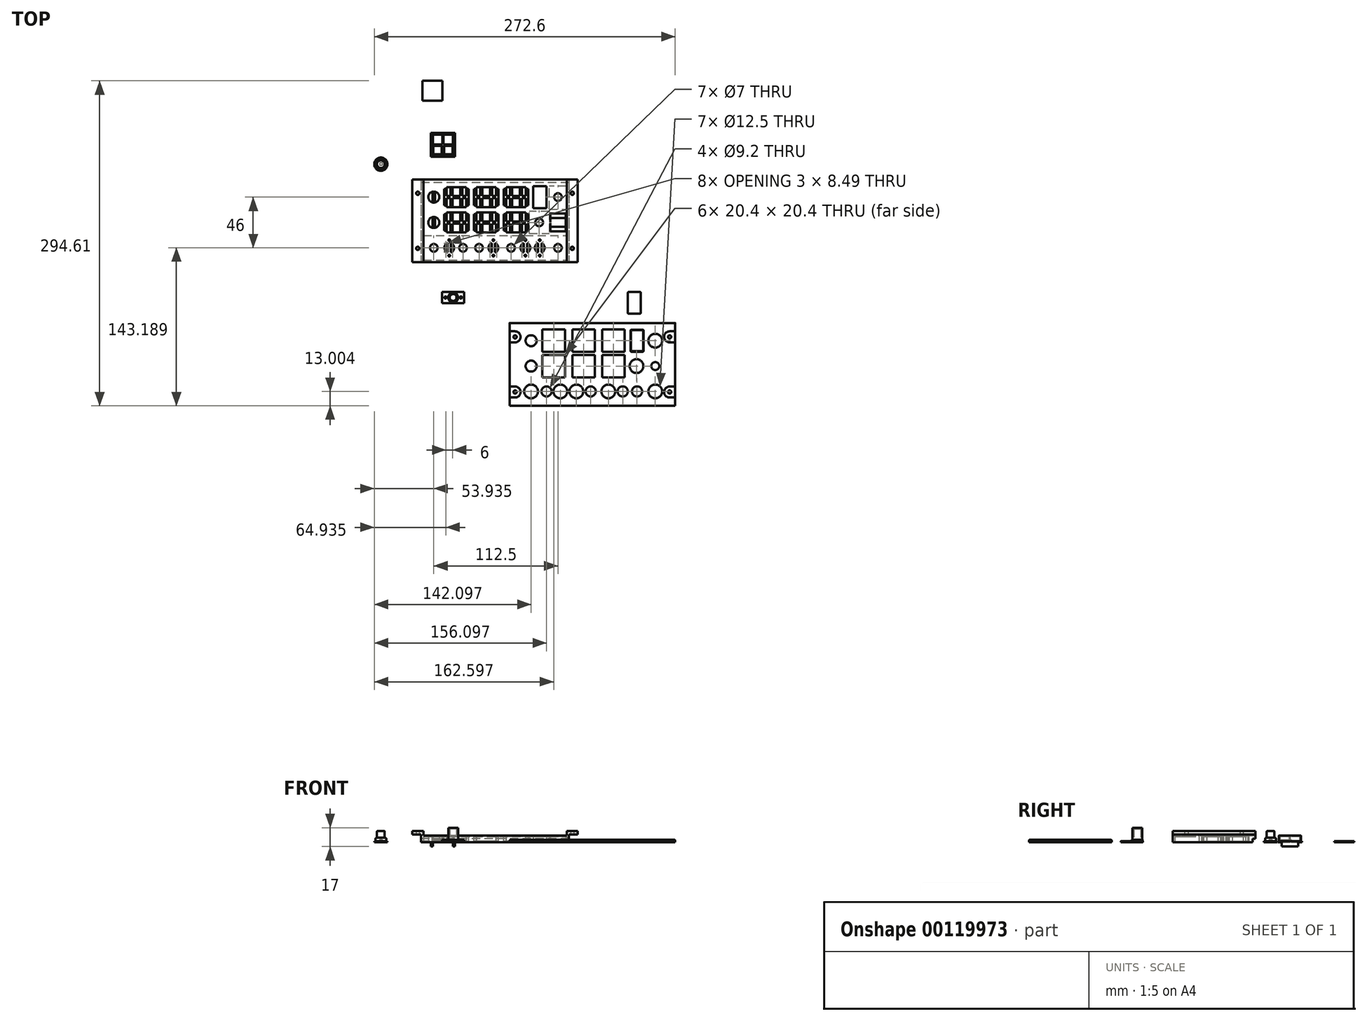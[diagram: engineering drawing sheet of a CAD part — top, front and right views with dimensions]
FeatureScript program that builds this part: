
annotation { "Feature Type Name" : "Feature", "Feature Type Description" : "" }
export const myFeature = defineFeature(function(context is Context, id is Id, definition is map)
    precondition{}
    {
        {
            var Q0;
            Q0=qCreatedBy(makeId("Top.planeOp"),FACE);
            var sketch = newSketch(context, id + "F0", { "sketchPlane" : qUnion([Q0])});
            skLineSegment(sketch, "E0.bottom", {"start": v(0.5, -57.04) * mm, "end": v(-149.5, -57.04) * mm});
            skLineSegment(sketch, "E0.top", {"start": v(0.5, 17.96) * mm, "end": v(-149.5, 17.96) * mm});
            skLineSegment(sketch, "E0.left", {"start": v(0.5, -57.04) * mm, "end": v(0.5, 17.96) * mm});
            skLineSegment(sketch, "E0.right", {"start": v(-149.5, -57.04) * mm, "end": v(-149.5, 17.96) * mm});
            skLineSegment(sketch, "E1.bottom", {"start": v(-99.5, -8.04) * mm, "end": v(-119.5, -8.04) * mm, "construction": true});
            skLineSegment(sketch, "E1.top", {"start": v(-99.5, 11.96) * mm, "end": v(-119.5, 11.96) * mm, "construction": true});
            skLineSegment(sketch, "E1.left", {"start": v(-99.5, -8.04) * mm, "end": v(-99.5, 11.96) * mm, "construction": true});
            skLineSegment(sketch, "E1.right", {"start": v(-119.5, -8.04) * mm, "end": v(-119.5, 11.96) * mm, "construction": true});
            skPoint(sketch, "E1.middle", {"position": v(-109.5, 1.96) * mm});
            skLineSegment(sketch, "E2.bottom", {"start": v(-99.5, -31.04) * mm, "end": v(-119.5, -31.04) * mm, "construction": true});
            skLineSegment(sketch, "E2.top", {"start": v(-99.5, -11.04) * mm, "end": v(-119.5, -11.04) * mm, "construction": true});
            skLineSegment(sketch, "E2.left", {"start": v(-99.5, -31.04) * mm, "end": v(-99.5, -11.04) * mm, "construction": true});
            skLineSegment(sketch, "E2.right", {"start": v(-119.5, -31.04) * mm, "end": v(-119.5, -11.04) * mm, "construction": true});
            skPoint(sketch, "E2.middle", {"position": v(-109.5, -21.04) * mm});
            skCircle(sketch, "E3", {"center": v(-103.5, -44.04) * mm, "radius": 3.5 * mm});
            skCircle(sketch, "E4", {"center": v(-89, -44.04) * mm, "radius": 3.5 * mm});
            skLineSegment(sketch, "E5.bottom", {"start": v(-149.5, 17.96) * mm, "end": v(-141.5, 17.96) * mm, "construction": true});
            skLineSegment(sketch, "E5.top", {"start": v(-149.5, -57.04) * mm, "end": v(-141.5, -57.04) * mm, "construction": true});
            skLineSegment(sketch, "E5.left", {"start": v(-149.5, 17.96) * mm, "end": v(-149.5, -57.04) * mm, "construction": true});
            skLineSegment(sketch, "E5.right", {"start": v(-141.5, 17.96) * mm, "end": v(-141.5, -57.04) * mm, "construction": true});
            skLineSegment(sketch, "E6.bottom", {"start": v(0.5, -57.04) * mm, "end": v(-7.5, -57.04) * mm, "construction": true});
            skLineSegment(sketch, "E6.top", {"start": v(0.5, 17.96) * mm, "end": v(-7.5, 17.96) * mm, "construction": true});
            skLineSegment(sketch, "E6.left", {"start": v(0.5, -57.04) * mm, "end": v(0.5, 17.96) * mm, "construction": true});
            skLineSegment(sketch, "E6.right", {"start": v(-7.5, -57.04) * mm, "end": v(-7.5, 17.96) * mm, "construction": true});
            skCircle(sketch, "E7", {"center": v(-116, -44.04) * mm, "radius": 4.5 * mm});
            skCircle(sketch, "E8", {"center": v(-76, -44.04) * mm, "radius": 4.5 * mm});
            skCircle(sketch, "E9", {"center": v(-60, -44.04) * mm, "radius": 3.5 * mm});
            skCircle(sketch, "E10", {"center": v(-47, -44.04) * mm, "radius": 4.5 * mm});
            skCircle(sketch, "E11", {"center": v(-34, -44.04) * mm, "radius": 4.5 * mm});
            skCircle(sketch, "E12", {"center": v(-17.5, -44.04) * mm, "radius": 3.5 * mm});
            skCircle(sketch, "E13", {"center": v(-34.5, -21.04) * mm, "radius": 3.5 * mm});
            skLineSegment(sketch, "E14.bottom", {"start": v(-28, -8.04) * mm, "end": v(-40, -8.04) * mm});
            skLineSegment(sketch, "E14.top", {"start": v(-28, 11.96) * mm, "end": v(-40, 11.96) * mm});
            skLineSegment(sketch, "E14.left", {"start": v(-28, -8.04) * mm, "end": v(-28, 11.96) * mm});
            skLineSegment(sketch, "E14.right", {"start": v(-40, -8.04) * mm, "end": v(-40, 11.96) * mm});
            skPoint(sketch, "E14.middle", {"position": v(-34, 1.96) * mm});
            skCircle(sketch, "E15", {"center": v(-17.5, 1.96) * mm, "radius": 3.5 * mm});
            skCircle(sketch, "E16", {"center": v(-17.5, -21.04) * mm, "radius": 5 * mm, "construction": true});
            skPoint(sketch, "E17.centerSnap0", {"position": v(-119.5, -21.04) * mm});
            skLineSegment(sketch, "E18.bottom", {"start": v(-100.5, -7.04) * mm, "end": v(-118.5, -7.04) * mm});
            skLineSegment(sketch, "E18.top", {"start": v(-100.5, 10.96) * mm, "end": v(-118.5, 10.96) * mm});
            skLineSegment(sketch, "E18.left", {"start": v(-100.5, -7.04) * mm, "end": v(-100.5, 10.96) * mm});
            skLineSegment(sketch, "E18.right", {"start": v(-118.5, -7.04) * mm, "end": v(-118.5, 10.96) * mm});
            skLineSegment(sketch, "E19.bottom", {"start": v(-100.5, -30.04) * mm, "end": v(-118.5, -30.04) * mm});
            skLineSegment(sketch, "E19.top", {"start": v(-100.5, -12.04) * mm, "end": v(-118.5, -12.04) * mm});
            skLineSegment(sketch, "E19.left", {"start": v(-100.5, -30.04) * mm, "end": v(-100.5, -12.04) * mm});
            skLineSegment(sketch, "E19.right", {"start": v(-118.5, -30.04) * mm, "end": v(-118.5, -12.04) * mm});
            skLineSegment(sketch, "E20.bottom", {"start": v(-100.5, 0.96) * mm, "end": v(-104, 0.96) * mm});
            skLineSegment(sketch, "E20.top", {"start": v(-100.5, 2.96) * mm, "end": v(-104, 2.96) * mm});
            skLineSegment(sketch, "E20.left", {"start": v(-100.5, 0.96) * mm, "end": v(-100.5, 2.96) * mm});
            skLineSegment(sketch, "E20.right", {"start": v(-118.5, 0.96) * mm, "end": v(-118.5, 2.96) * mm});
            skLineSegment(sketch, "E21.bottom", {"start": v(-113, -7.04) * mm, "end": v(-115, -7.04) * mm});
            skLineSegment(sketch, "E21.top", {"start": v(-113, 10.96) * mm, "end": v(-115, 10.96) * mm});
            skLineSegment(sketch, "E21.left", {"start": v(-113, -7.04) * mm, "end": v(-113, 0.96) * mm});
            skLineSegment(sketch, "E21.right", {"start": v(-115, -7.04) * mm, "end": v(-115, 0.96) * mm});
            skPoint(sketch, "E21.middle", {"position": v(-114, 1.96) * mm});
            skLineSegment(sketch, "E22.bottom", {"start": v(-104, -7.04) * mm, "end": v(-106, -7.04) * mm});
            skLineSegment(sketch, "E22.top", {"start": v(-104, 10.96) * mm, "end": v(-106, 10.96) * mm});
            skLineSegment(sketch, "E22.left", {"start": v(-104, -7.04) * mm, "end": v(-104, 0.96) * mm});
            skLineSegment(sketch, "E22.right", {"start": v(-106, -7.04) * mm, "end": v(-106, 0.96) * mm});
            skPoint(sketch, "E22.middle", {"position": v(-105, 1.96) * mm});
            skLineSegment(sketch, "E23.trimOffspring", {"start": v(-115, 2.96) * mm, "end": v(-115, 10.96) * mm});
            skLineSegment(sketch, "E24.trimOffspring", {"start": v(-115, 2.96) * mm, "end": v(-118.5, 2.96) * mm});
            skLineSegment(sketch, "E25.trimOffspring", {"start": v(-113, 2.96) * mm, "end": v(-113, 10.96) * mm});
            skLineSegment(sketch, "E26.trimOffspring", {"start": v(-115, 0.96) * mm, "end": v(-118.5, 0.96) * mm});
            skLineSegment(sketch, "E27.trimOffspring", {"start": v(-106, 2.96) * mm, "end": v(-106, 10.96) * mm});
            skLineSegment(sketch, "E28.trimOffspring", {"start": v(-106, 2.96) * mm, "end": v(-113, 2.96) * mm});
            skLineSegment(sketch, "E29.trimOffspring", {"start": v(-104, 2.96) * mm, "end": v(-104, 10.96) * mm});
            skLineSegment(sketch, "E30.trimOffspring", {"start": v(-106, 0.96) * mm, "end": v(-113, 0.96) * mm});
            skLineSegment(sketch, "E31.bottom", {"start": v(-100.5, -22.04) * mm, "end": v(-104, -22.04) * mm});
            skLineSegment(sketch, "E31.top", {"start": v(-100.5, -20.04) * mm, "end": v(-104, -20.04) * mm});
            skLineSegment(sketch, "E31.left", {"start": v(-100.5, -22.04) * mm, "end": v(-100.5, -20.04) * mm});
            skLineSegment(sketch, "E31.right", {"start": v(-118.5, -22.04) * mm, "end": v(-118.5, -20.04) * mm});
            skLineSegment(sketch, "E32.bottom", {"start": v(-113, -30.04) * mm, "end": v(-115, -30.04) * mm});
            skLineSegment(sketch, "E32.top", {"start": v(-113, -12.04) * mm, "end": v(-115, -12.04) * mm});
            skLineSegment(sketch, "E32.left", {"start": v(-113, -30.04) * mm, "end": v(-113, -22.04) * mm});
            skLineSegment(sketch, "E32.right", {"start": v(-115, -30.04) * mm, "end": v(-115, -22.04) * mm});
            skPoint(sketch, "E32.middle", {"position": v(-114, -21.04) * mm});
            skLineSegment(sketch, "E33.bottom", {"start": v(-104, -30.04) * mm, "end": v(-106, -30.04) * mm});
            skLineSegment(sketch, "E33.top", {"start": v(-104, -12.04) * mm, "end": v(-106, -12.04) * mm});
            skLineSegment(sketch, "E33.left", {"start": v(-104, -30.04) * mm, "end": v(-104, -22.04) * mm});
            skLineSegment(sketch, "E33.right", {"start": v(-106, -30.04) * mm, "end": v(-106, -22.04) * mm});
            skPoint(sketch, "E33.middle", {"position": v(-105, -21.04) * mm});
            skLineSegment(sketch, "E34.trimOffspring", {"start": v(-115, -20.04) * mm, "end": v(-115, -12.04) * mm});
            skLineSegment(sketch, "E35.trimOffspring", {"start": v(-115, -20.04) * mm, "end": v(-118.5, -20.04) * mm});
            skLineSegment(sketch, "E36.trimOffspring", {"start": v(-113, -20.04) * mm, "end": v(-113, -12.04) * mm});
            skLineSegment(sketch, "E37.trimOffspring", {"start": v(-115, -22.04) * mm, "end": v(-118.5, -22.04) * mm});
            skLineSegment(sketch, "E38.trimOffspring", {"start": v(-106, -20.04) * mm, "end": v(-106, -12.04) * mm});
            skLineSegment(sketch, "E39.trimOffspring", {"start": v(-106, -20.04) * mm, "end": v(-113, -20.04) * mm});
            skLineSegment(sketch, "E40.trimOffspring", {"start": v(-104, -20.04) * mm, "end": v(-104, -12.04) * mm});
            skLineSegment(sketch, "E41.trimOffspring", {"start": v(-106, -22.04) * mm, "end": v(-113, -22.04) * mm});
            skPoint(sketch, "E42.middle", {"position": v(-130, 1.96) * mm});
            skPoint(sketch, "E43.middle", {"position": v(-130, -21.04) * mm});
            skLineSegment(sketch, "E44.left", {"start": v(-129, -2.94) * mm, "end": v(-129, 6.86) * mm});
            skLineSegment(sketch, "E44.right", {"start": v(-131, -2.94) * mm, "end": v(-131, 6.86) * mm});
            skLineSegment(sketch, "E45.left", {"start": v(-129, -25.94) * mm, "end": v(-129, -16.14) * mm});
            skLineSegment(sketch, "E45.right", {"start": v(-131, -25.94) * mm, "end": v(-131, -16.14) * mm});
            skCircle(sketch, "E46", {"center": v(-144.5, 5.46) * mm, "radius": 1.5 * mm});
            skPoint(sketch, "E46.centerSnap0", {"position": v(-145.5, 17.96) * mm});
            skCircle(sketch, "E47", {"center": v(-144.5, -44.54) * mm, "radius": 1.5 * mm});
            skCircle(sketch, "E48", {"center": v(-4.5, 5.46) * mm, "radius": 1.5 * mm});
            skCircle(sketch, "E49", {"center": v(-4.5, -44.54) * mm, "radius": 1.5 * mm});
            skLineSegment(sketch, "E50.1.0.0", {"start": v(-73.5, 2.96) * mm, "end": v(-77, 2.96) * mm});
            skLineSegment(sketch, "E50.1.0.1", {"start": v(-79, -30.04) * mm, "end": v(-79, -22.04) * mm});
            skLineSegment(sketch, "E50.1.0.2", {"start": v(-79, -22.04) * mm, "end": v(-86, -22.04) * mm});
            skLineSegment(sketch, "E50.1.0.3", {"start": v(-88, -30.04) * mm, "end": v(-88, -22.04) * mm});
            skLineSegment(sketch, "E50.1.0.4", {"start": v(-72.5, -8.04) * mm, "end": v(-72.5, 11.96) * mm, "construction": true});
            skLineSegment(sketch, "E50.1.0.5", {"start": v(-72.5, -8.04) * mm, "end": v(-92.5, -8.04) * mm, "construction": true});
            skLineSegment(sketch, "E50.1.0.6", {"start": v(-72.5, -31.04) * mm, "end": v(-92.5, -31.04) * mm, "construction": true});
            skLineSegment(sketch, "E50.1.0.7", {"start": v(-73.5, -30.04) * mm, "end": v(-73.5, -12.04) * mm});
            skLineSegment(sketch, "E50.1.0.8", {"start": v(-73.5, -7.04) * mm, "end": v(-91.5, -7.04) * mm});
            skLineSegment(sketch, "E50.1.0.9", {"start": v(-79, 2.96) * mm, "end": v(-86, 2.96) * mm});
            skLineSegment(sketch, "E50.1.0.10", {"start": v(-79, -20.04) * mm, "end": v(-86, -20.04) * mm});
            skLineSegment(sketch, "E50.1.0.11", {"start": v(-88, 2.96) * mm, "end": v(-91.5, 2.96) * mm});
            skLineSegment(sketch, "E50.1.0.12", {"start": v(-77, -30.04) * mm, "end": v(-77, -22.04) * mm});
            skLineSegment(sketch, "E50.1.0.13", {"start": v(-86, 2.96) * mm, "end": v(-86, 10.96) * mm});
            skLineSegment(sketch, "E50.1.0.14", {"start": v(-77, -20.04) * mm, "end": v(-77, -12.04) * mm});
            skLineSegment(sketch, "E50.1.0.15", {"start": v(-88, -20.04) * mm, "end": v(-88, -12.04) * mm});
            skLineSegment(sketch, "E50.1.0.16", {"start": v(-79, 2.96) * mm, "end": v(-79, 10.96) * mm});
            skPoint(sketch, "E50.1.0.17", {"position": v(-82.5, -21.04) * mm});
            skLineSegment(sketch, "E50.1.0.18", {"start": v(-73.5, -22.04) * mm, "end": v(-77, -22.04) * mm});
            skLineSegment(sketch, "E50.1.0.19", {"start": v(-88, 0.96) * mm, "end": v(-91.5, 0.96) * mm});
            skLineSegment(sketch, "E50.1.0.20", {"start": v(-72.5, 11.96) * mm, "end": v(-92.5, 11.96) * mm, "construction": true});
            skLineSegment(sketch, "E50.1.0.21", {"start": v(-88, -22.04) * mm, "end": v(-91.5, -22.04) * mm});
            skLineSegment(sketch, "E50.1.0.22", {"start": v(-91.5, -7.04) * mm, "end": v(-91.5, 10.96) * mm});
            skLineSegment(sketch, "E50.1.0.23", {"start": v(-72.5, -11.04) * mm, "end": v(-92.5, -11.04) * mm, "construction": true});
            skLineSegment(sketch, "E50.1.0.24", {"start": v(-92.5, -31.04) * mm, "end": v(-92.5, -11.04) * mm, "construction": true});
            skLineSegment(sketch, "E50.1.0.25", {"start": v(-79, -20.04) * mm, "end": v(-79, -12.04) * mm});
            skLineSegment(sketch, "E50.1.0.26", {"start": v(-92.5, -8.04) * mm, "end": v(-92.5, 11.96) * mm, "construction": true});
            skLineSegment(sketch, "E50.1.0.27", {"start": v(-88, 2.96) * mm, "end": v(-88, 10.96) * mm});
            skLineSegment(sketch, "E50.1.0.28", {"start": v(-72.5, -31.04) * mm, "end": v(-72.5, -11.04) * mm, "construction": true});
            skLineSegment(sketch, "E50.1.0.29", {"start": v(-73.5, -7.04) * mm, "end": v(-73.5, 10.96) * mm});
            skLineSegment(sketch, "E50.1.0.30", {"start": v(-73.5, -30.04) * mm, "end": v(-91.5, -30.04) * mm});
            skLineSegment(sketch, "E50.1.0.31", {"start": v(-77, -7.04) * mm, "end": v(-77, 0.96) * mm});
            skLineSegment(sketch, "E50.1.0.32", {"start": v(-79, -7.04) * mm, "end": v(-79, 0.96) * mm});
            skLineSegment(sketch, "E50.1.0.33", {"start": v(-86, -20.04) * mm, "end": v(-86, -12.04) * mm});
            skLineSegment(sketch, "E50.1.0.34", {"start": v(-73.5, 0.96) * mm, "end": v(-77, 0.96) * mm});
            skLineSegment(sketch, "E50.1.0.35", {"start": v(-73.5, -12.04) * mm, "end": v(-91.5, -12.04) * mm});
            skLineSegment(sketch, "E50.1.0.36", {"start": v(-86, -30.04) * mm, "end": v(-86, -22.04) * mm});
            skLineSegment(sketch, "E50.1.0.37", {"start": v(-77, 2.96) * mm, "end": v(-77, 10.96) * mm});
            skLineSegment(sketch, "E50.1.0.38", {"start": v(-88, -7.04) * mm, "end": v(-88, 0.96) * mm});
            skLineSegment(sketch, "E50.1.0.39", {"start": v(-91.5, -30.04) * mm, "end": v(-91.5, -12.04) * mm});
            skLineSegment(sketch, "E50.1.0.40", {"start": v(-73.5, 10.96) * mm, "end": v(-91.5, 10.96) * mm});
            skLineSegment(sketch, "E50.1.0.41", {"start": v(-73.5, -20.04) * mm, "end": v(-77, -20.04) * mm});
            skPoint(sketch, "E50.1.0.42", {"position": v(-82.5, 1.96) * mm});
            skPoint(sketch, "E50.1.0.43", {"position": v(-92.5, -21.04) * mm});
            skLineSegment(sketch, "E50.1.0.44", {"start": v(-79, 0.96) * mm, "end": v(-86, 0.96) * mm});
            skLineSegment(sketch, "E50.1.0.45", {"start": v(-86, -7.04) * mm, "end": v(-86, 0.96) * mm});
            skLineSegment(sketch, "E50.1.0.46", {"start": v(-73.5, -12.04) * mm, "end": v(-91.5, -12.04) * mm});
            skLineSegment(sketch, "E50.1.0.47", {"start": v(-73.5, -30.04) * mm, "end": v(-73.5, -12.04) * mm});
            skLineSegment(sketch, "E50.1.0.48", {"start": v(-73.5, -30.04) * mm, "end": v(-91.5, -30.04) * mm});
            skPoint(sketch, "E50.1.0.49", {"position": v(-82.5, -21.04) * mm});
            skPoint(sketch, "E50.1.0.50", {"position": v(-82.5, 1.96) * mm});
            skLineSegment(sketch, "E50.1.0.51", {"start": v(-88, -20.04) * mm, "end": v(-91.5, -20.04) * mm});
            skLineSegment(sketch, "E50.1.0.52", {"start": v(-91.5, -30.04) * mm, "end": v(-91.5, -12.04) * mm});
            skPoint(sketch, "E50.1.0.53", {"position": v(-87, 1.96) * mm});
            skLineSegment(sketch, "E50.1.0.54", {"start": v(-91.5, -22.04) * mm, "end": v(-91.5, -20.04) * mm});
            skLineSegment(sketch, "E50.1.0.55", {"start": v(-86, -12.04) * mm, "end": v(-88, -12.04) * mm});
            skLineSegment(sketch, "E50.1.0.56", {"start": v(-91.5, 0.96) * mm, "end": v(-91.5, 2.96) * mm});
            skLineSegment(sketch, "E50.1.0.57", {"start": v(-86, 10.96) * mm, "end": v(-88, 10.96) * mm});
            skLineSegment(sketch, "E50.1.0.58", {"start": v(-86, -30.04) * mm, "end": v(-88, -30.04) * mm});
            skLineSegment(sketch, "E50.1.0.59", {"start": v(-73.5, -22.04) * mm, "end": v(-73.5, -20.04) * mm});
            skPoint(sketch, "E50.1.0.60", {"position": v(-78, -21.04) * mm});
            skLineSegment(sketch, "E50.1.0.61", {"start": v(-77, -7.04) * mm, "end": v(-79, -7.04) * mm});
            skPoint(sketch, "E50.1.0.62", {"position": v(-87, -21.04) * mm});
            skPoint(sketch, "E50.1.0.63", {"position": v(-82.5, -21.04) * mm});
            skLineSegment(sketch, "E50.1.0.64", {"start": v(-77, -30.04) * mm, "end": v(-79, -30.04) * mm});
            skLineSegment(sketch, "E50.1.0.65", {"start": v(-73.5, 0.96) * mm, "end": v(-73.5, 2.96) * mm});
            skPoint(sketch, "E50.1.0.66", {"position": v(-82.5, 1.96) * mm});
            skLineSegment(sketch, "E50.1.0.67", {"start": v(-86, -7.04) * mm, "end": v(-88, -7.04) * mm});
            skLineSegment(sketch, "E50.1.0.68", {"start": v(-77, 10.96) * mm, "end": v(-79, 10.96) * mm});
            skPoint(sketch, "E50.1.0.69", {"position": v(-78, 1.96) * mm});
            skLineSegment(sketch, "E50.1.0.70", {"start": v(-77, -12.04) * mm, "end": v(-79, -12.04) * mm});
            skPoint(sketch, "E50.1.0.71", {"position": v(-82.5, -21.04) * mm});
            skPoint(sketch, "E50.1.0.72", {"position": v(-82.5, -21.04) * mm});
            skLineSegment(sketch, "E50.2.0.0", {"start": v(-46.5, 2.96) * mm, "end": v(-50, 2.96) * mm});
            skLineSegment(sketch, "E50.2.0.1", {"start": v(-52, -30.04) * mm, "end": v(-52, -22.04) * mm});
            skLineSegment(sketch, "E50.2.0.2", {"start": v(-52, -22.04) * mm, "end": v(-59, -22.04) * mm});
            skLineSegment(sketch, "E50.2.0.3", {"start": v(-61, -30.04) * mm, "end": v(-61, -22.04) * mm});
            skLineSegment(sketch, "E50.2.0.4", {"start": v(-45.5, -8.04) * mm, "end": v(-45.5, 11.96) * mm, "construction": true});
            skLineSegment(sketch, "E50.2.0.5", {"start": v(-45.5, -8.04) * mm, "end": v(-65.5, -8.04) * mm, "construction": true});
            skLineSegment(sketch, "E50.2.0.6", {"start": v(-45.5, -31.04) * mm, "end": v(-65.5, -31.04) * mm, "construction": true});
            skLineSegment(sketch, "E50.2.0.7", {"start": v(-46.5, -30.04) * mm, "end": v(-46.5, -12.04) * mm});
            skLineSegment(sketch, "E50.2.0.8", {"start": v(-46.5, -7.04) * mm, "end": v(-64.5, -7.04) * mm});
            skLineSegment(sketch, "E50.2.0.9", {"start": v(-52, 2.96) * mm, "end": v(-59, 2.96) * mm});
            skLineSegment(sketch, "E50.2.0.10", {"start": v(-52, -20.04) * mm, "end": v(-59, -20.04) * mm});
            skLineSegment(sketch, "E50.2.0.11", {"start": v(-61, 2.96) * mm, "end": v(-64.5, 2.96) * mm});
            skLineSegment(sketch, "E50.2.0.12", {"start": v(-50, -30.04) * mm, "end": v(-50, -22.04) * mm});
            skLineSegment(sketch, "E50.2.0.13", {"start": v(-59, 2.96) * mm, "end": v(-59, 10.96) * mm});
            skLineSegment(sketch, "E50.2.0.14", {"start": v(-50, -20.04) * mm, "end": v(-50, -12.04) * mm});
            skLineSegment(sketch, "E50.2.0.15", {"start": v(-61, -20.04) * mm, "end": v(-61, -12.04) * mm});
            skLineSegment(sketch, "E50.2.0.16", {"start": v(-52, 2.96) * mm, "end": v(-52, 10.96) * mm});
            skPoint(sketch, "E50.2.0.17", {"position": v(-55.5, -21.04) * mm});
            skLineSegment(sketch, "E50.2.0.18", {"start": v(-46.5, -22.04) * mm, "end": v(-50, -22.04) * mm});
            skLineSegment(sketch, "E50.2.0.19", {"start": v(-61, 0.96) * mm, "end": v(-64.5, 0.96) * mm});
            skLineSegment(sketch, "E50.2.0.20", {"start": v(-45.5, 11.96) * mm, "end": v(-65.5, 11.96) * mm, "construction": true});
            skLineSegment(sketch, "E50.2.0.21", {"start": v(-61, -22.04) * mm, "end": v(-64.5, -22.04) * mm});
            skLineSegment(sketch, "E50.2.0.22", {"start": v(-64.5, -7.04) * mm, "end": v(-64.5, 10.96) * mm});
            skLineSegment(sketch, "E50.2.0.23", {"start": v(-45.5, -11.04) * mm, "end": v(-65.5, -11.04) * mm, "construction": true});
            skLineSegment(sketch, "E50.2.0.24", {"start": v(-65.5, -31.04) * mm, "end": v(-65.5, -11.04) * mm, "construction": true});
            skLineSegment(sketch, "E50.2.0.25", {"start": v(-52, -20.04) * mm, "end": v(-52, -12.04) * mm});
            skLineSegment(sketch, "E50.2.0.26", {"start": v(-65.5, -8.04) * mm, "end": v(-65.5, 11.96) * mm, "construction": true});
            skLineSegment(sketch, "E50.2.0.27", {"start": v(-61, 2.96) * mm, "end": v(-61, 10.96) * mm});
            skLineSegment(sketch, "E50.2.0.28", {"start": v(-45.5, -31.04) * mm, "end": v(-45.5, -11.04) * mm, "construction": true});
            skLineSegment(sketch, "E50.2.0.29", {"start": v(-46.5, -7.04) * mm, "end": v(-46.5, 10.96) * mm});
            skLineSegment(sketch, "E50.2.0.30", {"start": v(-46.5, -30.04) * mm, "end": v(-64.5, -30.04) * mm});
            skLineSegment(sketch, "E50.2.0.31", {"start": v(-50, -7.04) * mm, "end": v(-50, 0.96) * mm});
            skLineSegment(sketch, "E50.2.0.32", {"start": v(-52, -7.04) * mm, "end": v(-52, 0.96) * mm});
            skLineSegment(sketch, "E50.2.0.33", {"start": v(-59, -20.04) * mm, "end": v(-59, -12.04) * mm});
            skLineSegment(sketch, "E50.2.0.34", {"start": v(-46.5, 0.96) * mm, "end": v(-50, 0.96) * mm});
            skLineSegment(sketch, "E50.2.0.35", {"start": v(-46.5, -12.04) * mm, "end": v(-64.5, -12.04) * mm});
            skLineSegment(sketch, "E50.2.0.36", {"start": v(-59, -30.04) * mm, "end": v(-59, -22.04) * mm});
            skLineSegment(sketch, "E50.2.0.37", {"start": v(-50, 2.96) * mm, "end": v(-50, 10.96) * mm});
            skLineSegment(sketch, "E50.2.0.38", {"start": v(-61, -7.04) * mm, "end": v(-61, 0.96) * mm});
            skLineSegment(sketch, "E50.2.0.39", {"start": v(-64.5, -30.04) * mm, "end": v(-64.5, -12.04) * mm});
            skLineSegment(sketch, "E50.2.0.40", {"start": v(-46.5, 10.96) * mm, "end": v(-64.5, 10.96) * mm});
            skLineSegment(sketch, "E50.2.0.41", {"start": v(-46.5, -20.04) * mm, "end": v(-50, -20.04) * mm});
            skPoint(sketch, "E50.2.0.42", {"position": v(-55.5, 1.96) * mm});
            skPoint(sketch, "E50.2.0.43", {"position": v(-65.5, -21.04) * mm});
            skLineSegment(sketch, "E50.2.0.44", {"start": v(-52, 0.96) * mm, "end": v(-59, 0.96) * mm});
            skLineSegment(sketch, "E50.2.0.45", {"start": v(-59, -7.04) * mm, "end": v(-59, 0.96) * mm});
            skLineSegment(sketch, "E50.2.0.46", {"start": v(-46.5, -12.04) * mm, "end": v(-64.5, -12.04) * mm});
            skLineSegment(sketch, "E50.2.0.47", {"start": v(-46.5, -30.04) * mm, "end": v(-46.5, -12.04) * mm});
            skLineSegment(sketch, "E50.2.0.48", {"start": v(-46.5, -30.04) * mm, "end": v(-64.5, -30.04) * mm});
            skPoint(sketch, "E50.2.0.49", {"position": v(-55.5, -21.04) * mm});
            skPoint(sketch, "E50.2.0.50", {"position": v(-55.5, 1.96) * mm});
            skLineSegment(sketch, "E50.2.0.51", {"start": v(-61, -20.04) * mm, "end": v(-64.5, -20.04) * mm});
            skLineSegment(sketch, "E50.2.0.52", {"start": v(-64.5, -30.04) * mm, "end": v(-64.5, -12.04) * mm});
            skPoint(sketch, "E50.2.0.53", {"position": v(-60, 1.96) * mm});
            skLineSegment(sketch, "E50.2.0.54", {"start": v(-64.5, -22.04) * mm, "end": v(-64.5, -20.04) * mm});
            skLineSegment(sketch, "E50.2.0.55", {"start": v(-59, -12.04) * mm, "end": v(-61, -12.04) * mm});
            skLineSegment(sketch, "E50.2.0.56", {"start": v(-64.5, 0.96) * mm, "end": v(-64.5, 2.96) * mm});
            skLineSegment(sketch, "E50.2.0.57", {"start": v(-59, 10.96) * mm, "end": v(-61, 10.96) * mm});
            skLineSegment(sketch, "E50.2.0.58", {"start": v(-59, -30.04) * mm, "end": v(-61, -30.04) * mm});
            skLineSegment(sketch, "E50.2.0.59", {"start": v(-46.5, -22.04) * mm, "end": v(-46.5, -20.04) * mm});
            skPoint(sketch, "E50.2.0.60", {"position": v(-51, -21.04) * mm});
            skLineSegment(sketch, "E50.2.0.61", {"start": v(-50, -7.04) * mm, "end": v(-52, -7.04) * mm});
            skPoint(sketch, "E50.2.0.62", {"position": v(-60, -21.04) * mm});
            skPoint(sketch, "E50.2.0.63", {"position": v(-55.5, -21.04) * mm});
            skLineSegment(sketch, "E50.2.0.64", {"start": v(-50, -30.04) * mm, "end": v(-52, -30.04) * mm});
            skLineSegment(sketch, "E50.2.0.65", {"start": v(-46.5, 0.96) * mm, "end": v(-46.5, 2.96) * mm});
            skPoint(sketch, "E50.2.0.66", {"position": v(-55.5, 1.96) * mm});
            skLineSegment(sketch, "E50.2.0.67", {"start": v(-59, -7.04) * mm, "end": v(-61, -7.04) * mm});
            skLineSegment(sketch, "E50.2.0.68", {"start": v(-50, 10.96) * mm, "end": v(-52, 10.96) * mm});
            skPoint(sketch, "E50.2.0.69", {"position": v(-51, 1.96) * mm});
            skLineSegment(sketch, "E50.2.0.70", {"start": v(-50, -12.04) * mm, "end": v(-52, -12.04) * mm});
            skPoint(sketch, "E50.2.0.71", {"position": v(-55.5, -21.04) * mm});
            skPoint(sketch, "E50.2.0.72", {"position": v(-55.5, -21.04) * mm});
            skLineSegment(sketch, "E50.direction1", {"start": v(-119.5, -31.04) * mm, "end": v(-92.5, -31.04) * mm, "construction": true});
            skCircle(sketch, "E51", {"center": v(-130, 1.96) * mm, "radius": 5 * mm});
            skCircle(sketch, "E52", {"center": v(-130, -21.04) * mm, "radius": 5 * mm});
            skLineSegment(sketch, "E53.bottom", {"start": v(-32.5, -8.04) * mm, "end": v(-35.5, -8.04) * mm});
            skLineSegment(sketch, "E53.top", {"start": v(-32.5, 11.96) * mm, "end": v(-35.5, 11.96) * mm});
            skLineSegment(sketch, "E53.left", {"start": v(-32.5, -8.04) * mm, "end": v(-32.5, 11.96) * mm});
            skLineSegment(sketch, "E53.right", {"start": v(-35.5, -8.04) * mm, "end": v(-35.5, 11.96) * mm});
            skLineSegment(sketch, "E54.bottom", {"start": v(-10.5, -29.04) * mm, "end": v(-24.5, -29.04) * mm});
            skLineSegment(sketch, "E54.top", {"start": v(-10.5, -13.04) * mm, "end": v(-24.5, -13.04) * mm});
            skLineSegment(sketch, "E54.left", {"start": v(-10.5, -29.04) * mm, "end": v(-10.5, -13.04) * mm});
            skLineSegment(sketch, "E54.right", {"start": v(-24.5, -29.04) * mm, "end": v(-24.5, -13.04) * mm});
            skLineSegment(sketch, "E55.bottom", {"start": v(-10.5, -25.04) * mm, "end": v(-24.5, -25.04) * mm});
            skLineSegment(sketch, "E55.top", {"start": v(-10.5, -17.04) * mm, "end": v(-24.5, -17.04) * mm});
            skLineSegment(sketch, "E55.left", {"start": v(-10.5, -25.04) * mm, "end": v(-10.5, -17.04) * mm});
            skLineSegment(sketch, "E55.right", {"start": v(-24.5, -25.04) * mm, "end": v(-24.5, -17.04) * mm});
            skLineSegment(sketch, "E56.bottom", {"start": v(-27.5, -28.04) * mm, "end": v(-41.5, -28.04) * mm, "construction": true});
            skLineSegment(sketch, "E56.top", {"start": v(-27.5, -14.04) * mm, "end": v(-41.5, -14.04) * mm, "construction": true});
            skLineSegment(sketch, "E56.left", {"start": v(-27.5, -28.04) * mm, "end": v(-27.5, -14.04) * mm, "construction": true});
            skLineSegment(sketch, "E56.right", {"start": v(-41.5, -28.04) * mm, "end": v(-41.5, -14.04) * mm, "construction": true});
            skCircle(sketch, "E57", {"center": v(-34.5, -21.04) * mm, "radius": 6.25 * mm, "construction": true});
            skLineSegment(sketch, "E58.bottom", {"start": v(-10.5, 8.96) * mm, "end": v(-24.5, 8.96) * mm, "construction": true});
            skLineSegment(sketch, "E58.top", {"start": v(-10.5, -5.04) * mm, "end": v(-24.5, -5.04) * mm, "construction": true});
            skLineSegment(sketch, "E58.left", {"start": v(-10.5, 8.96) * mm, "end": v(-10.5, -5.04) * mm, "construction": true});
            skLineSegment(sketch, "E58.right", {"start": v(-24.5, 8.96) * mm, "end": v(-24.5, -5.04) * mm, "construction": true});
            skLineSegment(sketch, "E59.bottom", {"start": v(-111, -54.04) * mm, "end": v(-121, -54.04) * mm, "construction": true});
            skLineSegment(sketch, "E59.top", {"start": v(-111, -34.04) * mm, "end": v(-121, -34.04) * mm, "construction": true});
            skLineSegment(sketch, "E59.left", {"start": v(-111, -54.04) * mm, "end": v(-111, -34.04) * mm, "construction": true});
            skLineSegment(sketch, "E59.right", {"start": v(-121, -54.04) * mm, "end": v(-121, -34.04) * mm, "construction": true});
            skCircle(sketch, "E60", {"center": v(-116, -37.04) * mm, "radius": 0.8 * mm});
            skCircle(sketch, "E61", {"center": v(-116, -51.04) * mm, "radius": 0.8 * mm});
            skLineSegment(sketch, "E62.bottom", {"start": v(-71, -54.04) * mm, "end": v(-81, -54.04) * mm, "construction": true});
            skLineSegment(sketch, "E62.top", {"start": v(-71, -34.04) * mm, "end": v(-81, -34.04) * mm, "construction": true});
            skLineSegment(sketch, "E62.left", {"start": v(-71, -54.04) * mm, "end": v(-71, -34.04) * mm, "construction": true});
            skLineSegment(sketch, "E62.right", {"start": v(-81, -54.04) * mm, "end": v(-81, -34.04) * mm, "construction": true});
            skCircle(sketch, "E63", {"center": v(-76, -37.04) * mm, "radius": 0.8 * mm});
            skCircle(sketch, "E64", {"center": v(-76, -51.04) * mm, "radius": 0.8 * mm});
            skLineSegment(sketch, "E65.bottom", {"start": v(-42, -54.04) * mm, "end": v(-52, -54.04) * mm, "construction": true});
            skLineSegment(sketch, "E65.top", {"start": v(-42, -34.04) * mm, "end": v(-52, -34.04) * mm, "construction": true});
            skLineSegment(sketch, "E65.left", {"start": v(-42, -54.04) * mm, "end": v(-42, -34.04) * mm, "construction": true});
            skLineSegment(sketch, "E65.right", {"start": v(-52, -54.04) * mm, "end": v(-52, -34.04) * mm, "construction": true});
            skCircle(sketch, "E66", {"center": v(-47, -37.04) * mm, "radius": 0.8 * mm});
            skCircle(sketch, "E67", {"center": v(-47, -51.04) * mm, "radius": 0.8 * mm});
            skLineSegment(sketch, "E68.bottom", {"start": v(-29, -54.04) * mm, "end": v(-39, -54.04) * mm, "construction": true});
            skLineSegment(sketch, "E68.top", {"start": v(-29, -34.04) * mm, "end": v(-39, -34.04) * mm, "construction": true});
            skLineSegment(sketch, "E68.left", {"start": v(-29, -54.04) * mm, "end": v(-29, -34.04) * mm, "construction": true});
            skLineSegment(sketch, "E68.right", {"start": v(-39, -54.04) * mm, "end": v(-39, -34.04) * mm, "construction": true});
            skCircle(sketch, "E69", {"center": v(-34, -37.04) * mm, "radius": 0.8 * mm});
            skCircle(sketch, "E70", {"center": v(-34, -51.04) * mm, "radius": 0.8 * mm});
            skCircle(sketch, "E71", {"center": v(-130, -44.04) * mm, "radius": 3.5 * mm});
            skLineSegment(sketch, "E72.bottom", {"start": v(-126.5, -50.54) * mm, "end": v(-133.5, -50.54) * mm, "construction": true});
            skLineSegment(sketch, "E72.top", {"start": v(-126.5, -37.54) * mm, "end": v(-133.5, -37.54) * mm, "construction": true});
            skLineSegment(sketch, "E72.left", {"start": v(-126.5, -50.54) * mm, "end": v(-126.5, -37.54) * mm, "construction": true});
            skLineSegment(sketch, "E72.right", {"start": v(-133.5, -50.54) * mm, "end": v(-133.5, -37.54) * mm, "construction": true});
            skSolve(sketch);
        }
        {
            var Q0;
            Q0=qCreatedBy(makeId("Top.planeOp"),FACE);
            var sketch = newSketch(context, id + "F1", { "sketchPlane" : qUnion([Q0])});
            skLineSegment(sketch, "E73.bottom", {"start": v(88.66, -187.23) * mm, "end": v(-61.34, -187.23) * mm});
            skLineSegment(sketch, "E73.top", {"start": v(88.66, -112.23) * mm, "end": v(-61.34, -112.23) * mm});
            skLineSegment(sketch, "E73.left", {"start": v(88.66, -187.23) * mm, "end": v(88.66, -112.23) * mm});
            skLineSegment(sketch, "E73.right", {"start": v(-61.34, -187.23) * mm, "end": v(-61.34, -112.23) * mm});
            skLineSegment(sketch, "E74.bottom", {"start": v(-11.14, -138.43) * mm, "end": v(-31.54, -138.43) * mm});
            skLineSegment(sketch, "E74.top", {"start": v(-11.14, -118.03) * mm, "end": v(-31.54, -118.03) * mm});
            skLineSegment(sketch, "E74.left", {"start": v(-11.14, -138.43) * mm, "end": v(-11.14, -118.03) * mm});
            skLineSegment(sketch, "E74.right", {"start": v(-31.54, -138.43) * mm, "end": v(-31.54, -118.03) * mm});
            skLineSegment(sketch, "E75.bottom", {"start": v(-11.14, -161.43) * mm, "end": v(-31.54, -161.43) * mm});
            skLineSegment(sketch, "E75.top", {"start": v(-11.14, -141.03) * mm, "end": v(-31.54, -141.03) * mm});
            skLineSegment(sketch, "E75.left", {"start": v(-11.14, -161.43) * mm, "end": v(-11.14, -141.03) * mm});
            skLineSegment(sketch, "E75.right", {"start": v(-31.54, -161.43) * mm, "end": v(-31.54, -141.03) * mm});
            skCircle(sketch, "E76", {"center": v(-15.34, -174.23) * mm, "radius": 3.5 * mm, "construction": true});
            skCircle(sketch, "E77", {"center": v(-0.84, -174.23) * mm, "radius": 3.5 * mm, "construction": true});
            skLineSegment(sketch, "E78.bottom", {"start": v(-61.34, -112.23) * mm, "end": v(-53.34, -112.23) * mm, "construction": true});
            skLineSegment(sketch, "E78.top", {"start": v(-61.34, -187.23) * mm, "end": v(-53.34, -187.23) * mm, "construction": true});
            skLineSegment(sketch, "E78.left", {"start": v(-61.34, -112.23) * mm, "end": v(-61.34, -187.23) * mm, "construction": true});
            skLineSegment(sketch, "E78.right", {"start": v(-53.34, -112.23) * mm, "end": v(-53.34, -187.23) * mm, "construction": true});
            skLineSegment(sketch, "E79.bottom", {"start": v(88.66, -187.23) * mm, "end": v(80.66, -187.23) * mm, "construction": true});
            skLineSegment(sketch, "E79.top", {"start": v(88.66, -112.23) * mm, "end": v(80.66, -112.23) * mm, "construction": true});
            skLineSegment(sketch, "E79.left", {"start": v(88.66, -187.23) * mm, "end": v(88.66, -112.23) * mm, "construction": true});
            skLineSegment(sketch, "E79.right", {"start": v(80.66, -187.23) * mm, "end": v(80.66, -112.23) * mm, "construction": true});
            skCircle(sketch, "E80", {"center": v(-27.84, -174.23) * mm, "radius": 4.6 * mm});
            skCircle(sketch, "E81", {"center": v(12.16, -174.23) * mm, "radius": 4.6 * mm});
            skCircle(sketch, "E82", {"center": v(28.16, -174.23) * mm, "radius": 3.5 * mm, "construction": true});
            skCircle(sketch, "E83", {"center": v(41.16, -174.23) * mm, "radius": 4.6 * mm});
            skCircle(sketch, "E84", {"center": v(54.16, -174.23) * mm, "radius": 4.6 * mm});
            skCircle(sketch, "E85", {"center": v(70.66, -174.23) * mm, "radius": 3.5 * mm, "construction": true});
            skCircle(sketch, "E86", {"center": v(53.66, -151.23) * mm, "radius": 3.5 * mm, "construction": true});
            skLineSegment(sketch, "E87.bottom", {"start": v(60.16, -138.23) * mm, "end": v(48.16, -138.23) * mm});
            skLineSegment(sketch, "E87.top", {"start": v(60.16, -118.23) * mm, "end": v(48.16, -118.23) * mm});
            skLineSegment(sketch, "E87.left", {"start": v(60.16, -138.23) * mm, "end": v(60.16, -118.23) * mm});
            skLineSegment(sketch, "E87.right", {"start": v(48.16, -138.23) * mm, "end": v(48.16, -118.23) * mm});
            skPoint(sketch, "E87.middle", {"position": v(54.16, -128.23) * mm});
            skCircle(sketch, "E88", {"center": v(70.66, -128.23) * mm, "radius": 3.5 * mm, "construction": true});
            skCircle(sketch, "E89", {"center": v(70.66, -151.23) * mm, "radius": 3.6 * mm});
            skLineSegment(sketch, "E90.bottom", {"start": v(-36.84, -133.23) * mm, "end": v(-46.84, -133.23) * mm, "construction": true});
            skLineSegment(sketch, "E90.top", {"start": v(-36.84, -123.23) * mm, "end": v(-46.84, -123.23) * mm, "construction": true});
            skLineSegment(sketch, "E90.left", {"start": v(-36.84, -133.23) * mm, "end": v(-36.84, -123.23) * mm, "construction": true});
            skLineSegment(sketch, "E90.right", {"start": v(-46.84, -133.23) * mm, "end": v(-46.84, -123.23) * mm, "construction": true});
            skPoint(sketch, "E90.middle", {"position": v(-41.84, -128.23) * mm});
            skLineSegment(sketch, "E91.bottom", {"start": v(-40.84, -133.23) * mm, "end": v(-42.84, -133.23) * mm});
            skLineSegment(sketch, "E91.top", {"start": v(-40.84, -123.23) * mm, "end": v(-42.84, -123.23) * mm});
            skLineSegment(sketch, "E91.left", {"start": v(-40.84, -133.23) * mm, "end": v(-40.84, -123.23) * mm});
            skLineSegment(sketch, "E91.right", {"start": v(-42.84, -133.23) * mm, "end": v(-42.84, -123.23) * mm});
            skCircle(sketch, "E92", {"center": v(-56.34, -124.73) * mm, "radius": 1.5 * mm});
            skPoint(sketch, "E92.centerSnap0", {"position": v(-57.34, -112.23) * mm});
            skCircle(sketch, "E93", {"center": v(-41.84, -128.23) * mm, "radius": 5 * mm});
            skCircle(sketch, "E94", {"center": v(-15.34, -174.23) * mm, "radius": 6.25 * mm});
            skCircle(sketch, "E95", {"center": v(-0.84, -174.23) * mm, "radius": 6.25 * mm});
            skCircle(sketch, "E96", {"center": v(28.16, -174.23) * mm, "radius": 6.25 * mm});
            skCircle(sketch, "E97", {"center": v(70.66, -174.23) * mm, "radius": 6.25 * mm});
            skCircle(sketch, "E98", {"center": v(53.66, -151.23) * mm, "radius": 6.25 * mm});
            skCircle(sketch, "E99", {"center": v(70.66, -128.23) * mm, "radius": 6.25 * mm});
            skCircle(sketch, "E100", {"center": v(-56.34, -174.73) * mm, "radius": 1.5 * mm});
            skCircle(sketch, "E101", {"center": v(83.66, -124.73) * mm, "radius": 1.5 * mm});
            skCircle(sketch, "E102", {"center": v(83.66, -174.73) * mm, "radius": 1.5 * mm});
            skLineSegment(sketch, "E103.bottom", {"start": v(-53.34, -112.23) * mm, "end": v(-51.34, -112.23) * mm, "construction": true});
            skLineSegment(sketch, "E103.top", {"start": v(-53.34, -187.23) * mm, "end": v(-51.34, -187.23) * mm, "construction": true});
            skLineSegment(sketch, "E103.right", {"start": v(-51.34, -112.23) * mm, "end": v(-51.34, -187.23) * mm, "construction": true});
            skLineSegment(sketch, "E104.bottom", {"start": v(80.66, -112.23) * mm, "end": v(78.66, -112.23) * mm, "construction": true});
            skLineSegment(sketch, "E104.top", {"start": v(80.66, -187.23) * mm, "end": v(78.66, -187.23) * mm, "construction": true});
            skLineSegment(sketch, "E104.left", {"start": v(80.66, -112.23) * mm, "end": v(80.66, -187.23) * mm, "construction": true});
            skLineSegment(sketch, "E104.right", {"start": v(78.66, -112.23) * mm, "end": v(78.66, -187.23) * mm, "construction": true});
            skLineSegment(sketch, "E105.1.0.0", {"start": v(15.86, -138.43) * mm, "end": v(-4.54, -138.43) * mm});
            skLineSegment(sketch, "E105.1.0.1", {"start": v(15.86, -118.03) * mm, "end": v(-4.54, -118.03) * mm});
            skLineSegment(sketch, "E105.1.0.2", {"start": v(15.86, -138.43) * mm, "end": v(15.86, -118.03) * mm});
            skLineSegment(sketch, "E105.1.0.3", {"start": v(-4.54, -138.43) * mm, "end": v(-4.54, -118.03) * mm});
            skLineSegment(sketch, "E105.2.0.0", {"start": v(42.86, -138.43) * mm, "end": v(22.46, -138.43) * mm});
            skLineSegment(sketch, "E105.2.0.1", {"start": v(42.86, -118.03) * mm, "end": v(22.46, -118.03) * mm});
            skLineSegment(sketch, "E105.2.0.2", {"start": v(42.86, -138.43) * mm, "end": v(42.86, -118.03) * mm});
            skLineSegment(sketch, "E105.2.0.3", {"start": v(22.46, -138.43) * mm, "end": v(22.46, -118.03) * mm});
            skLineSegment(sketch, "E105.direction1", {"start": v(-31.54, -138.43) * mm, "end": v(-4.54, -138.43) * mm, "construction": true});
            skLineSegment(sketch, "E106.1.0.0", {"start": v(-4.54, -161.43) * mm, "end": v(-4.54, -141.03) * mm});
            skLineSegment(sketch, "E106.1.0.1", {"start": v(15.86, -161.43) * mm, "end": v(15.86, -141.03) * mm});
            skLineSegment(sketch, "E106.1.0.2", {"start": v(15.86, -141.03) * mm, "end": v(-4.54, -141.03) * mm});
            skLineSegment(sketch, "E106.1.0.3", {"start": v(15.86, -161.43) * mm, "end": v(-4.54, -161.43) * mm});
            skLineSegment(sketch, "E106.2.0.0", {"start": v(22.46, -161.43) * mm, "end": v(22.46, -141.03) * mm});
            skLineSegment(sketch, "E106.2.0.1", {"start": v(42.86, -161.43) * mm, "end": v(42.86, -141.03) * mm});
            skLineSegment(sketch, "E106.2.0.2", {"start": v(42.86, -141.03) * mm, "end": v(22.46, -141.03) * mm});
            skLineSegment(sketch, "E106.2.0.3", {"start": v(42.86, -161.43) * mm, "end": v(22.46, -161.43) * mm});
            skLineSegment(sketch, "E106.direction1", {"start": v(-31.54, -161.43) * mm, "end": v(-4.54, -161.43) * mm, "construction": true});
            skPoint(sketch, "E107", {"position": v(32.66, -151.23) * mm});
            skPoint(sketch, "E107.positionSnap0", {"position": v(32.66, -141.03) * mm});
            skPoint(sketch, "E107.positionSnap1", {"position": v(22.46, -151.23) * mm});
            skPoint(sketch, "E108", {"position": v(32.66, -128.23) * mm});
            skPoint(sketch, "E108.positionSnap0", {"position": v(32.66, -118.03) * mm});
            skPoint(sketch, "E108.positionSnap1", {"position": v(42.86, -128.23) * mm});
            skCircle(sketch, "E109", {"center": v(-41.84, -174.23) * mm, "radius": 6.25 * mm});
            skCircle(sketch, "E110", {"center": v(-41.84, -151.23) * mm, "radius": 5 * mm});
            skLineSegment(sketch, "E111.bottom", {"start": v(-40.84, -156.13) * mm, "end": v(-42.84, -156.13) * mm});
            skLineSegment(sketch, "E111.top", {"start": v(-40.84, -146.33) * mm, "end": v(-42.84, -146.33) * mm});
            skLineSegment(sketch, "E111.left", {"start": v(-40.84, -156.13) * mm, "end": v(-40.84, -146.33) * mm});
            skLineSegment(sketch, "E111.right", {"start": v(-42.84, -156.13) * mm, "end": v(-42.84, -146.33) * mm});
            skLineSegment(sketch, "E112", {"start": v(-61.34, -98.05) * mm, "end": v(-61.34, -82.14) * mm, "construction": true});
            skSolve(sketch);
        }
        {
            var Q0;
            Q0=makeQuery(id+"F0.imprint","IMPRINT",FACE,{"disambiguationData":[TD([[makeQuery(id+"F0.imprint","IMPRINT",EDGE,{"derivedFrom":sQuery(id+"F0.wireOp",EDGE,"E0.bottom")}),-1.0]])]});
            var Q1;
            Q1=makeQuery(id+"F0.imprint","IMPRINT",FACE,{"disambiguationData":[TD([[makeQuery(id+"F0.imprint","IMPRINT",EDGE,{"derivedFrom":sQuery(id+"F0.wireOp",EDGE,"E20.bottom")}),-1.0]])]});
            var Q2;
            Q2=makeQuery(id+"F0.imprint","IMPRINT",FACE,{"disambiguationData":[TD([[makeQuery(id+"F0.imprint","IMPRINT",EDGE,{"derivedFrom":sQuery(id+"F0.wireOp",EDGE,"E31.bottom")}),-1.0]])]});
            var Q3;
            Q3=makeQuery(id+"F0.imprint","IMPRINT",FACE,{"disambiguationData":[TD([[makeQuery(id+"F0.imprint","IMPRINT",EDGE,{"derivedFrom":sQuery(id+"F0.wireOp",EDGE,"7093700b-8509-4908-bad7-ce82e1b1d340.1.0.0")}),-1.0]])]});
            var Q4;
            Q4=makeQuery(id+"F0.imprint","IMPRINT",FACE,{"disambiguationData":[TD([[makeQuery(id+"F0.imprint","IMPRINT",EDGE,{"derivedFrom":sQuery(id+"F0.wireOp",EDGE,"7093700b-8509-4908-bad7-ce82e1b1d340.2.0.0")}),-1.0]])]});
            var Q5;
            {var subQ3=sQuery(id+"F0.wireOp",EDGE,"c973f7c2-3bf7-4545-afce-7af64f458de9.2.0.0");Q5=makeQuery(id+"F0.imprint","IMPRINT",FACE,{"disambiguationData":[TD([[makeQuery(id+"F0.imprint","IMPRINT",EDGE,{"derivedFrom":subQ3}),1.0]])]});}
            var Q6;
            {var subQ3=sQuery(id+"F0.wireOp",EDGE,"c973f7c2-3bf7-4545-afce-7af64f458de9.1.0.0");Q6=makeQuery(id+"F0.imprint","IMPRINT",FACE,{"disambiguationData":[TD([[makeQuery(id+"F0.imprint","IMPRINT",EDGE,{"derivedFrom":subQ3}),1.0]])]});}
            var Q7;
            Q7=makeQuery(id+"F0.imprint","IMPRINT",FACE,{"disambiguationData":[TD([[makeQuery(id+"F0.imprint","IMPRINT",EDGE,{"derivedFrom":sQuery(id+"F0.wireOp",EDGE,"E44.bottom")}),-1.0]])]});
            var Q8;
            Q8=makeQuery(id+"F0.imprint","IMPRINT",FACE,{"disambiguationData":[TD([[makeQuery(id+"F0.imprint","IMPRINT",EDGE,{"derivedFrom":sQuery(id+"F0.wireOp",EDGE,"E45.bottom")}),-1.0]])]});
            var Q9;
            {var subQ0=sQuery(id+"F0.wireOp",EDGE,"E44.left");Q9=makeQuery(id+"F0.imprint","IMPRINT",FACE,{"disambiguationData":[TD([[makeQuery(id+"F0.imprint","IMPRINT",EDGE,{"derivedFrom":subQ0}),1.0]])]});}
            var Q10;
            {var subQ0=sQuery(id+"F0.wireOp",EDGE,"E45.left");Q10=makeQuery(id+"F0.imprint","IMPRINT",FACE,{"disambiguationData":[TD([[makeQuery(id+"F0.imprint","IMPRINT",EDGE,{"derivedFrom":subQ0}),1.0]])]});}
            var Q11;
            Q11=makeQuery(id+"F0.imprint","IMPRINT",FACE,{"disambiguationData":[TD([[makeQuery(id+"F0.imprint","IMPRINT",EDGE,{"derivedFrom":sQuery(id+"F0.wireOp",EDGE,"E50.1.0.0")}),1.0]])]});
            var Q12;
            Q12=makeQuery(id+"F0.imprint","IMPRINT",FACE,{"disambiguationData":[TD([[makeQuery(id+"F0.imprint","IMPRINT",EDGE,{"derivedFrom":sQuery(id+"F0.wireOp",EDGE,"E50.1.0.1")}),-1.0]])]});
            var Q13;
            Q13=makeQuery(id+"F0.imprint","IMPRINT",FACE,{"disambiguationData":[TD([[makeQuery(id+"F0.imprint","IMPRINT",EDGE,{"derivedFrom":sQuery(id+"F0.wireOp",EDGE,"E50.2.0.0")}),1.0]])]});
            var Q14;
            Q14=makeQuery(id+"F0.imprint","IMPRINT",FACE,{"disambiguationData":[TD([[makeQuery(id+"F0.imprint","IMPRINT",EDGE,{"derivedFrom":sQuery(id+"F0.wireOp",EDGE,"E50.2.0.1")}),-1.0]])]});
            var Q15;
            Q15=makeQuery(id+"F0.imprint","IMPRINT",FACE,{"disambiguationData":[TD([[makeQuery(id+"F0.imprint","IMPRINT",EDGE,{"derivedFrom":sQuery(id+"F0.wireOp",EDGE,"E53.bottom")}),-1.0]])]});
            var Q16;
            Q16=makeQuery(id+"F0.imprint","IMPRINT",FACE,{"disambiguationData":[TD([[makeQuery(id+"F0.imprint","IMPRINT",EDGE,{"derivedFrom":sQuery(id+"F0.wireOp",EDGE,"E55.bottom")}),-1.0]])]});
            extrude(context, id + "F2", {"entities" : qUnion([Q0, Q1, Q2, Q3, Q4, Q5, Q6, Q7, Q8, Q9, Q10, Q11, Q12, Q13, Q14, Q15, Q16]), "depth" : 1 * mm});
        }
        {
            var Q0;
            Q0=makeQuery(id+"F2.opExtrude","CAP_FACE",FACE,{"disambiguationData":[OSD([sQuery(id+"F0.wireOp",EDGE,"E0.bottom"),sQuery(id+"F0.wireOp",EDGE,"E0.top"),sQuery(id+"F0.wireOp",EDGE,"E0.left"),sQuery(id+"F0.wireOp",EDGE,"E0.right"),sQuery(id+"F0.wireOp",EDGE,"6XQCNLW2-68Wz-nC9p-wT4x-b90YEvEmSNLj"),sQuery(id+"F0.wireOp",EDGE,"E3"),sQuery(id+"F0.wireOp",EDGE,"E4"),sQuery(id+"F0.wireOp",EDGE,"E7"),sQuery(id+"F0.wireOp",EDGE,"E8"),sQuery(id+"F0.wireOp",EDGE,"E9"),sQuery(id+"F0.wireOp",EDGE,"E10"),sQuery(id+"F0.wireOp",EDGE,"E11"),sQuery(id+"F0.wireOp",EDGE,"E12"),sQuery(id+"F0.wireOp",EDGE,"E13"),sQuery(id+"F0.wireOp",EDGE,"E14.bottom"),sQuery(id+"F0.wireOp",EDGE,"E14.top"),sQuery(id+"F0.wireOp",EDGE,"E14.left"),sQuery(id+"F0.wireOp",EDGE,"E14.right"),sQuery(id+"F0.wireOp",EDGE,"E15"),sQuery(id+"F0.wireOp",EDGE,"E16"),sQuery(id+"F0.wireOp",EDGE,"E18.bottom"),sQuery(id+"F0.wireOp",EDGE,"E18.top"),sQuery(id+"F0.wireOp",EDGE,"E18.left"),sQuery(id+"F0.wireOp",EDGE,"E18.right"),sQuery(id+"F0.wireOp",EDGE,"E20.bottom"),sQuery(id+"F0.wireOp",EDGE,"E20.top"),sQuery(id+"F0.wireOp",EDGE,"E21.left"),sQuery(id+"F0.wireOp",EDGE,"E21.right"),sQuery(id+"F0.wireOp",EDGE,"E22.left"),sQuery(id+"F0.wireOp",EDGE,"E22.right"),sQuery(id+"F0.wireOp",EDGE,"E23.trimOffspring"),sQuery(id+"F0.wireOp",EDGE,"E24.trimOffspring"),sQuery(id+"F0.wireOp",EDGE,"E25.trimOffspring"),sQuery(id+"F0.wireOp",EDGE,"E26.trimOffspring"),sQuery(id+"F0.wireOp",EDGE,"E27.trimOffspring"),sQuery(id+"F0.wireOp",EDGE,"E28.trimOffspring"),sQuery(id+"F0.wireOp",EDGE,"E29.trimOffspring"),sQuery(id+"F0.wireOp",EDGE,"E30.trimOffspring"),sQuery(id+"F0.wireOp",EDGE,"E19.bottom"),sQuery(id+"F0.wireOp",EDGE,"E19.top"),sQuery(id+"F0.wireOp",EDGE,"E19.left"),sQuery(id+"F0.wireOp",EDGE,"E19.right"),sQuery(id+"F0.wireOp",EDGE,"E31.bottom"),sQuery(id+"F0.wireOp",EDGE,"E31.top"),sQuery(id+"F0.wireOp",EDGE,"E32.left"),sQuery(id+"F0.wireOp",EDGE,"E32.right"),sQuery(id+"F0.wireOp",EDGE,"E33.left"),sQuery(id+"F0.wireOp",EDGE,"E33.right"),sQuery(id+"F0.wireOp",EDGE,"E34.trimOffspring"),sQuery(id+"F0.wireOp",EDGE,"E35.trimOffspring"),sQuery(id+"F0.wireOp",EDGE,"E36.trimOffspring"),sQuery(id+"F0.wireOp",EDGE,"E37.trimOffspring"),sQuery(id+"F0.wireOp",EDGE,"E38.trimOffspring"),sQuery(id+"F0.wireOp",EDGE,"E39.trimOffspring"),sQuery(id+"F0.wireOp",EDGE,"E40.trimOffspring"),sQuery(id+"F0.wireOp",EDGE,"E41.trimOffspring"),sQuery(id+"F0.wireOp",EDGE,"E42.bottom"),sQuery(id+"F0.wireOp",EDGE,"E42.top"),sQuery(id+"F0.wireOp",EDGE,"E42.left"),sQuery(id+"F0.wireOp",EDGE,"E42.right"),sQuery(id+"F0.wireOp",EDGE,"E43.bottom"),sQuery(id+"F0.wireOp",EDGE,"E43.top"),sQuery(id+"F0.wireOp",EDGE,"E43.left"),sQuery(id+"F0.wireOp",EDGE,"E43.right"),sQuery(id+"F0.wireOp",EDGE,"7093700b-8509-4908-bad7-ce82e1b1d340.1.0.0"),sQuery(id+"F0.wireOp",EDGE,"7093700b-8509-4908-bad7-ce82e1b1d340.1.0.2"),sQuery(id+"F0.wireOp",EDGE,"7093700b-8509-4908-bad7-ce82e1b1d340.1.0.3"),sQuery(id+"F0.wireOp",EDGE,"7093700b-8509-4908-bad7-ce82e1b1d340.1.0.5"),sQuery(id+"F0.wireOp",EDGE,"7093700b-8509-4908-bad7-ce82e1b1d340.1.0.6"),sQuery(id+"F0.wireOp",EDGE,"7093700b-8509-4908-bad7-ce82e1b1d340.1.0.7"),sQuery(id+"F0.wireOp",EDGE,"7093700b-8509-4908-bad7-ce82e1b1d340.1.0.8"),sQuery(id+"F0.wireOp",EDGE,"7093700b-8509-4908-bad7-ce82e1b1d340.1.0.9"),sQuery(id+"F0.wireOp",EDGE,"7093700b-8509-4908-bad7-ce82e1b1d340.1.0.12"),sQuery(id+"F0.wireOp",EDGE,"7093700b-8509-4908-bad7-ce82e1b1d340.1.0.13"),sQuery(id+"F0.wireOp",EDGE,"7093700b-8509-4908-bad7-ce82e1b1d340.1.0.14"),sQuery(id+"F0.wireOp",EDGE,"7093700b-8509-4908-bad7-ce82e1b1d340.1.0.15"),sQuery(id+"F0.wireOp",EDGE,"7093700b-8509-4908-bad7-ce82e1b1d340.1.0.16"),sQuery(id+"F0.wireOp",EDGE,"7093700b-8509-4908-bad7-ce82e1b1d340.1.0.17"),sQuery(id+"F0.wireOp",EDGE,"7093700b-8509-4908-bad7-ce82e1b1d340.1.0.18"),sQuery(id+"F0.wireOp",EDGE,"7093700b-8509-4908-bad7-ce82e1b1d340.1.0.19"),sQuery(id+"F0.wireOp",EDGE,"7093700b-8509-4908-bad7-ce82e1b1d340.1.0.20"),sQuery(id+"F0.wireOp",EDGE,"7093700b-8509-4908-bad7-ce82e1b1d340.1.0.21"),sQuery(id+"F0.wireOp",EDGE,"7093700b-8509-4908-bad7-ce82e1b1d340.2.0.0"),sQuery(id+"F0.wireOp",EDGE,"7093700b-8509-4908-bad7-ce82e1b1d340.2.0.2"),sQuery(id+"F0.wireOp",EDGE,"7093700b-8509-4908-bad7-ce82e1b1d340.2.0.3"),sQuery(id+"F0.wireOp",EDGE,"7093700b-8509-4908-bad7-ce82e1b1d340.2.0.5"),sQuery(id+"F0.wireOp",EDGE,"7093700b-8509-4908-bad7-ce82e1b1d340.2.0.6"),sQuery(id+"F0.wireOp",EDGE,"7093700b-8509-4908-bad7-ce82e1b1d340.2.0.7"),sQuery(id+"F0.wireOp",EDGE,"7093700b-8509-4908-bad7-ce82e1b1d340.2.0.8"),sQuery(id+"F0.wireOp",EDGE,"7093700b-8509-4908-bad7-ce82e1b1d340.2.0.9"),sQuery(id+"F0.wireOp",EDGE,"7093700b-8509-4908-bad7-ce82e1b1d340.2.0.12"),sQuery(id+"F0.wireOp",EDGE,"7093700b-8509-4908-bad7-ce82e1b1d340.2.0.13"),sQuery(id+"F0.wireOp",EDGE,"7093700b-8509-4908-bad7-ce82e1b1d340.2.0.14"),sQuery(id+"F0.wireOp",EDGE,"7093700b-8509-4908-bad7-ce82e1b1d340.2.0.15"),sQuery(id+"F0.wireOp",EDGE,"7093700b-8509-4908-bad7-ce82e1b1d340.2.0.16"),sQuery(id+"F0.wireOp",EDGE,"7093700b-8509-4908-bad7-ce82e1b1d340.2.0.17"),sQuery(id+"F0.wireOp",EDGE,"7093700b-8509-4908-bad7-ce82e1b1d340.2.0.18"),sQuery(id+"F0.wireOp",EDGE,"7093700b-8509-4908-bad7-ce82e1b1d340.2.0.19"),sQuery(id+"F0.wireOp",EDGE,"7093700b-8509-4908-bad7-ce82e1b1d340.2.0.20"),sQuery(id+"F0.wireOp",EDGE,"7093700b-8509-4908-bad7-ce82e1b1d340.2.0.21"),sQuery(id+"F0.wireOp",EDGE,"c973f7c2-3bf7-4545-afce-7af64f458de9.1.0.0"),sQuery(id+"F0.wireOp",EDGE,"c973f7c2-3bf7-4545-afce-7af64f458de9.1.0.1"),sQuery(id+"F0.wireOp",EDGE,"c973f7c2-3bf7-4545-afce-7af64f458de9.1.0.2"),sQuery(id+"F0.wireOp",EDGE,"c973f7c2-3bf7-4545-afce-7af64f458de9.1.0.4"),sQuery(id+"F0.wireOp",EDGE,"c973f7c2-3bf7-4545-afce-7af64f458de9.1.0.6"),sQuery(id+"F0.wireOp",EDGE,"c973f7c2-3bf7-4545-afce-7af64f458de9.1.0.7"),sQuery(id+"F0.wireOp",EDGE,"c973f7c2-3bf7-4545-afce-7af64f458de9.1.0.9"),sQuery(id+"F0.wireOp",EDGE,"c973f7c2-3bf7-4545-afce-7af64f458de9.1.0.10"),sQuery(id+"F0.wireOp",EDGE,"c973f7c2-3bf7-4545-afce-7af64f458de9.1.0.12"),sQuery(id+"F0.wireOp",EDGE,"c973f7c2-3bf7-4545-afce-7af64f458de9.1.0.14"),sQuery(id+"F0.wireOp",EDGE,"c973f7c2-3bf7-4545-afce-7af64f458de9.1.0.16"),sQuery(id+"F0.wireOp",EDGE,"c973f7c2-3bf7-4545-afce-7af64f458de9.1.0.18"),sQuery(id+"F0.wireOp",EDGE,"c973f7c2-3bf7-4545-afce-7af64f458de9.1.0.19"),sQuery(id+"F0.wireOp",EDGE,"c973f7c2-3bf7-4545-afce-7af64f458de9.1.0.20"),sQuery(id+"F0.wireOp",EDGE,"c973f7c2-3bf7-4545-afce-7af64f458de9.1.0.26"),sQuery(id+"F0.wireOp",EDGE,"c973f7c2-3bf7-4545-afce-7af64f458de9.1.0.28"),sQuery(id+"F0.wireOp",EDGE,"c973f7c2-3bf7-4545-afce-7af64f458de9.1.0.29"),sQuery(id+"F0.wireOp",EDGE,"c973f7c2-3bf7-4545-afce-7af64f458de9.1.0.30"),sQuery(id+"F0.wireOp",EDGE,"c973f7c2-3bf7-4545-afce-7af64f458de9.2.0.0"),sQuery(id+"F0.wireOp",EDGE,"c973f7c2-3bf7-4545-afce-7af64f458de9.2.0.1"),sQuery(id+"F0.wireOp",EDGE,"c973f7c2-3bf7-4545-afce-7af64f458de9.2.0.2"),sQuery(id+"F0.wireOp",EDGE,"c973f7c2-3bf7-4545-afce-7af64f458de9.2.0.4"),sQuery(id+"F0.wireOp",EDGE,"c973f7c2-3bf7-4545-afce-7af64f458de9.2.0.6"),sQuery(id+"F0.wireOp",EDGE,"c973f7c2-3bf7-4545-afce-7af64f458de9.2.0.7"),sQuery(id+"F0.wireOp",EDGE,"c973f7c2-3bf7-4545-afce-7af64f458de9.2.0.9"),sQuery(id+"F0.wireOp",EDGE,"c973f7c2-3bf7-4545-afce-7af64f458de9.2.0.10"),sQuery(id+"F0.wireOp",EDGE,"c973f7c2-3bf7-4545-afce-7af64f458de9.2.0.12"),sQuery(id+"F0.wireOp",EDGE,"c973f7c2-3bf7-4545-afce-7af64f458de9.2.0.14"),sQuery(id+"F0.wireOp",EDGE,"c973f7c2-3bf7-4545-afce-7af64f458de9.2.0.16"),sQuery(id+"F0.wireOp",EDGE,"c973f7c2-3bf7-4545-afce-7af64f458de9.2.0.18"),sQuery(id+"F0.wireOp",EDGE,"c973f7c2-3bf7-4545-afce-7af64f458de9.2.0.19"),sQuery(id+"F0.wireOp",EDGE,"c973f7c2-3bf7-4545-afce-7af64f458de9.2.0.20"),sQuery(id+"F0.wireOp",EDGE,"c973f7c2-3bf7-4545-afce-7af64f458de9.2.0.26"),sQuery(id+"F0.wireOp",EDGE,"c973f7c2-3bf7-4545-afce-7af64f458de9.2.0.28"),sQuery(id+"F0.wireOp",EDGE,"c973f7c2-3bf7-4545-afce-7af64f458de9.2.0.29"),sQuery(id+"F0.wireOp",EDGE,"c973f7c2-3bf7-4545-afce-7af64f458de9.2.0.30")])],"isStart":false});
            var Q1;
            {var subQ0=sQuery(id+"F0.wireOp",EDGE,"rYwyOBXD-m5LK-rnKL-k3sO-ogXxKnliiuRN.left");Q1=makeQuery(id+"F0.imprint","IMPRINT",FACE,{"disambiguationData":[TD([[makeQuery(id+"F0.imprint","IMPRINT",EDGE,{"derivedFrom":subQ0}),1.0]])]});}
            var Q2;
            {var subQ0=sQuery(id+"F0.wireOp",EDGE,"PkneSYUR-leV3-Pqg6-8MYA-ygIsKwYRT98A.left");Q2=makeQuery(id+"F0.imprint","IMPRINT",FACE,{"disambiguationData":[TD([[makeQuery(id+"F0.imprint","IMPRINT",EDGE,{"derivedFrom":subQ0}),1.0]])]});}
            var Q3;
            {var subQ0=sQuery(id+"F0.wireOp",EDGE,"vsiTGSYA-5vz3-LSdH-l7PB-eDLQVEbj46oE.left");Q3=makeQuery(id+"F0.imprint","IMPRINT",FACE,{"disambiguationData":[TD([[makeQuery(id+"F0.imprint","IMPRINT",EDGE,{"derivedFrom":subQ0}),1.0]])]});}
            var Q4;
            {var subQ0=sQuery(id+"F0.wireOp",EDGE,"qxe8J46x-YBAU-1gLG-RRm6-GLdHy8YKuxwO.left");Q4=makeQuery(id+"F0.imprint","IMPRINT",FACE,{"disambiguationData":[TD([[makeQuery(id+"F0.imprint","IMPRINT",EDGE,{"derivedFrom":subQ0}),1.0]])]});}
            var Q5;
            Q5=makeQuery(id+"F0.imprint","IMPRINT",FACE,{"disambiguationData":[TD([[makeQuery(id+"F0.imprint","IMPRINT",EDGE,{"derivedFrom":sQuery(id+"F0.wireOp",EDGE,"E53.bottom")}),-1.0]])]});
            var Q6;
            Q6=makeQuery(id+"F0.imprint","IMPRINT",FACE,{"disambiguationData":[TD([[makeQuery(id+"F0.imprint","IMPRINT",EDGE,{"derivedFrom":sQuery(id+"F0.wireOp",EDGE,"E50.1.0.0")}),1.0]])]});
            var Q7;
            Q7=makeQuery(id+"F0.imprint","IMPRINT",FACE,{"disambiguationData":[TD([[makeQuery(id+"F0.imprint","IMPRINT",EDGE,{"derivedFrom":sQuery(id+"F0.wireOp",EDGE,"E50.1.0.1")}),-1.0]])]});
            var Q8;
            Q8=makeQuery(id+"F0.imprint","IMPRINT",FACE,{"disambiguationData":[TD([[makeQuery(id+"F0.imprint","IMPRINT",EDGE,{"derivedFrom":sQuery(id+"F0.wireOp",EDGE,"E50.2.0.1")}),-1.0]])]});
            var Q9;
            Q9=makeQuery(id+"F0.imprint","IMPRINT",FACE,{"disambiguationData":[TD([[makeQuery(id+"F0.imprint","IMPRINT",EDGE,{"derivedFrom":sQuery(id+"F0.wireOp",EDGE,"E50.2.0.0")}),1.0]])]});
            extrude(context, id + "F3", {"entities" : qUnion([Q0, Q1, Q2, Q3, Q4, Q5, Q6, Q7, Q8, Q9]), "operationType" : NewBodyOperationType.ADD, "depth" : 5 * mm});
        }
        {
            var Q0;
            Q0=makeQuery(id+"F3.opExtrude","CAP_FACE",FACE,{"disambiguationData":[OSD([sQuery(id+"F0.wireOp",EDGE,"E0.bottom"),sQuery(id+"F0.wireOp",EDGE,"E0.top"),sQuery(id+"F0.wireOp",EDGE,"E0.left"),sQuery(id+"F0.wireOp",EDGE,"E0.right"),sQuery(id+"F0.wireOp",EDGE,"6XQCNLW2-68Wz-nC9p-wT4x-b90YEvEmSNLj"),sQuery(id+"F0.wireOp",EDGE,"E3"),sQuery(id+"F0.wireOp",EDGE,"E4"),sQuery(id+"F0.wireOp",EDGE,"E7"),sQuery(id+"F0.wireOp",EDGE,"E8"),sQuery(id+"F0.wireOp",EDGE,"E9"),sQuery(id+"F0.wireOp",EDGE,"E10"),sQuery(id+"F0.wireOp",EDGE,"E11"),sQuery(id+"F0.wireOp",EDGE,"E12"),sQuery(id+"F0.wireOp",EDGE,"E13"),sQuery(id+"F0.wireOp",EDGE,"E14.bottom"),sQuery(id+"F0.wireOp",EDGE,"E14.top"),sQuery(id+"F0.wireOp",EDGE,"E14.left"),sQuery(id+"F0.wireOp",EDGE,"E14.right"),sQuery(id+"F0.wireOp",EDGE,"E15"),sQuery(id+"F0.wireOp",EDGE,"E16"),sQuery(id+"F0.wireOp",EDGE,"E18.bottom"),sQuery(id+"F0.wireOp",EDGE,"E18.top"),sQuery(id+"F0.wireOp",EDGE,"E18.left"),sQuery(id+"F0.wireOp",EDGE,"E18.right"),sQuery(id+"F0.wireOp",EDGE,"E20.bottom"),sQuery(id+"F0.wireOp",EDGE,"E20.top"),sQuery(id+"F0.wireOp",EDGE,"E21.left"),sQuery(id+"F0.wireOp",EDGE,"E21.right"),sQuery(id+"F0.wireOp",EDGE,"E22.left"),sQuery(id+"F0.wireOp",EDGE,"E22.right"),sQuery(id+"F0.wireOp",EDGE,"E23.trimOffspring"),sQuery(id+"F0.wireOp",EDGE,"E24.trimOffspring"),sQuery(id+"F0.wireOp",EDGE,"E25.trimOffspring"),sQuery(id+"F0.wireOp",EDGE,"E26.trimOffspring"),sQuery(id+"F0.wireOp",EDGE,"E27.trimOffspring"),sQuery(id+"F0.wireOp",EDGE,"E28.trimOffspring"),sQuery(id+"F0.wireOp",EDGE,"E29.trimOffspring"),sQuery(id+"F0.wireOp",EDGE,"E30.trimOffspring"),sQuery(id+"F0.wireOp",EDGE,"E19.bottom"),sQuery(id+"F0.wireOp",EDGE,"E19.top"),sQuery(id+"F0.wireOp",EDGE,"E19.left"),sQuery(id+"F0.wireOp",EDGE,"E19.right"),sQuery(id+"F0.wireOp",EDGE,"E31.bottom"),sQuery(id+"F0.wireOp",EDGE,"E31.top"),sQuery(id+"F0.wireOp",EDGE,"E32.left"),sQuery(id+"F0.wireOp",EDGE,"E32.right"),sQuery(id+"F0.wireOp",EDGE,"E33.left"),sQuery(id+"F0.wireOp",EDGE,"E33.right"),sQuery(id+"F0.wireOp",EDGE,"E34.trimOffspring"),sQuery(id+"F0.wireOp",EDGE,"E35.trimOffspring"),sQuery(id+"F0.wireOp",EDGE,"E36.trimOffspring"),sQuery(id+"F0.wireOp",EDGE,"E37.trimOffspring"),sQuery(id+"F0.wireOp",EDGE,"E38.trimOffspring"),sQuery(id+"F0.wireOp",EDGE,"E39.trimOffspring"),sQuery(id+"F0.wireOp",EDGE,"E40.trimOffspring"),sQuery(id+"F0.wireOp",EDGE,"E41.trimOffspring"),sQuery(id+"F0.wireOp",EDGE,"E42.bottom"),sQuery(id+"F0.wireOp",EDGE,"E42.top"),sQuery(id+"F0.wireOp",EDGE,"E42.left"),sQuery(id+"F0.wireOp",EDGE,"E42.right"),sQuery(id+"F0.wireOp",EDGE,"E43.bottom"),sQuery(id+"F0.wireOp",EDGE,"E43.top"),sQuery(id+"F0.wireOp",EDGE,"E43.left"),sQuery(id+"F0.wireOp",EDGE,"E43.right"),sQuery(id+"F0.wireOp",EDGE,"7093700b-8509-4908-bad7-ce82e1b1d340.1.0.0"),sQuery(id+"F0.wireOp",EDGE,"7093700b-8509-4908-bad7-ce82e1b1d340.1.0.2"),sQuery(id+"F0.wireOp",EDGE,"7093700b-8509-4908-bad7-ce82e1b1d340.1.0.3"),sQuery(id+"F0.wireOp",EDGE,"7093700b-8509-4908-bad7-ce82e1b1d340.1.0.5"),sQuery(id+"F0.wireOp",EDGE,"7093700b-8509-4908-bad7-ce82e1b1d340.1.0.6"),sQuery(id+"F0.wireOp",EDGE,"7093700b-8509-4908-bad7-ce82e1b1d340.1.0.7"),sQuery(id+"F0.wireOp",EDGE,"7093700b-8509-4908-bad7-ce82e1b1d340.1.0.8"),sQuery(id+"F0.wireOp",EDGE,"7093700b-8509-4908-bad7-ce82e1b1d340.1.0.9"),sQuery(id+"F0.wireOp",EDGE,"7093700b-8509-4908-bad7-ce82e1b1d340.1.0.12"),sQuery(id+"F0.wireOp",EDGE,"7093700b-8509-4908-bad7-ce82e1b1d340.1.0.13"),sQuery(id+"F0.wireOp",EDGE,"7093700b-8509-4908-bad7-ce82e1b1d340.1.0.14"),sQuery(id+"F0.wireOp",EDGE,"7093700b-8509-4908-bad7-ce82e1b1d340.1.0.15"),sQuery(id+"F0.wireOp",EDGE,"7093700b-8509-4908-bad7-ce82e1b1d340.1.0.16"),sQuery(id+"F0.wireOp",EDGE,"7093700b-8509-4908-bad7-ce82e1b1d340.1.0.17"),sQuery(id+"F0.wireOp",EDGE,"7093700b-8509-4908-bad7-ce82e1b1d340.1.0.18"),sQuery(id+"F0.wireOp",EDGE,"7093700b-8509-4908-bad7-ce82e1b1d340.1.0.19"),sQuery(id+"F0.wireOp",EDGE,"7093700b-8509-4908-bad7-ce82e1b1d340.1.0.20"),sQuery(id+"F0.wireOp",EDGE,"7093700b-8509-4908-bad7-ce82e1b1d340.1.0.21"),sQuery(id+"F0.wireOp",EDGE,"7093700b-8509-4908-bad7-ce82e1b1d340.2.0.0"),sQuery(id+"F0.wireOp",EDGE,"7093700b-8509-4908-bad7-ce82e1b1d340.2.0.2"),sQuery(id+"F0.wireOp",EDGE,"7093700b-8509-4908-bad7-ce82e1b1d340.2.0.3"),sQuery(id+"F0.wireOp",EDGE,"7093700b-8509-4908-bad7-ce82e1b1d340.2.0.5"),sQuery(id+"F0.wireOp",EDGE,"7093700b-8509-4908-bad7-ce82e1b1d340.2.0.6"),sQuery(id+"F0.wireOp",EDGE,"7093700b-8509-4908-bad7-ce82e1b1d340.2.0.7"),sQuery(id+"F0.wireOp",EDGE,"7093700b-8509-4908-bad7-ce82e1b1d340.2.0.8"),sQuery(id+"F0.wireOp",EDGE,"7093700b-8509-4908-bad7-ce82e1b1d340.2.0.9"),sQuery(id+"F0.wireOp",EDGE,"7093700b-8509-4908-bad7-ce82e1b1d340.2.0.12"),sQuery(id+"F0.wireOp",EDGE,"7093700b-8509-4908-bad7-ce82e1b1d340.2.0.13"),sQuery(id+"F0.wireOp",EDGE,"7093700b-8509-4908-bad7-ce82e1b1d340.2.0.14"),sQuery(id+"F0.wireOp",EDGE,"7093700b-8509-4908-bad7-ce82e1b1d340.2.0.15"),sQuery(id+"F0.wireOp",EDGE,"7093700b-8509-4908-bad7-ce82e1b1d340.2.0.16"),sQuery(id+"F0.wireOp",EDGE,"7093700b-8509-4908-bad7-ce82e1b1d340.2.0.17"),sQuery(id+"F0.wireOp",EDGE,"7093700b-8509-4908-bad7-ce82e1b1d340.2.0.18"),sQuery(id+"F0.wireOp",EDGE,"7093700b-8509-4908-bad7-ce82e1b1d340.2.0.19"),sQuery(id+"F0.wireOp",EDGE,"7093700b-8509-4908-bad7-ce82e1b1d340.2.0.20"),sQuery(id+"F0.wireOp",EDGE,"7093700b-8509-4908-bad7-ce82e1b1d340.2.0.21"),sQuery(id+"F0.wireOp",EDGE,"c973f7c2-3bf7-4545-afce-7af64f458de9.1.0.0"),sQuery(id+"F0.wireOp",EDGE,"c973f7c2-3bf7-4545-afce-7af64f458de9.1.0.1"),sQuery(id+"F0.wireOp",EDGE,"c973f7c2-3bf7-4545-afce-7af64f458de9.1.0.2"),sQuery(id+"F0.wireOp",EDGE,"c973f7c2-3bf7-4545-afce-7af64f458de9.1.0.4"),sQuery(id+"F0.wireOp",EDGE,"c973f7c2-3bf7-4545-afce-7af64f458de9.1.0.6"),sQuery(id+"F0.wireOp",EDGE,"c973f7c2-3bf7-4545-afce-7af64f458de9.1.0.7"),sQuery(id+"F0.wireOp",EDGE,"c973f7c2-3bf7-4545-afce-7af64f458de9.1.0.9"),sQuery(id+"F0.wireOp",EDGE,"c973f7c2-3bf7-4545-afce-7af64f458de9.1.0.10"),sQuery(id+"F0.wireOp",EDGE,"c973f7c2-3bf7-4545-afce-7af64f458de9.1.0.12"),sQuery(id+"F0.wireOp",EDGE,"c973f7c2-3bf7-4545-afce-7af64f458de9.1.0.14"),sQuery(id+"F0.wireOp",EDGE,"c973f7c2-3bf7-4545-afce-7af64f458de9.1.0.16"),sQuery(id+"F0.wireOp",EDGE,"c973f7c2-3bf7-4545-afce-7af64f458de9.1.0.18"),sQuery(id+"F0.wireOp",EDGE,"c973f7c2-3bf7-4545-afce-7af64f458de9.1.0.19"),sQuery(id+"F0.wireOp",EDGE,"c973f7c2-3bf7-4545-afce-7af64f458de9.1.0.20"),sQuery(id+"F0.wireOp",EDGE,"c973f7c2-3bf7-4545-afce-7af64f458de9.1.0.26"),sQuery(id+"F0.wireOp",EDGE,"c973f7c2-3bf7-4545-afce-7af64f458de9.1.0.28"),sQuery(id+"F0.wireOp",EDGE,"c973f7c2-3bf7-4545-afce-7af64f458de9.1.0.29"),sQuery(id+"F0.wireOp",EDGE,"c973f7c2-3bf7-4545-afce-7af64f458de9.1.0.30"),sQuery(id+"F0.wireOp",EDGE,"c973f7c2-3bf7-4545-afce-7af64f458de9.2.0.0"),sQuery(id+"F0.wireOp",EDGE,"c973f7c2-3bf7-4545-afce-7af64f458de9.2.0.1"),sQuery(id+"F0.wireOp",EDGE,"c973f7c2-3bf7-4545-afce-7af64f458de9.2.0.2"),sQuery(id+"F0.wireOp",EDGE,"c973f7c2-3bf7-4545-afce-7af64f458de9.2.0.4"),sQuery(id+"F0.wireOp",EDGE,"c973f7c2-3bf7-4545-afce-7af64f458de9.2.0.6"),sQuery(id+"F0.wireOp",EDGE,"c973f7c2-3bf7-4545-afce-7af64f458de9.2.0.7"),sQuery(id+"F0.wireOp",EDGE,"c973f7c2-3bf7-4545-afce-7af64f458de9.2.0.9"),sQuery(id+"F0.wireOp",EDGE,"c973f7c2-3bf7-4545-afce-7af64f458de9.2.0.10"),sQuery(id+"F0.wireOp",EDGE,"c973f7c2-3bf7-4545-afce-7af64f458de9.2.0.12"),sQuery(id+"F0.wireOp",EDGE,"c973f7c2-3bf7-4545-afce-7af64f458de9.2.0.14"),sQuery(id+"F0.wireOp",EDGE,"c973f7c2-3bf7-4545-afce-7af64f458de9.2.0.16"),sQuery(id+"F0.wireOp",EDGE,"c973f7c2-3bf7-4545-afce-7af64f458de9.2.0.18"),sQuery(id+"F0.wireOp",EDGE,"c973f7c2-3bf7-4545-afce-7af64f458de9.2.0.19"),sQuery(id+"F0.wireOp",EDGE,"c973f7c2-3bf7-4545-afce-7af64f458de9.2.0.20"),sQuery(id+"F0.wireOp",EDGE,"c973f7c2-3bf7-4545-afce-7af64f458de9.2.0.26"),sQuery(id+"F0.wireOp",EDGE,"c973f7c2-3bf7-4545-afce-7af64f458de9.2.0.28"),sQuery(id+"F0.wireOp",EDGE,"c973f7c2-3bf7-4545-afce-7af64f458de9.2.0.29"),sQuery(id+"F0.wireOp",EDGE,"c973f7c2-3bf7-4545-afce-7af64f458de9.2.0.30")])],"isStart":false});
            var sketch = newSketch(context, id + "F4", { "sketchPlane" : qUnion([Q0])});
            skPoint(sketch, "E113.0", {"position": v(-109.5, 1.96) * mm});
            skLineSegment(sketch, "E114.bottom", {"start": v(-100.5, -7.04) * mm, "end": v(-118.5, -7.04) * mm});
            skLineSegment(sketch, "E114.top", {"start": v(-100.5, 10.96) * mm, "end": v(-118.5, 10.96) * mm});
            skLineSegment(sketch, "E114.left", {"start": v(-100.5, -7.04) * mm, "end": v(-100.5, 10.96) * mm});
            skLineSegment(sketch, "E114.right", {"start": v(-118.5, -7.04) * mm, "end": v(-118.5, 10.96) * mm});
            skPoint(sketch, "E115.0", {"position": v(-109.5, -21.04) * mm});
            skLineSegment(sketch, "E116.bottom", {"start": v(-100.5, -30.04) * mm, "end": v(-118.5, -30.04) * mm});
            skLineSegment(sketch, "E116.top", {"start": v(-100.5, -12.04) * mm, "end": v(-118.5, -12.04) * mm});
            skLineSegment(sketch, "E116.left", {"start": v(-100.5, -30.04) * mm, "end": v(-100.5, -12.04) * mm});
            skLineSegment(sketch, "E116.right", {"start": v(-118.5, -30.04) * mm, "end": v(-118.5, -12.04) * mm});
            skPoint(sketch, "E117.0", {"position": v(-119.5, -21.04) * mm});
            skPoint(sketch, "E117.1", {"position": v(-119.5, 1.96) * mm});
            skLineSegment(sketch, "E118.bottom", {"start": v(-118.5, -5.54) * mm, "end": v(-120.5, -5.54) * mm});
            skLineSegment(sketch, "E118.top", {"start": v(-118.5, 9.46) * mm, "end": v(-120.5, 9.46) * mm});
            skLineSegment(sketch, "E118.left", {"start": v(-118.5, -5.54) * mm, "end": v(-118.5, 9.46) * mm});
            skLineSegment(sketch, "E118.right", {"start": v(-120.5, -5.54) * mm, "end": v(-120.5, 9.46) * mm});
            skPoint(sketch, "E119.0", {"position": v(-99.5, 1.96) * mm});
            skLineSegment(sketch, "E120.bottom", {"start": v(-100.5, -5.54) * mm, "end": v(-98.5, -5.54) * mm});
            skLineSegment(sketch, "E120.top", {"start": v(-100.5, 9.46) * mm, "end": v(-98.5, 9.46) * mm});
            skLineSegment(sketch, "E120.left", {"start": v(-100.5, -5.54) * mm, "end": v(-100.5, 9.46) * mm});
            skLineSegment(sketch, "E120.right", {"start": v(-98.5, -5.54) * mm, "end": v(-98.5, 9.46) * mm});
            skPoint(sketch, "E121.0", {"position": v(-99.5, -21.04) * mm});
            skPoint(sketch, "E122.0", {"position": v(-130, 1.96) * mm});
            skPoint(sketch, "E122.1", {"position": v(-130, -21.04) * mm});
            skCircle(sketch, "E123", {"center": v(-130, 1.96) * mm, "radius": 5 * mm});
            skCircle(sketch, "E124", {"center": v(-130, -21.04) * mm, "radius": 5 * mm});
            skLineSegment(sketch, "E125.bottom", {"start": v(-118.5, -28.54) * mm, "end": v(-120.5, -28.54) * mm});
            skLineSegment(sketch, "E125.top", {"start": v(-118.5, -13.54) * mm, "end": v(-120.5, -13.54) * mm});
            skLineSegment(sketch, "E125.left", {"start": v(-118.5, -28.54) * mm, "end": v(-118.5, -13.54) * mm});
            skLineSegment(sketch, "E125.right", {"start": v(-120.5, -28.54) * mm, "end": v(-120.5, -13.54) * mm});
            skLineSegment(sketch, "E126.bottom", {"start": v(-98.5, -28.54) * mm, "end": v(-100.5, -28.54) * mm});
            skLineSegment(sketch, "E126.top", {"start": v(-98.5, -13.54) * mm, "end": v(-100.5, -13.54) * mm});
            skLineSegment(sketch, "E126.left", {"start": v(-98.5, -28.54) * mm, "end": v(-98.5, -13.54) * mm});
            skLineSegment(sketch, "E126.right", {"start": v(-100.5, -28.54) * mm, "end": v(-100.5, -13.54) * mm});
            skLineSegment(sketch, "E127.1.0.0", {"start": v(-91.5, -5.54) * mm, "end": v(-93.5, -5.54) * mm});
            skLineSegment(sketch, "E127.1.0.1", {"start": v(-91.5, 9.46) * mm, "end": v(-93.5, 9.46) * mm});
            skLineSegment(sketch, "E127.1.0.2", {"start": v(-73.5, 9.46) * mm, "end": v(-71.5, 9.46) * mm});
            skPoint(sketch, "E127.1.0.3", {"position": v(-82.5, 1.96) * mm});
            skLineSegment(sketch, "E127.1.0.4", {"start": v(-73.5, -5.54) * mm, "end": v(-71.5, -5.54) * mm});
            skPoint(sketch, "E127.1.0.5", {"position": v(-72.5, 1.96) * mm});
            skLineSegment(sketch, "E127.1.0.6", {"start": v(-71.5, -5.54) * mm, "end": v(-71.5, 9.46) * mm});
            skLineSegment(sketch, "E127.1.0.7", {"start": v(-91.5, -7.04) * mm, "end": v(-91.5, 10.96) * mm});
            skPoint(sketch, "E127.1.0.8", {"position": v(-92.5, 1.96) * mm});
            skLineSegment(sketch, "E127.1.0.9", {"start": v(-73.5, 10.96) * mm, "end": v(-91.5, 10.96) * mm});
            skLineSegment(sketch, "E127.1.0.10", {"start": v(-73.5, -7.04) * mm, "end": v(-91.5, -7.04) * mm});
            skLineSegment(sketch, "E127.1.0.11", {"start": v(-93.5, -5.54) * mm, "end": v(-93.5, 9.46) * mm});
            skLineSegment(sketch, "E127.1.0.12", {"start": v(-73.5, -7.04) * mm, "end": v(-73.5, 10.96) * mm});
            skPoint(sketch, "E127.1.0.13", {"position": v(-92.5, 1.96) * mm});
            skLineSegment(sketch, "E127.1.0.14", {"start": v(-73.5, -5.54) * mm, "end": v(-73.5, 9.46) * mm});
            skPoint(sketch, "E127.1.0.15", {"position": v(-82.5, 1.96) * mm});
            skLineSegment(sketch, "E127.1.0.16", {"start": v(-91.5, -5.54) * mm, "end": v(-91.5, 9.46) * mm});
            skPoint(sketch, "E127.1.0.17", {"position": v(-72.5, 1.96) * mm});
            skLineSegment(sketch, "E127.2.0.0", {"start": v(-64.5, -5.54) * mm, "end": v(-66.5, -5.54) * mm});
            skLineSegment(sketch, "E127.2.0.1", {"start": v(-64.5, 9.46) * mm, "end": v(-66.5, 9.46) * mm});
            skLineSegment(sketch, "E127.2.0.2", {"start": v(-46.5, 9.46) * mm, "end": v(-44.5, 9.46) * mm});
            skPoint(sketch, "E127.2.0.3", {"position": v(-55.5, 1.96) * mm});
            skLineSegment(sketch, "E127.2.0.4", {"start": v(-46.5, -5.54) * mm, "end": v(-44.5, -5.54) * mm});
            skPoint(sketch, "E127.2.0.5", {"position": v(-45.5, 1.96) * mm});
            skLineSegment(sketch, "E127.2.0.6", {"start": v(-44.5, -5.54) * mm, "end": v(-44.5, 9.46) * mm});
            skLineSegment(sketch, "E127.2.0.7", {"start": v(-64.5, -7.04) * mm, "end": v(-64.5, 10.96) * mm});
            skPoint(sketch, "E127.2.0.8", {"position": v(-65.5, 1.96) * mm});
            skLineSegment(sketch, "E127.2.0.9", {"start": v(-46.5, 10.96) * mm, "end": v(-64.5, 10.96) * mm});
            skLineSegment(sketch, "E127.2.0.10", {"start": v(-46.5, -7.04) * mm, "end": v(-64.5, -7.04) * mm});
            skLineSegment(sketch, "E127.2.0.11", {"start": v(-66.5, -5.54) * mm, "end": v(-66.5, 9.46) * mm});
            skLineSegment(sketch, "E127.2.0.12", {"start": v(-46.5, -7.04) * mm, "end": v(-46.5, 10.96) * mm});
            skPoint(sketch, "E127.2.0.13", {"position": v(-65.5, 1.96) * mm});
            skLineSegment(sketch, "E127.2.0.14", {"start": v(-46.5, -5.54) * mm, "end": v(-46.5, 9.46) * mm});
            skPoint(sketch, "E127.2.0.15", {"position": v(-55.5, 1.96) * mm});
            skLineSegment(sketch, "E127.2.0.16", {"start": v(-64.5, -5.54) * mm, "end": v(-64.5, 9.46) * mm});
            skPoint(sketch, "E127.2.0.17", {"position": v(-45.5, 1.96) * mm});
            skLineSegment(sketch, "E127.direction1", {"start": v(-120.5, -5.54) * mm, "end": v(-93.5, -5.54) * mm, "construction": true});
            skLineSegment(sketch, "E128.1.0.0", {"start": v(-71.5, -13.54) * mm, "end": v(-73.5, -13.54) * mm});
            skLineSegment(sketch, "E128.1.0.1", {"start": v(-71.5, -28.54) * mm, "end": v(-73.5, -28.54) * mm});
            skLineSegment(sketch, "E128.1.0.2", {"start": v(-91.5, -13.54) * mm, "end": v(-93.5, -13.54) * mm});
            skLineSegment(sketch, "E128.1.0.3", {"start": v(-73.5, -12.04) * mm, "end": v(-91.5, -12.04) * mm});
            skLineSegment(sketch, "E128.1.0.4", {"start": v(-71.5, -28.54) * mm, "end": v(-71.5, -13.54) * mm});
            skLineSegment(sketch, "E128.1.0.5", {"start": v(-73.5, -30.04) * mm, "end": v(-73.5, -12.04) * mm});
            skLineSegment(sketch, "E128.1.0.6", {"start": v(-93.5, -28.54) * mm, "end": v(-93.5, -13.54) * mm});
            skLineSegment(sketch, "E128.1.0.7", {"start": v(-91.5, -28.54) * mm, "end": v(-93.5, -28.54) * mm});
            skLineSegment(sketch, "E128.1.0.8", {"start": v(-73.5, -30.04) * mm, "end": v(-91.5, -30.04) * mm});
            skPoint(sketch, "E128.1.0.9", {"position": v(-92.5, -21.04) * mm});
            skPoint(sketch, "E128.1.0.10", {"position": v(-72.5, -21.04) * mm});
            skLineSegment(sketch, "E128.1.0.11", {"start": v(-91.5, -30.04) * mm, "end": v(-91.5, -12.04) * mm});
            skPoint(sketch, "E128.1.0.12", {"position": v(-82.5, -21.04) * mm});
            skPoint(sketch, "E128.1.0.13", {"position": v(-72.5, -21.04) * mm});
            skPoint(sketch, "E128.1.0.14", {"position": v(-92.5, -21.04) * mm});
            skPoint(sketch, "E128.1.0.15", {"position": v(-82.5, -21.04) * mm});
            skLineSegment(sketch, "E128.1.0.16", {"start": v(-91.5, -28.54) * mm, "end": v(-91.5, -13.54) * mm});
            skLineSegment(sketch, "E128.1.0.17", {"start": v(-73.5, -28.54) * mm, "end": v(-73.5, -13.54) * mm});
            skPoint(sketch, "E128.1.0.18", {"position": v(-72.5, -21.04) * mm});
            skPoint(sketch, "E128.1.0.19", {"position": v(-92.5, -21.04) * mm});
            skLineSegment(sketch, "E128.2.0.0", {"start": v(-44.5, -13.54) * mm, "end": v(-46.5, -13.54) * mm});
            skLineSegment(sketch, "E128.2.0.1", {"start": v(-44.5, -28.54) * mm, "end": v(-46.5, -28.54) * mm});
            skLineSegment(sketch, "E128.2.0.2", {"start": v(-64.5, -13.54) * mm, "end": v(-66.5, -13.54) * mm});
            skLineSegment(sketch, "E128.2.0.3", {"start": v(-46.5, -12.04) * mm, "end": v(-64.5, -12.04) * mm});
            skLineSegment(sketch, "E128.2.0.4", {"start": v(-44.5, -28.54) * mm, "end": v(-44.5, -13.54) * mm});
            skLineSegment(sketch, "E128.2.0.5", {"start": v(-46.5, -30.04) * mm, "end": v(-46.5, -12.04) * mm});
            skLineSegment(sketch, "E128.2.0.6", {"start": v(-66.5, -28.54) * mm, "end": v(-66.5, -13.54) * mm});
            skLineSegment(sketch, "E128.2.0.7", {"start": v(-64.5, -28.54) * mm, "end": v(-66.5, -28.54) * mm});
            skLineSegment(sketch, "E128.2.0.8", {"start": v(-46.5, -30.04) * mm, "end": v(-64.5, -30.04) * mm});
            skPoint(sketch, "E128.2.0.9", {"position": v(-65.5, -21.04) * mm});
            skPoint(sketch, "E128.2.0.10", {"position": v(-45.5, -21.04) * mm});
            skLineSegment(sketch, "E128.2.0.11", {"start": v(-64.5, -30.04) * mm, "end": v(-64.5, -12.04) * mm});
            skPoint(sketch, "E128.2.0.12", {"position": v(-55.5, -21.04) * mm});
            skPoint(sketch, "E128.2.0.13", {"position": v(-45.5, -21.04) * mm});
            skPoint(sketch, "E128.2.0.14", {"position": v(-65.5, -21.04) * mm});
            skPoint(sketch, "E128.2.0.15", {"position": v(-55.5, -21.04) * mm});
            skLineSegment(sketch, "E128.2.0.16", {"start": v(-64.5, -28.54) * mm, "end": v(-64.5, -13.54) * mm});
            skLineSegment(sketch, "E128.2.0.17", {"start": v(-46.5, -28.54) * mm, "end": v(-46.5, -13.54) * mm});
            skPoint(sketch, "E128.2.0.18", {"position": v(-45.5, -21.04) * mm});
            skPoint(sketch, "E128.2.0.19", {"position": v(-65.5, -21.04) * mm});
            skLineSegment(sketch, "E128.direction1", {"start": v(-120.5, -28.54) * mm, "end": v(-93.5, -28.54) * mm, "construction": true});
            skSolve(sketch);
        }
        {
            var Q0;
            Q0=qSketchRegion(id+"F4",true);
            extrude(context, id + "F5", {"entities" : qUnion([Q0]), "operationType" : NewBodyOperationType.REMOVE, "oppositeDirection" : true, "depth" : 5 * mm});
        }
        {
            var Q0;
            Q0=qCreatedBy(makeId("Top.planeOp"),FACE);
            var sketch = newSketch(context, id + "F6", { "sketchPlane" : qUnion([Q0])});
            skLineSegment(sketch, "E129.bottom", {"start": v(-106.79, 77.03) * mm, "end": v(-126.79, 77.03) * mm});
            skLineSegment(sketch, "E129.top", {"start": v(-106.79, 97.03) * mm, "end": v(-126.79, 97.03) * mm});
            skLineSegment(sketch, "E129.left", {"start": v(-106.79, 77.03) * mm, "end": v(-106.79, 97.03) * mm});
            skLineSegment(sketch, "E129.right", {"start": v(-126.79, 77.03) * mm, "end": v(-126.79, 97.03) * mm});
            skPoint(sketch, "E129.middle", {"position": v(-116.79, 87.03) * mm});
            skLineSegment(sketch, "E130.bottom", {"start": v(-105.79, 82.03) * mm, "end": v(-107.79, 82.03) * mm});
            skLineSegment(sketch, "E130.top", {"start": v(-105.79, 92.03) * mm, "end": v(-107.79, 92.03) * mm});
            skLineSegment(sketch, "E130.left", {"start": v(-105.79, 82.03) * mm, "end": v(-105.79, 92.03) * mm});
            skLineSegment(sketch, "E130.right", {"start": v(-107.79, 82.03) * mm, "end": v(-107.79, 92.03) * mm});
            skPoint(sketch, "E130.middle", {"position": v(-106.79, 87.03) * mm});
            skLineSegment(sketch, "E131.bottom", {"start": v(-125.79, 82.03) * mm, "end": v(-127.79, 82.03) * mm});
            skLineSegment(sketch, "E131.top", {"start": v(-125.79, 92.03) * mm, "end": v(-127.79, 92.03) * mm});
            skLineSegment(sketch, "E131.left", {"start": v(-125.79, 82.03) * mm, "end": v(-125.79, 92.03) * mm});
            skLineSegment(sketch, "E131.right", {"start": v(-127.79, 82.03) * mm, "end": v(-127.79, 92.03) * mm});
            skPoint(sketch, "E131.middle", {"position": v(-126.79, 87.03) * mm});
            skLineSegment(sketch, "E132.bottom", {"start": v(-107.79, 78.03) * mm, "end": v(-125.79, 78.03) * mm});
            skLineSegment(sketch, "E132.top", {"start": v(-107.79, 96.03) * mm, "end": v(-125.79, 96.03) * mm});
            skLineSegment(sketch, "E132.left", {"start": v(-107.79, 78.03) * mm, "end": v(-107.79, 96.03) * mm});
            skLineSegment(sketch, "E132.right", {"start": v(-125.79, 78.03) * mm, "end": v(-125.79, 96.03) * mm});
            skLineSegment(sketch, "E133.bottom", {"start": v(-107.79, 86.53) * mm, "end": v(-125.79, 86.53) * mm});
            skLineSegment(sketch, "E133.top", {"start": v(-107.79, 87.53) * mm, "end": v(-125.79, 87.53) * mm});
            skLineSegment(sketch, "E133.left", {"start": v(-107.79, 86.53) * mm, "end": v(-107.79, 87.53) * mm});
            skLineSegment(sketch, "E133.right", {"start": v(-125.79, 86.53) * mm, "end": v(-125.79, 87.53) * mm});
            skLineSegment(sketch, "E134.bottom", {"start": v(-115.79, 85.78) * mm, "end": v(-117.79, 85.78) * mm, "construction": true});
            skLineSegment(sketch, "E134.top", {"start": v(-115.79, 88.28) * mm, "end": v(-117.79, 88.28) * mm, "construction": true});
            skLineSegment(sketch, "E134.left", {"start": v(-115.79, 85.78) * mm, "end": v(-115.79, 88.28) * mm, "construction": true});
            skLineSegment(sketch, "E134.right", {"start": v(-117.79, 85.78) * mm, "end": v(-117.79, 88.28) * mm, "construction": true});
            skLineSegment(sketch, "E135.bottom", {"start": v(-110.82, 38.4) * mm, "end": v(-132.62, 38.4) * mm});
            skLineSegment(sketch, "E135.top", {"start": v(-110.82, 60.2) * mm, "end": v(-132.62, 60.2) * mm});
            skLineSegment(sketch, "E135.left", {"start": v(-110.82, 38.4) * mm, "end": v(-110.82, 60.2) * mm});
            skLineSegment(sketch, "E135.right", {"start": v(-132.62, 38.4) * mm, "end": v(-132.62, 60.2) * mm});
            skPoint(sketch, "E135.middle", {"position": v(-121.72, 49.3) * mm});
            skLineSegment(sketch, "E136.bottom", {"start": v(-110.82, 41.9) * mm, "end": v(-112.62, 41.9) * mm});
            skLineSegment(sketch, "E136.top", {"start": v(-110.82, 56.7) * mm, "end": v(-112.62, 56.7) * mm});
            skLineSegment(sketch, "E136.left", {"start": v(-110.82, 41.9) * mm, "end": v(-110.82, 56.7) * mm});
            skLineSegment(sketch, "E136.right", {"start": v(-112.62, 41.9) * mm, "end": v(-112.62, 56.7) * mm});
            skPoint(sketch, "E136.middle", {"position": v(-111.72, 49.3) * mm});
            skLineSegment(sketch, "E137.bottom", {"start": v(-130.82, 41.9) * mm, "end": v(-132.62, 41.9) * mm});
            skLineSegment(sketch, "E137.top", {"start": v(-130.82, 56.7) * mm, "end": v(-132.62, 56.7) * mm});
            skLineSegment(sketch, "E137.left", {"start": v(-130.82, 41.9) * mm, "end": v(-130.82, 56.7) * mm});
            skLineSegment(sketch, "E137.right", {"start": v(-132.62, 41.9) * mm, "end": v(-132.62, 56.7) * mm});
            skPoint(sketch, "E137.middle", {"position": v(-131.72, 49.3) * mm});
            skLineSegment(sketch, "E138.bottom", {"start": v(-112.62, 40.2) * mm, "end": v(-130.82, 40.2) * mm});
            skLineSegment(sketch, "E138.top", {"start": v(-112.62, 58.4) * mm, "end": v(-130.82, 58.4) * mm});
            skLineSegment(sketch, "E138.left", {"start": v(-112.62, 40.2) * mm, "end": v(-112.62, 58.4) * mm});
            skLineSegment(sketch, "E138.right", {"start": v(-130.82, 40.2) * mm, "end": v(-130.82, 58.4) * mm});
            skSolve(sketch);
        }
        {
            var Q0;
            {var subQ11=sQuery(id+"F6.wireOp",EDGE,"E135.bottom");Q0=makeQuery(id+"F6.imprint","IMPRINT",FACE,{"disambiguationData":[TD([[makeQuery(id+"F6.imprint","IMPRINT",EDGE,{"derivedFrom":subQ11}),-1.0]])]});}
            var Q1;
            {var subQ5=sQuery(id+"F6.wireOp",EDGE,"E136.right");Q1=makeQuery(id+"F6.imprint","IMPRINT",FACE,{"disambiguationData":[TD([[makeQuery(id+"F6.imprint","IMPRINT",EDGE,{"derivedFrom":subQ5}),-1.0]])]});}
            var Q2;
            {var subQ5=sQuery(id+"F6.wireOp",EDGE,"E137.left");Q2=makeQuery(id+"F6.imprint","IMPRINT",FACE,{"disambiguationData":[TD([[makeQuery(id+"F6.imprint","IMPRINT",EDGE,{"derivedFrom":subQ5}),1.0]])]});}
            var Q3;
            {var subQ0=sQuery(id+"F6.wireOp",EDGE,"E137.bottom");Q3=makeQuery(id+"F6.imprint","IMPRINT",FACE,{"disambiguationData":[TD([[makeQuery(id+"F6.imprint","IMPRINT",EDGE,{"derivedFrom":subQ0}),-1.0]])]});}
            var Q4;
            {var subQ2=sQuery(id+"F6.wireOp",EDGE,"E135.top");Q4=makeQuery(id+"F6.imprint","IMPRINT",FACE,{"disambiguationData":[TD([[makeQuery(id+"F6.imprint","IMPRINT",EDGE,{"derivedFrom":subQ2}),1.0]])]});}
            var Q5;
            {var subQ0=sQuery(id+"F6.wireOp",EDGE,"E136.bottom");Q5=makeQuery(id+"F6.imprint","IMPRINT",FACE,{"disambiguationData":[TD([[makeQuery(id+"F6.imprint","IMPRINT",EDGE,{"derivedFrom":subQ0}),-1.0]])]});}
            extrude(context, id + "F7", {"entities" : qUnion([Q0, Q1, Q2, Q3, Q4, Q5]), "depth" : 1 * mm});
        }
        {
            var Q0;
            {var subQ5=sQuery(id+"F6.wireOp",EDGE,"E137.right");Q0=makeQuery(id+"F6.imprint","IMPRINT",FACE,{"disambiguationData":[TD([[makeQuery(id+"F6.imprint","IMPRINT",EDGE,{"derivedFrom":subQ5}),-1.0]])]});}
            var Q1;
            {var subQ5=sQuery(id+"F6.wireOp",EDGE,"E137.left");Q1=makeQuery(id+"F6.imprint","IMPRINT",FACE,{"disambiguationData":[TD([[makeQuery(id+"F6.imprint","IMPRINT",EDGE,{"derivedFrom":subQ5}),1.0]])]});}
            var Q2;
            {var subQ5=sQuery(id+"F6.wireOp",EDGE,"E136.right");Q2=makeQuery(id+"F6.imprint","IMPRINT",FACE,{"disambiguationData":[TD([[makeQuery(id+"F6.imprint","IMPRINT",EDGE,{"derivedFrom":subQ5}),-1.0]])]});}
            var Q3;
            {var subQ5=sQuery(id+"F6.wireOp",EDGE,"E136.left");Q3=makeQuery(id+"F6.imprint","IMPRINT",FACE,{"disambiguationData":[TD([[makeQuery(id+"F6.imprint","IMPRINT",EDGE,{"derivedFrom":subQ5}),1.0]])]});}
            extrude(context, id + "F8", {"entities" : qUnion([Q0, Q1, Q2, Q3]), "operationType" : NewBodyOperationType.ADD, "oppositeDirection" : true, "depth" : 4 * mm});
        }
        {
            var Q0;
            Q0=makeQuery(id+"F7.opExtrude","CAP_FACE",FACE,{"disambiguationData":[OSD([sQuery(id+"F6.wireOp",EDGE,"E135.bottom"),sQuery(id+"F6.wireOp",EDGE,"E135.top"),sQuery(id+"F6.wireOp",EDGE,"E135.left"),sQuery(id+"F6.wireOp",EDGE,"E135.right"),sQuery(id+"F6.wireOp",EDGE,"E136.left"),sQuery(id+"F6.wireOp",EDGE,"E137.right"),sQuery(id+"F6.wireOp",EDGE,"E138.bottom"),sQuery(id+"F6.wireOp",EDGE,"E138.top"),sQuery(id+"F6.wireOp",EDGE,"E138.left"),sQuery(id+"F6.wireOp",EDGE,"E138.right")])],"isStart":false});
            var sketch = newSketch(context, id + "F9", { "sketchPlane" : qUnion([Q0])});
            skPoint(sketch, "E139.0", {"position": v(-121.72, 49.3) * mm});
            skLineSegment(sketch, "E140.bottom", {"start": v(-112.62, 40.2) * mm, "end": v(-130.82, 40.2) * mm});
            skLineSegment(sketch, "E140.top", {"start": v(-112.62, 58.4) * mm, "end": v(-130.82, 58.4) * mm});
            skLineSegment(sketch, "E140.left", {"start": v(-112.62, 40.2) * mm, "end": v(-112.62, 58.4) * mm});
            skLineSegment(sketch, "E140.right", {"start": v(-130.82, 40.2) * mm, "end": v(-130.82, 58.4) * mm});
            skLineSegment(sketch, "E141.0", {"start": v(-131.82, 39.2) * mm, "end": v(-131.82, 59.4) * mm});
            skLineSegment(sketch, "E141.1", {"start": v(-111.62, 39.2) * mm, "end": v(-131.82, 39.2) * mm});
            skLineSegment(sketch, "E141.2", {"start": v(-111.62, 39.2) * mm, "end": v(-111.62, 59.4) * mm});
            skLineSegment(sketch, "E141.3", {"start": v(-111.62, 59.4) * mm, "end": v(-131.82, 59.4) * mm});
            skSolve(sketch);
        }
        {
            var Q0;
            Q0=makeQuery(id+"F9.imprint","IMPRINT",FACE,{"disambiguationData":[TD([[makeQuery(id+"F9.imprint","IMPRINT",EDGE,{"derivedFrom":sQuery(id+"F9.wireOp",EDGE,"E140.bottom")}),1.0]])]});
            extrude(context, id + "F10", {"entities" : qUnion([Q0]), "operationType" : NewBodyOperationType.ADD, "depth" : 5 * mm});
        }
        {
            var Q0;
            Q0=makeQuery(id+"F10.opExtrude","CAP_FACE",FACE,{"disambiguationData":[OSD([sQuery(id+"F9.wireOp",EDGE,"E140.bottom"),sQuery(id+"F9.wireOp",EDGE,"E140.top"),sQuery(id+"F9.wireOp",EDGE,"E140.left"),sQuery(id+"F9.wireOp",EDGE,"E140.right"),sQuery(id+"F9.wireOp",EDGE,"E141.0"),sQuery(id+"F9.wireOp",EDGE,"E141.1"),sQuery(id+"F9.wireOp",EDGE,"E141.2"),sQuery(id+"F9.wireOp",EDGE,"E141.3")])],"isStart":false});
            var sketch = newSketch(context, id + "F11", { "sketchPlane" : qUnion([Q0])});
            skPoint(sketch, "E142.0", {"position": v(-121.72, 49.3) * mm});
            skLineSegment(sketch, "E143.bottom", {"start": v(-112.62, 48.8) * mm, "end": v(-130.82, 48.8) * mm});
            skLineSegment(sketch, "E143.top", {"start": v(-112.62, 49.8) * mm, "end": v(-130.82, 49.8) * mm});
            skLineSegment(sketch, "E143.left", {"start": v(-112.62, 48.8) * mm, "end": v(-112.62, 49.8) * mm});
            skLineSegment(sketch, "E143.right", {"start": v(-130.82, 48.8) * mm, "end": v(-130.82, 49.8) * mm});
            skLineSegment(sketch, "E144.bottom", {"start": v(-121.22, 40.2) * mm, "end": v(-122.22, 40.2) * mm});
            skLineSegment(sketch, "E144.top", {"start": v(-121.22, 58.4) * mm, "end": v(-122.22, 58.4) * mm});
            skLineSegment(sketch, "E144.left", {"start": v(-121.22, 40.2) * mm, "end": v(-121.22, 58.4) * mm});
            skLineSegment(sketch, "E144.right", {"start": v(-122.22, 40.2) * mm, "end": v(-122.22, 58.4) * mm});
            skSolve(sketch);
        }
        {
            var Q0;
            Q0=makeQuery(id+"FvrxBWBR3NFs59h_1.boolean.opBoolean","MERGE",FACE,{"derivedFrom":[makeQuery(id+"F5.boolean.opBoolean","COPY",FACE,{"derivedFrom":makeQuery(id+"F5.opExtrude","CAP_FACE",FACE,{"disambiguationData":[OSD([sQuery(id+"F4.wireOp",EDGE,"E114.bottom"),sQuery(id+"F4.wireOp",EDGE,"E114.top"),sQuery(id+"F4.wireOp",EDGE,"E114.left"),sQuery(id+"F4.wireOp",EDGE,"E114.right")])],"isStart":false})}),makeQuery(id+"FvrxBWBR3NFs59h_1.opExtrude","CAP_FACE",FACE,{"disambiguationData":[OSD([sQuery(id+"FOyiDT4y5zkIJA3_1.wireOp",EDGE,"oN5qgFBu-MPa5-jxRP-8K83-Y7W6XuHjnRPn.bottom"),sQuery(id+"FOyiDT4y5zkIJA3_1.wireOp",EDGE,"oN5qgFBu-MPa5-jxRP-8K83-Y7W6XuHjnRPn.top"),sQuery(id+"FOyiDT4y5zkIJA3_1.wireOp",EDGE,"oN5qgFBu-MPa5-jxRP-8K83-Y7W6XuHjnRPn.left"),sQuery(id+"FOyiDT4y5zkIJA3_1.wireOp",EDGE,"oN5qgFBu-MPa5-jxRP-8K83-Y7W6XuHjnRPn.right")])],"isStart":false}),makeQuery(id+"FvrxBWBR3NFs59h_1.opExtrude","CAP_FACE",FACE,{"disambiguationData":[OSD([sQuery(id+"FOyiDT4y5zkIJA3_1.wireOp",EDGE,"if443p5T-YKs4-1gVt-ORIe-qeo7ftMrQxsQ.bottom"),sQuery(id+"FOyiDT4y5zkIJA3_1.wireOp",EDGE,"if443p5T-YKs4-1gVt-ORIe-qeo7ftMrQxsQ.top"),sQuery(id+"FOyiDT4y5zkIJA3_1.wireOp",EDGE,"if443p5T-YKs4-1gVt-ORIe-qeo7ftMrQxsQ.left"),sQuery(id+"FOyiDT4y5zkIJA3_1.wireOp",EDGE,"if443p5T-YKs4-1gVt-ORIe-qeo7ftMrQxsQ.right")])],"isStart":false})]});
            var sketch = newSketch(context, id + "F12", { "sketchPlane" : qUnion([Q0])});
            skPoint(sketch, "E145.0", {"position": v(-109.5, 1.96) * mm});
            skLineSegment(sketch, "E146.bottom", {"start": v(-106.5, -1.04) * mm, "end": v(-112.5, -1.04) * mm});
            skLineSegment(sketch, "E146.top", {"start": v(-106.5, 4.96) * mm, "end": v(-112.5, 4.96) * mm});
            skLineSegment(sketch, "E146.left", {"start": v(-106.5, -1.04) * mm, "end": v(-106.5, 4.96) * mm});
            skLineSegment(sketch, "E146.right", {"start": v(-112.5, -1.04) * mm, "end": v(-112.5, 4.96) * mm});
            skLineSegment(sketch, "E147.bottom", {"start": v(-129, -1.04) * mm, "end": v(-135, -1.04) * mm});
            skLineSegment(sketch, "E147.top", {"start": v(-129, 4.96) * mm, "end": v(-135, 4.96) * mm});
            skLineSegment(sketch, "E147.left", {"start": v(-129, -1.04) * mm, "end": v(-129, 4.96) * mm});
            skLineSegment(sketch, "E147.right", {"start": v(-135, -1.04) * mm, "end": v(-135, 4.96) * mm});
            skPoint(sketch, "E147.middle", {"position": v(-132, 1.96) * mm});
            skSolve(sketch);
        }
        {
            var Q0;
            Q0 = qSketchRegion(id + "F11", true);
            extrude(context, id + "F13", {"entities" : qUnion([Q0]), "operationType" : NewBodyOperationType.ADD, "oppositeDirection" : true, "depth" : 6 * mm});
        }
        {
            var Q0;
            Q0=makeQuery(id+"F13.boolean.opBoolean","MERGE",FACE,{"derivedFrom":[makeQuery(id+"F10.opExtrude","CAP_FACE",FACE,{"disambiguationData":[OSD([sQuery(id+"F9.wireOp",EDGE,"E140.bottom"),sQuery(id+"F9.wireOp",EDGE,"E140.top"),sQuery(id+"F9.wireOp",EDGE,"E140.left"),sQuery(id+"F9.wireOp",EDGE,"E140.right"),sQuery(id+"F9.wireOp",EDGE,"E141.0"),sQuery(id+"F9.wireOp",EDGE,"E141.1"),sQuery(id+"F9.wireOp",EDGE,"E141.2"),sQuery(id+"F9.wireOp",EDGE,"E141.3")])],"isStart":false}),makeQuery(id+"F13.opExtrude","CAP_FACE",FACE,{"disambiguationData":[OSD([sQuery(id+"F11.wireOp",EDGE,"E143.bottom"),sQuery(id+"F11.wireOp",EDGE,"E143.top"),sQuery(id+"F11.wireOp",EDGE,"E143.left"),sQuery(id+"F11.wireOp",EDGE,"E143.right"),sQuery(id+"F11.wireOp",EDGE,"E144.bottom"),sQuery(id+"F11.wireOp",EDGE,"E144.top"),sQuery(id+"F11.wireOp",EDGE,"E144.left"),sQuery(id+"F11.wireOp",EDGE,"E144.right")])],"isStart":true})]});
            var sketch = newSketch(context, id + "F14", { "sketchPlane" : qUnion([Q0])});
            skPoint(sketch, "E148.0", {"position": v(-130.82, 58.4) * mm});
            skPoint(sketch, "E148.1", {"position": v(-112.62, 40.2) * mm});
            skLineSegment(sketch, "E149.bottom", {"start": v(-130.82, 58.4) * mm, "end": v(-112.62, 58.4) * mm});
            skLineSegment(sketch, "E149.top", {"start": v(-130.82, 40.2) * mm, "end": v(-112.62, 40.2) * mm});
            skLineSegment(sketch, "E149.left", {"start": v(-130.82, 58.4) * mm, "end": v(-130.82, 40.2) * mm});
            skLineSegment(sketch, "E149.right", {"start": v(-112.62, 58.4) * mm, "end": v(-112.62, 40.2) * mm});
            skSolve(sketch);
        }
        {
            var Q0;
            Q0 = qSketchRegion(id + "F14", true);
            extrude(context, id + "F15", {"entities" : qUnion([Q0]), "operationType" : NewBodyOperationType.REMOVE, "oppositeDirection" : true, "depth" : 1 * mm});
        }
        {
            var Q0;
            {var subQ0=sQuery(id+"F6.wireOp",EDGE,"E137.right");var subQ2=sQuery(id+"F6.wireOp",EDGE,"E138.right");var subQ4=sQuery(id+"F6.wireOp",EDGE,"E136.left");var subQ6=sQuery(id+"F6.wireOp",EDGE,"E138.left");var subQ8=sQuery(id+"F6.wireOp",EDGE,"E135.top");var subQ9=sQuery(id+"F6.wireOp",EDGE,"E135.left");var subQ11=sQuery(id+"F6.wireOp",EDGE,"E135.right");var subQ13=sQuery(id+"F6.wireOp",EDGE,"E138.top");var subQ16=sQuery(id+"F6.wireOp",EDGE,"E138.bottom");var subQ17=sQuery(id+"F6.wireOp",EDGE,"E135.bottom");var subQ18=makeQuery(id+"F7.opExtrude","CAP_FACE",FACE,{"disambiguationData":[OSD([subQ17,subQ8,subQ9,subQ11,subQ4,subQ0,subQ16,subQ13,subQ6,subQ2])],"isStart":true});Q0=makeQuery(id+"F13.boolean.opBoolean","MERGE",FACE,{"derivedFrom":[makeQuery(id+"F8.boolean.opBoolean","SPLIT",FACE,{"disambiguationData":[TD([makeQuery(id+"F7.opExtrude","SWEPT_FACE",FACE,{"disambiguationData":[OSD([subQ17])]})])],"derivedFrom":subQ18}),makeQuery(id+"F8.boolean.opBoolean","SPLIT",FACE,{"disambiguationData":[TD([makeQuery(id+"F7.opExtrude","SWEPT_FACE",FACE,{"disambiguationData":[OSD([subQ8])]})])],"derivedFrom":subQ18}),makeQuery(id+"F13.opExtrude","CAP_FACE",FACE,{"disambiguationData":[OSD([sQuery(id+"F11.wireOp",EDGE,"E143.bottom"),sQuery(id+"F11.wireOp",EDGE,"E143.top"),sQuery(id+"F11.wireOp",EDGE,"E143.left"),sQuery(id+"F11.wireOp",EDGE,"E143.right"),sQuery(id+"F11.wireOp",EDGE,"E144.bottom"),sQuery(id+"F11.wireOp",EDGE,"E144.top"),sQuery(id+"F11.wireOp",EDGE,"E144.left"),sQuery(id+"F11.wireOp",EDGE,"E144.right")])],"isStart":false})]});}
            var sketch = newSketch(context, id + "F16", { "sketchPlane" : qUnion([Q0])});
            skPoint(sketch, "E150.0", {"position": v(-121.72, -40.2) * mm});
            skLineSegment(sketch, "E151.bottom", {"start": v(-120.47, -50.3) * mm, "end": v(-122.97, -50.3) * mm});
            skLineSegment(sketch, "E151.top", {"start": v(-120.47, -48.3) * mm, "end": v(-122.97, -48.3) * mm});
            skLineSegment(sketch, "E151.left", {"start": v(-120.47, -50.3) * mm, "end": v(-120.47, -48.3) * mm});
            skLineSegment(sketch, "E151.right", {"start": v(-122.97, -50.3) * mm, "end": v(-122.97, -48.3) * mm});
            skPoint(sketch, "E151.middle", {"position": v(-121.72, -49.3) * mm});
            skPoint(sketch, "E151.middle.positionSnap0", {"position": v(-130.82, -49.3) * mm});
            skPoint(sketch, "E151.centerSnap0", {"position": v(-130.82, -49.3) * mm});
            skSolve(sketch);
        }
        {
            var Q0;
            Q0=makeQuery(id+"FOl8yoey8HPPjfu_3.opExtrude","CAP_FACE",FACE,{"disambiguationData":[OSD([sQuery(id+"F12.wireOp",EDGE,"E146.bottom"),sQuery(id+"F12.wireOp",EDGE,"E146.top"),sQuery(id+"F12.wireOp",EDGE,"E146.left"),sQuery(id+"F12.wireOp",EDGE,"E146.right")])],"isStart":false});
            var sketch = newSketch(context, id + "F17", { "sketchPlane" : qUnion([Q0])});
            skPoint(sketch, "E152.0", {"position": v(-111.5, 3.96) * mm});
            skLineSegment(sketch, "E153.bottom", {"start": v(-108.5, 0.7) * mm, "end": v(-110.5, 0.7) * mm});
            skLineSegment(sketch, "E153.top", {"start": v(-108.5, 3.2) * mm, "end": v(-110.5, 3.2) * mm});
            skLineSegment(sketch, "E153.left", {"start": v(-108.5, 0.7) * mm, "end": v(-108.5, 3.2) * mm});
            skLineSegment(sketch, "E153.right", {"start": v(-110.5, 0.7) * mm, "end": v(-110.5, 3.2) * mm});
            skPoint(sketch, "E153.middle", {"position": v(-109.5, 1.96) * mm});
            skPoint(sketch, "E154.1", {"position": v(-132, 4.96) * mm});
            skPoint(sketch, "E155.0", {"position": v(-135, 1.96) * mm});
            skLineSegment(sketch, "E156.bottom", {"start": v(-131, 0.7) * mm, "end": v(-133, 0.7) * mm});
            skLineSegment(sketch, "E156.top", {"start": v(-131, 3.2) * mm, "end": v(-133, 3.2) * mm});
            skLineSegment(sketch, "E156.left", {"start": v(-131, 0.7) * mm, "end": v(-131, 3.2) * mm});
            skLineSegment(sketch, "E156.right", {"start": v(-133, 0.7) * mm, "end": v(-133, 3.2) * mm});
            skPoint(sketch, "E156.middle", {"position": v(-132, 1.96) * mm});
            skSolve(sketch);
        }
        {
            var Q0;
            {var subQ0=sQuery(id+"F11.wireOp",EDGE,"E143.right");var subQ1=sQuery(id+"F11.wireOp",EDGE,"E143.bottom");var subQ4=sQuery(id+"F11.wireOp",EDGE,"E144.right");var subQ5=sQuery(id+"F6.wireOp",EDGE,"E138.right");var subQ8=sQuery(id+"F11.wireOp",EDGE,"E143.top");var subQ9=sQuery(id+"F6.wireOp",EDGE,"E137.right");var subQ11=sQuery(id+"F6.wireOp",EDGE,"E136.left");var subQ13=sQuery(id+"F6.wireOp",EDGE,"E138.left");var subQ15=sQuery(id+"F6.wireOp",EDGE,"E135.top");var subQ16=sQuery(id+"F6.wireOp",EDGE,"E135.left");var subQ18=sQuery(id+"F6.wireOp",EDGE,"E135.right");var subQ20=sQuery(id+"F6.wireOp",EDGE,"E138.top");var subQ22=sQuery(id+"F6.wireOp",EDGE,"E138.bottom");var subQ23=sQuery(id+"F6.wireOp",EDGE,"E135.bottom");var subQ24=makeQuery(id+"F7.opExtrude","CAP_FACE",FACE,{"disambiguationData":[OSD([subQ23,subQ15,subQ16,subQ18,subQ11,subQ9,subQ22,subQ20,subQ13,subQ5])],"isStart":true});Q0=makeQuery(id+"F20.boolean.opBoolean","SPLIT",FACE,{"disambiguationData":[TD([makeQuery(id+"F20.opExtrude","SWEPT_FACE",FACE,{"disambiguationData":[OSD([sQuery(id+"F16.wireOp",EDGE,"E151.right")])]})])],"derivedFrom":makeQuery(id+"F13.boolean.opBoolean","MERGE",FACE,{"derivedFrom":[makeQuery(id+"F8.boolean.opBoolean","SPLIT",FACE,{"disambiguationData":[TD([makeQuery(id+"F7.opExtrude","SWEPT_FACE",FACE,{"disambiguationData":[OSD([subQ23])]})])],"derivedFrom":subQ24}),makeQuery(id+"F8.boolean.opBoolean","SPLIT",FACE,{"disambiguationData":[TD([makeQuery(id+"F7.opExtrude","SWEPT_FACE",FACE,{"disambiguationData":[OSD([subQ15])]})])],"derivedFrom":subQ24}),makeQuery(id+"F13.opExtrude","CAP_FACE",FACE,{"disambiguationData":[OSD([subQ1,subQ8,sQuery(id+"F11.wireOp",EDGE,"E143.left"),subQ0,sQuery(id+"F11.wireOp",EDGE,"E144.bottom"),sQuery(id+"F11.wireOp",EDGE,"E144.top"),sQuery(id+"F11.wireOp",EDGE,"E144.left"),subQ4])],"isStart":false})]})});}
            var sketch = newSketch(context, id + "F18", { "sketchPlane" : qUnion([Q0])});
            skPoint(sketch, "E157.0", {"position": v(-126.52, -48.8) * mm});
            skPoint(sketch, "E158.0", {"position": v(-122.22, -44.5) * mm});
            skPoint(sketch, "E159.0", {"position": v(-122.22, -40.2) * mm});
            skLineSegment(sketch, "E160.bottom", {"start": v(-122.22, -40.2) * mm, "end": v(-130.82, -40.2) * mm});
            skLineSegment(sketch, "E160.top", {"start": v(-122.22, -48.8) * mm, "end": v(-130.82, -48.8) * mm});
            skLineSegment(sketch, "E160.left", {"start": v(-122.22, -40.2) * mm, "end": v(-122.22, -48.8) * mm});
            skLineSegment(sketch, "E160.right", {"start": v(-130.82, -40.2) * mm, "end": v(-130.82, -48.8) * mm});
            skPoint(sketch, "E160.middle", {"position": v(-126.52, -44.5) * mm});
            skLineSegment(sketch, "E161.bottom", {"start": v(-122.72, -40.7) * mm, "end": v(-130.32, -40.7) * mm});
            skLineSegment(sketch, "E161.top", {"start": v(-122.72, -48.3) * mm, "end": v(-130.32, -48.3) * mm});
            skLineSegment(sketch, "E161.left", {"start": v(-122.72, -40.7) * mm, "end": v(-122.72, -48.3) * mm});
            skLineSegment(sketch, "E161.right", {"start": v(-130.32, -40.7) * mm, "end": v(-130.32, -48.3) * mm});
            skLineSegment(sketch, "E162.direction1", {"start": v(-130.82, -48.8) * mm, "end": v(-121.22, -48.8) * mm, "construction": true});
            skLineSegment(sketch, "E163.0.1.0", {"start": v(-113.12, -40.7) * mm, "end": v(-120.72, -40.7) * mm});
            skLineSegment(sketch, "E163.3.1.0", {"start": v(-112.62, -40.2) * mm, "end": v(-121.22, -40.2) * mm});
            skLineSegment(sketch, "E163.6.1.0", {"start": v(-112.62, -48.8) * mm, "end": v(-121.22, -48.8) * mm});
            skLineSegment(sketch, "E163.9.1.0", {"start": v(-112.62, -40.2) * mm, "end": v(-112.62, -48.8) * mm});
            skPoint(sketch, "E163.12.1.0", {"position": v(-116.92, -44.5) * mm});
            skLineSegment(sketch, "E163.13.1.0", {"start": v(-113.12, -40.7) * mm, "end": v(-113.12, -48.3) * mm});
            skLineSegment(sketch, "E163.16.1.0", {"start": v(-120.72, -40.7) * mm, "end": v(-120.72, -48.3) * mm});
            skLineSegment(sketch, "E163.19.1.0", {"start": v(-121.22, -40.2) * mm, "end": v(-121.22, -48.8) * mm});
            skPoint(sketch, "E163.22.1.0", {"position": v(-112.62, -44.5) * mm});
            skPoint(sketch, "E163.23.1.0", {"position": v(-112.62, -40.2) * mm});
            skLineSegment(sketch, "E163.24.1.0", {"start": v(-113.12, -48.3) * mm, "end": v(-120.72, -48.3) * mm});
            skPoint(sketch, "E163.27.1.0", {"position": v(-116.92, -48.8) * mm});
            skPoint(sketch, "E163.28.1.0", {"position": v(-116.92, -44.5) * mm});
            skSolve(sketch);
        }
        {
            var Q0;
            Q0 = qSketchRegion(id + "F18", true);
            extrude(context, id + "F19", {"entities" : qUnion([Q0]), "operationType" : NewBodyOperationType.ADD, "oppositeDirection" : true, "depth" : 2 * mm});
        }
        {
            var Q0;
            Q0 = qSketchRegion(id + "F16", true);
            extrude(context, id + "F20", {"entities" : qUnion([Q0]), "operationType" : NewBodyOperationType.REMOVE, "oppositeDirection" : true, "depth" : 2 * mm});
        }
        {
            var Q0;
            Q0=makeQuery(id+"F0.imprint","IMPRINT",FACE,{"disambiguationData":[TD([[makeQuery(id+"F0.imprint","IMPRINT",EDGE,{"derivedFrom":sQuery(id+"F0.wireOp",EDGE,"E0.bottom")}),-1.0]])]});
            var sketch = newSketch(context, id + "F21", { "sketchPlane" : qUnion([Q0])});
            skLineSegment(sketch, "E164.top", {"start": v(-139.5, -33.04) * mm, "end": v(-43.5, -33.04) * mm});
            skLineSegment(sketch, "E164.left", {"start": v(-139.5, -55.04) * mm, "end": v(-139.5, -33.04) * mm});
            skLineSegment(sketch, "E165.top", {"start": v(-25.5, -11.04) * mm, "end": v(-43.5, -11.04) * mm});
            skLineSegment(sketch, "E165.right", {"start": v(-43.5, -33.04) * mm, "end": v(-43.5, -11.04) * mm});
            skLineSegment(sketch, "E166.top", {"start": v(-9.5, 11.96) * mm, "end": v(-25.5, 11.96) * mm});
            skLineSegment(sketch, "E166.right", {"start": v(-25.5, -11.04) * mm, "end": v(-25.5, 11.96) * mm});
            skLineSegment(sketch, "E167", {"start": v(-9.5, 11.96) * mm, "end": v(-9.5, -55.04) * mm});
            skLineSegment(sketch, "E168", {"start": v(-139.5, -55.04) * mm, "end": v(-9.5, -55.04) * mm});
            skLineSegment(sketch, "E169.bottom", {"start": v(-43.5, -33.04) * mm, "end": v(-9.5, -33.04) * mm});
            skLineSegment(sketch, "E169.top", {"start": v(-43.5, -31.04) * mm, "end": v(-9.5, -31.04) * mm});
            skLineSegment(sketch, "E169.left", {"start": v(-43.5, -33.04) * mm, "end": v(-43.5, -31.04) * mm});
            skLineSegment(sketch, "E169.right", {"start": v(-9.5, -33.04) * mm, "end": v(-9.5, -31.04) * mm});
            skLineSegment(sketch, "E170.bottom", {"start": v(-25.5, -11.04) * mm, "end": v(-9.5, -11.04) * mm});
            skLineSegment(sketch, "E170.top", {"start": v(-25.5, -9.04) * mm, "end": v(-9.5, -9.04) * mm});
            skLineSegment(sketch, "E170.left", {"start": v(-25.5, -11.04) * mm, "end": v(-25.5, -9.04) * mm});
            skLineSegment(sketch, "E170.right", {"start": v(-9.5, -11.04) * mm, "end": v(-9.5, -9.04) * mm});
            skLineSegment(sketch, "E171", {"start": v(-25.5, -11.04) * mm, "end": v(-25.5, -31.04) * mm});
            skSolve(sketch);
        }
        {
            var Q0;
            Q0=makeQuery(id+"F21.imprint","IMPRINT",FACE,{"disambiguationData":[TD([[makeQuery(id+"F21.imprint","IMPRINT",EDGE,{"derivedFrom":makeQuery(id+"F0.imprint","IMPRINT",EDGE,{"derivedFrom":sQuery(id+"F0.wireOp",EDGE,"6XQCNLW2-68Wz-nC9p-wT4x-b90YEvEmSNLj")})}),1.0]])]});
            var Q1;
            Q1=makeQuery(id+"F21.imprint","IMPRINT",FACE,{"disambiguationData":[TD([[makeQuery(id+"F21.imprint","IMPRINT",EDGE,{"derivedFrom":makeQuery(id+"F0.imprint","IMPRINT",EDGE,{"derivedFrom":sQuery(id+"F0.wireOp",EDGE,"E3")})}),1.0]])]});
            var Q2;
            Q2=makeQuery(id+"F21.imprint","IMPRINT",FACE,{"disambiguationData":[TD([[makeQuery(id+"F21.imprint","IMPRINT",EDGE,{"derivedFrom":makeQuery(id+"F0.imprint","IMPRINT",EDGE,{"derivedFrom":sQuery(id+"F0.wireOp",EDGE,"E4")})}),1.0]])]});
            var Q3;
            Q3=makeQuery(id+"F21.imprint","IMPRINT",FACE,{"disambiguationData":[TD([[makeQuery(id+"F21.imprint","IMPRINT",EDGE,{"derivedFrom":makeQuery(id+"F0.imprint","IMPRINT",EDGE,{"derivedFrom":sQuery(id+"F0.wireOp",EDGE,"E7")})}),1.0]])]});
            var Q4;
            Q4=makeQuery(id+"F21.imprint","IMPRINT",FACE,{"disambiguationData":[TD([[makeQuery(id+"F21.imprint","IMPRINT",EDGE,{"derivedFrom":makeQuery(id+"F0.imprint","IMPRINT",EDGE,{"derivedFrom":sQuery(id+"F0.wireOp",EDGE,"E8")})}),1.0]])]});
            var Q5;
            Q5=makeQuery(id+"F21.imprint","IMPRINT",FACE,{"disambiguationData":[TD([[makeQuery(id+"F21.imprint","IMPRINT",EDGE,{"derivedFrom":makeQuery(id+"F0.imprint","IMPRINT",EDGE,{"derivedFrom":sQuery(id+"F0.wireOp",EDGE,"E9")})}),1.0]])]});
            var Q6;
            Q6=makeQuery(id+"F21.imprint","IMPRINT",FACE,{"disambiguationData":[TD([[makeQuery(id+"F21.imprint","IMPRINT",EDGE,{"derivedFrom":makeQuery(id+"F0.imprint","IMPRINT",EDGE,{"derivedFrom":sQuery(id+"F0.wireOp",EDGE,"E10")})}),1.0]])]});
            var Q7;
            Q7=makeQuery(id+"F21.imprint","IMPRINT",FACE,{"disambiguationData":[TD([[makeQuery(id+"F21.imprint","IMPRINT",EDGE,{"derivedFrom":makeQuery(id+"F0.imprint","IMPRINT",EDGE,{"derivedFrom":sQuery(id+"F0.wireOp",EDGE,"E11")})}),1.0]])]});
            var Q8;
            Q8=makeQuery(id+"F21.imprint","IMPRINT",FACE,{"disambiguationData":[TD([[makeQuery(id+"F21.imprint","IMPRINT",EDGE,{"derivedFrom":makeQuery(id+"F0.imprint","IMPRINT",EDGE,{"derivedFrom":sQuery(id+"F0.wireOp",EDGE,"E12")})}),1.0]])]});
            var Q9;
            Q9=makeQuery(id+"F21.imprint","IMPRINT",FACE,{"disambiguationData":[TD([[makeQuery(id+"F21.imprint","IMPRINT",EDGE,{"derivedFrom":makeQuery(id+"F0.imprint","IMPRINT",EDGE,{"derivedFrom":sQuery(id+"F0.wireOp",EDGE,"E13")})}),1.0]])]});
            var Q10;
            Q10=makeQuery(id+"F21.imprint","IMPRINT",FACE,{"disambiguationData":[TD([[makeQuery(id+"F21.imprint","IMPRINT",EDGE,{"derivedFrom":makeQuery(id+"F0.imprint","IMPRINT",EDGE,{"derivedFrom":sQuery(id+"F0.wireOp",EDGE,"E15")})}),1.0]])]});
            var Q11;
            Q11=makeQuery(id+"F21.imprint","IMPRINT",FACE,{"disambiguationData":[TD([[makeQuery(id+"F21.imprint","IMPRINT",EDGE,{"derivedFrom":makeQuery(id+"F0.imprint","IMPRINT",EDGE,{"derivedFrom":sQuery(id+"F0.wireOp",EDGE,"E16")})}),1.0]])]});
            var Q12;
            {var subQ1=sQuery(id+"F21.wireOp",EDGE,"E166.top");Q12=makeQuery(id+"F21.imprint","IMPRINT",FACE,{"disambiguationData":[TD([[makeQuery(id+"F21.imprint","IMPRINT",EDGE,{"derivedFrom":subQ1}),1.0]])]});}
            var Q13;
            Q13=makeQuery(id+"F21.imprint","IMPRINT",FACE,{"disambiguationData":[TD([[makeQuery(id+"F21.imprint","IMPRINT",EDGE,{"derivedFrom":sQuery(id+"F21.wireOp",EDGE,"E165.top")}),1.0]])]});
            var Q14;
            Q14=makeQuery(id+"F21.imprint","IMPRINT",FACE,{"disambiguationData":[TD([[makeQuery(id+"F21.imprint","IMPRINT",EDGE,{"derivedFrom":sQuery(id+"F21.wireOp",EDGE,"E164.top")}),-1.0]])]});
            extrude(context, id + "F22", {"entities" : qUnion([Q0, Q1, Q2, Q3, Q4, Q5, Q6, Q7, Q8, Q9, Q10, Q11, Q12, Q13, Q14]), "operationType" : NewBodyOperationType.REMOVE, "depth" : 5 * mm});
        }
        {
            var Q0;
            Q0=makeQuery(id+"F1.imprint","IMPRINT",FACE,{"disambiguationData":[TD([[makeQuery(id+"F1.imprint","IMPRINT",EDGE,{"derivedFrom":sQuery(id+"F1.wireOp",EDGE,"E73.bottom")}),-1.0]])]});
            var Q1;
            {var subQ0=sQuery(id+"F1.wireOp",EDGE,"564e7f7f-852e-44c8-adaa-80bbbea6a7a0.right");var subQ1=sQuery(id+"F1.wireOp",EDGE,"564e7f7f-852e-44c8-adaa-80bbbea6a7a0.top");var subQ2=makeQuery(id+"F1.imprint","INTERSECT",VERTEX,{"derivedFrom":[subQ1,subQ0]});Q1=makeQuery(id+"F1.imprint","IMPRINT",FACE,{"disambiguationData":[TD([[makeQuery(id+"F1.imprint","IMPRINT",EDGE,{"disambiguationData":[TD([[subQ2,1.0]])],"derivedFrom":subQ1}),1.0]])]});}
            var Q2;
            {var subQ0=sQuery(id+"F1.wireOp",EDGE,"564e7f7f-852e-44c8-adaa-80bbbea6a7a0.left");var subQ1=sQuery(id+"F1.wireOp",EDGE,"564e7f7f-852e-44c8-adaa-80bbbea6a7a0.top");var subQ2=makeQuery(id+"F1.imprint","INTERSECT",VERTEX,{"derivedFrom":[subQ1,subQ0]});Q2=makeQuery(id+"F1.imprint","IMPRINT",FACE,{"disambiguationData":[TD([[makeQuery(id+"F1.imprint","IMPRINT",EDGE,{"disambiguationData":[TD([[subQ2,-1.0]])],"derivedFrom":subQ1}),1.0]])]});}
            var Q3;
            {var subQ0=sQuery(id+"F1.wireOp",EDGE,"564e7f7f-852e-44c8-adaa-80bbbea6a7a0.right");var subQ1=sQuery(id+"F1.wireOp",EDGE,"564e7f7f-852e-44c8-adaa-80bbbea6a7a0.bottom");var subQ2=makeQuery(id+"F1.imprint","INTERSECT",VERTEX,{"derivedFrom":[subQ1,subQ0]});Q3=makeQuery(id+"F1.imprint","IMPRINT",FACE,{"disambiguationData":[TD([[makeQuery(id+"F1.imprint","IMPRINT",EDGE,{"disambiguationData":[TD([[subQ2,1.0]])],"derivedFrom":subQ1}),-1.0]])]});}
            var Q4;
            {var subQ0=sQuery(id+"F1.wireOp",EDGE,"564e7f7f-852e-44c8-adaa-80bbbea6a7a0.left");var subQ1=sQuery(id+"F1.wireOp",EDGE,"564e7f7f-852e-44c8-adaa-80bbbea6a7a0.bottom");var subQ2=makeQuery(id+"F1.imprint","INTERSECT",VERTEX,{"derivedFrom":[subQ1,subQ0]});Q4=makeQuery(id+"F1.imprint","IMPRINT",FACE,{"disambiguationData":[TD([[makeQuery(id+"F1.imprint","IMPRINT",EDGE,{"disambiguationData":[TD([[subQ2,-1.0]])],"derivedFrom":subQ1}),-1.0]])]});}
            var Q5;
            {var subQ0=sQuery(id+"F1.wireOp",EDGE,"E91.right");var subQ1=sQuery(id+"F1.wireOp",EDGE,"E91.top");var subQ2=makeQuery(id+"F1.imprint","INTERSECT",VERTEX,{"derivedFrom":[subQ1,subQ0]});Q5=makeQuery(id+"F1.imprint","IMPRINT",FACE,{"disambiguationData":[TD([[makeQuery(id+"F1.imprint","IMPRINT",EDGE,{"disambiguationData":[TD([[subQ2,1.0]])],"derivedFrom":subQ1}),1.0]])]});}
            var Q6;
            {var subQ0=sQuery(id+"F1.wireOp",EDGE,"E91.left");var subQ1=sQuery(id+"F1.wireOp",EDGE,"E91.top");var subQ2=makeQuery(id+"F1.imprint","INTERSECT",VERTEX,{"derivedFrom":[subQ1,subQ0]});Q6=makeQuery(id+"F1.imprint","IMPRINT",FACE,{"disambiguationData":[TD([[makeQuery(id+"F1.imprint","IMPRINT",EDGE,{"disambiguationData":[TD([[subQ2,-1.0]])],"derivedFrom":subQ1}),1.0]])]});}
            var Q7;
            {var subQ0=sQuery(id+"F1.wireOp",EDGE,"E91.right");var subQ1=sQuery(id+"F1.wireOp",EDGE,"E91.bottom");var subQ2=makeQuery(id+"F1.imprint","INTERSECT",VERTEX,{"derivedFrom":[subQ1,subQ0]});Q7=makeQuery(id+"F1.imprint","IMPRINT",FACE,{"disambiguationData":[TD([[makeQuery(id+"F1.imprint","IMPRINT",EDGE,{"disambiguationData":[TD([[subQ2,1.0]])],"derivedFrom":subQ1}),-1.0]])]});}
            var Q8;
            {var subQ0=sQuery(id+"F1.wireOp",EDGE,"E91.left");var subQ1=sQuery(id+"F1.wireOp",EDGE,"E91.bottom");var subQ2=makeQuery(id+"F1.imprint","INTERSECT",VERTEX,{"derivedFrom":[subQ1,subQ0]});Q8=makeQuery(id+"F1.imprint","IMPRINT",FACE,{"disambiguationData":[TD([[makeQuery(id+"F1.imprint","IMPRINT",EDGE,{"disambiguationData":[TD([[subQ2,-1.0]])],"derivedFrom":subQ1}),-1.0]])]});}
            extrude(context, id + "F23", {"entities" : qUnion([Q0, Q1, Q2, Q3, Q4, Q5, Q6, Q7, Q8]), "depth" : 2 * mm});
        }
        {
            var Q0;
            Q0=makeQuery(id+"F3.opExtrude","CAP_FACE",FACE,{"disambiguationData":[OSD([sQuery(id+"F0.wireOp",EDGE,"E0.bottom"),sQuery(id+"F0.wireOp",EDGE,"E0.top"),sQuery(id+"F0.wireOp",EDGE,"E0.left"),sQuery(id+"F0.wireOp",EDGE,"E0.right"),sQuery(id+"F0.wireOp",EDGE,"6XQCNLW2-68Wz-nC9p-wT4x-b90YEvEmSNLj"),sQuery(id+"F0.wireOp",EDGE,"E3"),sQuery(id+"F0.wireOp",EDGE,"E4"),sQuery(id+"F0.wireOp",EDGE,"E7"),sQuery(id+"F0.wireOp",EDGE,"E8"),sQuery(id+"F0.wireOp",EDGE,"E9"),sQuery(id+"F0.wireOp",EDGE,"E10"),sQuery(id+"F0.wireOp",EDGE,"E11"),sQuery(id+"F0.wireOp",EDGE,"E12"),sQuery(id+"F0.wireOp",EDGE,"E13"),sQuery(id+"F0.wireOp",EDGE,"E14.bottom"),sQuery(id+"F0.wireOp",EDGE,"E14.top"),sQuery(id+"F0.wireOp",EDGE,"E14.left"),sQuery(id+"F0.wireOp",EDGE,"E14.right"),sQuery(id+"F0.wireOp",EDGE,"E15"),sQuery(id+"F0.wireOp",EDGE,"E16"),sQuery(id+"F0.wireOp",EDGE,"E18.bottom"),sQuery(id+"F0.wireOp",EDGE,"E18.top"),sQuery(id+"F0.wireOp",EDGE,"E18.left"),sQuery(id+"F0.wireOp",EDGE,"E18.right"),sQuery(id+"F0.wireOp",EDGE,"E20.bottom"),sQuery(id+"F0.wireOp",EDGE,"E20.top"),sQuery(id+"F0.wireOp",EDGE,"E21.left"),sQuery(id+"F0.wireOp",EDGE,"E21.right"),sQuery(id+"F0.wireOp",EDGE,"E22.left"),sQuery(id+"F0.wireOp",EDGE,"E22.right"),sQuery(id+"F0.wireOp",EDGE,"E23.trimOffspring"),sQuery(id+"F0.wireOp",EDGE,"E24.trimOffspring"),sQuery(id+"F0.wireOp",EDGE,"E25.trimOffspring"),sQuery(id+"F0.wireOp",EDGE,"E26.trimOffspring"),sQuery(id+"F0.wireOp",EDGE,"E27.trimOffspring"),sQuery(id+"F0.wireOp",EDGE,"E28.trimOffspring"),sQuery(id+"F0.wireOp",EDGE,"E29.trimOffspring"),sQuery(id+"F0.wireOp",EDGE,"E30.trimOffspring"),sQuery(id+"F0.wireOp",EDGE,"E19.bottom"),sQuery(id+"F0.wireOp",EDGE,"E19.top"),sQuery(id+"F0.wireOp",EDGE,"E19.left"),sQuery(id+"F0.wireOp",EDGE,"E19.right"),sQuery(id+"F0.wireOp",EDGE,"E31.bottom"),sQuery(id+"F0.wireOp",EDGE,"E31.top"),sQuery(id+"F0.wireOp",EDGE,"E32.left"),sQuery(id+"F0.wireOp",EDGE,"E32.right"),sQuery(id+"F0.wireOp",EDGE,"E33.left"),sQuery(id+"F0.wireOp",EDGE,"E33.right"),sQuery(id+"F0.wireOp",EDGE,"E34.trimOffspring"),sQuery(id+"F0.wireOp",EDGE,"E35.trimOffspring"),sQuery(id+"F0.wireOp",EDGE,"E36.trimOffspring"),sQuery(id+"F0.wireOp",EDGE,"E37.trimOffspring"),sQuery(id+"F0.wireOp",EDGE,"E38.trimOffspring"),sQuery(id+"F0.wireOp",EDGE,"E39.trimOffspring"),sQuery(id+"F0.wireOp",EDGE,"E40.trimOffspring"),sQuery(id+"F0.wireOp",EDGE,"E41.trimOffspring"),sQuery(id+"F0.wireOp",EDGE,"E42.bottom"),sQuery(id+"F0.wireOp",EDGE,"E42.top"),sQuery(id+"F0.wireOp",EDGE,"E42.left"),sQuery(id+"F0.wireOp",EDGE,"E42.right"),sQuery(id+"F0.wireOp",EDGE,"E43.bottom"),sQuery(id+"F0.wireOp",EDGE,"E43.top"),sQuery(id+"F0.wireOp",EDGE,"E43.left"),sQuery(id+"F0.wireOp",EDGE,"E43.right"),sQuery(id+"F0.wireOp",EDGE,"7093700b-8509-4908-bad7-ce82e1b1d340.1.0.0"),sQuery(id+"F0.wireOp",EDGE,"7093700b-8509-4908-bad7-ce82e1b1d340.1.0.2"),sQuery(id+"F0.wireOp",EDGE,"7093700b-8509-4908-bad7-ce82e1b1d340.1.0.3"),sQuery(id+"F0.wireOp",EDGE,"7093700b-8509-4908-bad7-ce82e1b1d340.1.0.5"),sQuery(id+"F0.wireOp",EDGE,"7093700b-8509-4908-bad7-ce82e1b1d340.1.0.6"),sQuery(id+"F0.wireOp",EDGE,"7093700b-8509-4908-bad7-ce82e1b1d340.1.0.7"),sQuery(id+"F0.wireOp",EDGE,"7093700b-8509-4908-bad7-ce82e1b1d340.1.0.8"),sQuery(id+"F0.wireOp",EDGE,"7093700b-8509-4908-bad7-ce82e1b1d340.1.0.9"),sQuery(id+"F0.wireOp",EDGE,"7093700b-8509-4908-bad7-ce82e1b1d340.1.0.12"),sQuery(id+"F0.wireOp",EDGE,"7093700b-8509-4908-bad7-ce82e1b1d340.1.0.13"),sQuery(id+"F0.wireOp",EDGE,"7093700b-8509-4908-bad7-ce82e1b1d340.1.0.14"),sQuery(id+"F0.wireOp",EDGE,"7093700b-8509-4908-bad7-ce82e1b1d340.1.0.15"),sQuery(id+"F0.wireOp",EDGE,"7093700b-8509-4908-bad7-ce82e1b1d340.1.0.16"),sQuery(id+"F0.wireOp",EDGE,"7093700b-8509-4908-bad7-ce82e1b1d340.1.0.17"),sQuery(id+"F0.wireOp",EDGE,"7093700b-8509-4908-bad7-ce82e1b1d340.1.0.18"),sQuery(id+"F0.wireOp",EDGE,"7093700b-8509-4908-bad7-ce82e1b1d340.1.0.19"),sQuery(id+"F0.wireOp",EDGE,"7093700b-8509-4908-bad7-ce82e1b1d340.1.0.20"),sQuery(id+"F0.wireOp",EDGE,"7093700b-8509-4908-bad7-ce82e1b1d340.1.0.21"),sQuery(id+"F0.wireOp",EDGE,"7093700b-8509-4908-bad7-ce82e1b1d340.2.0.0"),sQuery(id+"F0.wireOp",EDGE,"7093700b-8509-4908-bad7-ce82e1b1d340.2.0.2"),sQuery(id+"F0.wireOp",EDGE,"7093700b-8509-4908-bad7-ce82e1b1d340.2.0.3"),sQuery(id+"F0.wireOp",EDGE,"7093700b-8509-4908-bad7-ce82e1b1d340.2.0.5"),sQuery(id+"F0.wireOp",EDGE,"7093700b-8509-4908-bad7-ce82e1b1d340.2.0.6"),sQuery(id+"F0.wireOp",EDGE,"7093700b-8509-4908-bad7-ce82e1b1d340.2.0.7"),sQuery(id+"F0.wireOp",EDGE,"7093700b-8509-4908-bad7-ce82e1b1d340.2.0.8"),sQuery(id+"F0.wireOp",EDGE,"7093700b-8509-4908-bad7-ce82e1b1d340.2.0.9"),sQuery(id+"F0.wireOp",EDGE,"7093700b-8509-4908-bad7-ce82e1b1d340.2.0.12"),sQuery(id+"F0.wireOp",EDGE,"7093700b-8509-4908-bad7-ce82e1b1d340.2.0.13"),sQuery(id+"F0.wireOp",EDGE,"7093700b-8509-4908-bad7-ce82e1b1d340.2.0.14"),sQuery(id+"F0.wireOp",EDGE,"7093700b-8509-4908-bad7-ce82e1b1d340.2.0.15"),sQuery(id+"F0.wireOp",EDGE,"7093700b-8509-4908-bad7-ce82e1b1d340.2.0.16"),sQuery(id+"F0.wireOp",EDGE,"7093700b-8509-4908-bad7-ce82e1b1d340.2.0.17"),sQuery(id+"F0.wireOp",EDGE,"7093700b-8509-4908-bad7-ce82e1b1d340.2.0.18"),sQuery(id+"F0.wireOp",EDGE,"7093700b-8509-4908-bad7-ce82e1b1d340.2.0.19"),sQuery(id+"F0.wireOp",EDGE,"7093700b-8509-4908-bad7-ce82e1b1d340.2.0.20"),sQuery(id+"F0.wireOp",EDGE,"7093700b-8509-4908-bad7-ce82e1b1d340.2.0.21"),sQuery(id+"F0.wireOp",EDGE,"c973f7c2-3bf7-4545-afce-7af64f458de9.1.0.0"),sQuery(id+"F0.wireOp",EDGE,"c973f7c2-3bf7-4545-afce-7af64f458de9.1.0.1"),sQuery(id+"F0.wireOp",EDGE,"c973f7c2-3bf7-4545-afce-7af64f458de9.1.0.2"),sQuery(id+"F0.wireOp",EDGE,"c973f7c2-3bf7-4545-afce-7af64f458de9.1.0.4"),sQuery(id+"F0.wireOp",EDGE,"c973f7c2-3bf7-4545-afce-7af64f458de9.1.0.6"),sQuery(id+"F0.wireOp",EDGE,"c973f7c2-3bf7-4545-afce-7af64f458de9.1.0.7"),sQuery(id+"F0.wireOp",EDGE,"c973f7c2-3bf7-4545-afce-7af64f458de9.1.0.9"),sQuery(id+"F0.wireOp",EDGE,"c973f7c2-3bf7-4545-afce-7af64f458de9.1.0.10"),sQuery(id+"F0.wireOp",EDGE,"c973f7c2-3bf7-4545-afce-7af64f458de9.1.0.12"),sQuery(id+"F0.wireOp",EDGE,"c973f7c2-3bf7-4545-afce-7af64f458de9.1.0.14"),sQuery(id+"F0.wireOp",EDGE,"c973f7c2-3bf7-4545-afce-7af64f458de9.1.0.16"),sQuery(id+"F0.wireOp",EDGE,"c973f7c2-3bf7-4545-afce-7af64f458de9.1.0.18"),sQuery(id+"F0.wireOp",EDGE,"c973f7c2-3bf7-4545-afce-7af64f458de9.1.0.19"),sQuery(id+"F0.wireOp",EDGE,"c973f7c2-3bf7-4545-afce-7af64f458de9.1.0.20"),sQuery(id+"F0.wireOp",EDGE,"c973f7c2-3bf7-4545-afce-7af64f458de9.1.0.26"),sQuery(id+"F0.wireOp",EDGE,"c973f7c2-3bf7-4545-afce-7af64f458de9.1.0.28"),sQuery(id+"F0.wireOp",EDGE,"c973f7c2-3bf7-4545-afce-7af64f458de9.1.0.29"),sQuery(id+"F0.wireOp",EDGE,"c973f7c2-3bf7-4545-afce-7af64f458de9.1.0.30"),sQuery(id+"F0.wireOp",EDGE,"c973f7c2-3bf7-4545-afce-7af64f458de9.2.0.0"),sQuery(id+"F0.wireOp",EDGE,"c973f7c2-3bf7-4545-afce-7af64f458de9.2.0.1"),sQuery(id+"F0.wireOp",EDGE,"c973f7c2-3bf7-4545-afce-7af64f458de9.2.0.2"),sQuery(id+"F0.wireOp",EDGE,"c973f7c2-3bf7-4545-afce-7af64f458de9.2.0.4"),sQuery(id+"F0.wireOp",EDGE,"c973f7c2-3bf7-4545-afce-7af64f458de9.2.0.6"),sQuery(id+"F0.wireOp",EDGE,"c973f7c2-3bf7-4545-afce-7af64f458de9.2.0.7"),sQuery(id+"F0.wireOp",EDGE,"c973f7c2-3bf7-4545-afce-7af64f458de9.2.0.9"),sQuery(id+"F0.wireOp",EDGE,"c973f7c2-3bf7-4545-afce-7af64f458de9.2.0.10"),sQuery(id+"F0.wireOp",EDGE,"c973f7c2-3bf7-4545-afce-7af64f458de9.2.0.12"),sQuery(id+"F0.wireOp",EDGE,"c973f7c2-3bf7-4545-afce-7af64f458de9.2.0.14"),sQuery(id+"F0.wireOp",EDGE,"c973f7c2-3bf7-4545-afce-7af64f458de9.2.0.16"),sQuery(id+"F0.wireOp",EDGE,"c973f7c2-3bf7-4545-afce-7af64f458de9.2.0.18"),sQuery(id+"F0.wireOp",EDGE,"c973f7c2-3bf7-4545-afce-7af64f458de9.2.0.19"),sQuery(id+"F0.wireOp",EDGE,"c973f7c2-3bf7-4545-afce-7af64f458de9.2.0.20"),sQuery(id+"F0.wireOp",EDGE,"c973f7c2-3bf7-4545-afce-7af64f458de9.2.0.26"),sQuery(id+"F0.wireOp",EDGE,"c973f7c2-3bf7-4545-afce-7af64f458de9.2.0.28"),sQuery(id+"F0.wireOp",EDGE,"c973f7c2-3bf7-4545-afce-7af64f458de9.2.0.29"),sQuery(id+"F0.wireOp",EDGE,"c973f7c2-3bf7-4545-afce-7af64f458de9.2.0.30"),sQuery(id+"F0.wireOp",EDGE,"E44.left"),sQuery(id+"F0.wireOp",EDGE,"E44.right"),sQuery(id+"F0.wireOp",EDGE,"E45.left"),sQuery(id+"F0.wireOp",EDGE,"E45.right"),sQuery(id+"F0.wireOp",EDGE,"E46"),sQuery(id+"F0.wireOp",EDGE,"E47"),sQuery(id+"F0.wireOp",EDGE,"E48"),sQuery(id+"F0.wireOp",EDGE,"E49")])],"isStart":false});
            var sketch = newSketch(context, id + "F24", { "sketchPlane" : qUnion([Q0])});
            skLineSegment(sketch, "E172.bottom", {"start": v(-149.5, 17.96) * mm, "end": v(-139.5, 17.96) * mm});
            skLineSegment(sketch, "E172.top", {"start": v(-149.5, -57.04) * mm, "end": v(-139.5, -57.04) * mm});
            skLineSegment(sketch, "E172.left", {"start": v(-149.5, 17.96) * mm, "end": v(-149.5, -57.04) * mm});
            skLineSegment(sketch, "E172.right", {"start": v(-139.5, 17.96) * mm, "end": v(-139.5, -57.04) * mm});
            skLineSegment(sketch, "E173.bottom", {"start": v(0.5, -57.04) * mm, "end": v(-9.5, -57.04) * mm});
            skLineSegment(sketch, "E173.top", {"start": v(0.5, 17.96) * mm, "end": v(-9.5, 17.96) * mm});
            skLineSegment(sketch, "E173.left", {"start": v(0.5, -57.04) * mm, "end": v(0.5, 17.96) * mm});
            skLineSegment(sketch, "E173.right", {"start": v(-9.5, -57.04) * mm, "end": v(-9.5, 17.96) * mm});
            skSolve(sketch);
        }
        {
            var Q0;
            Q0=makeQuery(id+"F24.imprint","IMPRINT",FACE,{"disambiguationData":[TD([[makeQuery(id+"F24.imprint","IMPRINT",EDGE,{"derivedFrom":sQuery(id+"F24.wireOp",EDGE,"E173.bottom")}),-1.0]])]});
            var Q1;
            Q1=makeQuery(id+"F24.imprint","IMPRINT",FACE,{"disambiguationData":[TD([[makeQuery(id+"F24.imprint","IMPRINT",EDGE,{"derivedFrom":sQuery(id+"F24.wireOp",EDGE,"E172.bottom")}),1.0]])]});
            extrude(context, id + "F25", {"entities" : qUnion([Q0, Q1]), "operationType" : NewBodyOperationType.ADD, "depth" : 4 * mm});
        }
        {
            var Q0;
            {var subQ0=sQuery(id+"F0.wireOp",EDGE,"E0.bottom");Q0=makeQuery(id+"F25.boolean.opBoolean","MERGE",FACE,{"derivedFrom":[makeQuery(id+"FcxvOkpkAmDw7ie_3.boolean.opBoolean","MERGE",FACE,{"derivedFrom":[makeQuery(id+"F3.boolean.opBoolean","MERGE",FACE,{"derivedFrom":[makeQuery(id+"F2.opExtrude","SWEPT_FACE",FACE,{"disambiguationData":[OSD([subQ0])]}),makeQuery(id+"F3.opExtrude","SWEPT_FACE",FACE,{"disambiguationData":[OSD([subQ0])]})]}),makeQuery(id+"FcxvOkpkAmDw7ie_3.opExtrude","SWEPT_FACE",FACE,{"disambiguationData":[OSD([sQuery(id+"FNICA6uDXxchBR6_3.wireOp",EDGE,"OznuT0um-5Ypx-SHlm-bkf4-iYFOqL2Sfz4i.bottom")])]})]}),makeQuery(id+"F25.opExtrude","SWEPT_FACE",FACE,{"disambiguationData":[OSD([sQuery(id+"F24.wireOp",EDGE,"E172.top")])]}),makeQuery(id+"F25.opExtrude","SWEPT_FACE",FACE,{"disambiguationData":[OSD([sQuery(id+"F24.wireOp",EDGE,"E173.bottom")])]})]});}
            var sketch = newSketch(context, id + "F26", { "sketchPlane" : qUnion([Q0])});
            skLineSegment(sketch, "E174.bottom", {"start": v(-149.5, 0) * mm, "end": v(-141.5, 0) * mm});
            skLineSegment(sketch, "E174.top", {"start": v(-149.5, 7) * mm, "end": v(-141.5, 7) * mm});
            skLineSegment(sketch, "E174.left", {"start": v(-149.5, 0) * mm, "end": v(-149.5, 7) * mm});
            skLineSegment(sketch, "E174.right", {"start": v(-141.5, 0) * mm, "end": v(-141.5, 7) * mm});
            skLineSegment(sketch, "E175.bottom", {"start": v(0.5, 0) * mm, "end": v(-7.5, 0) * mm});
            skLineSegment(sketch, "E175.top", {"start": v(0.5, 7) * mm, "end": v(-7.5, 7) * mm});
            skLineSegment(sketch, "E175.left", {"start": v(0.5, 0) * mm, "end": v(0.5, 7) * mm});
            skLineSegment(sketch, "E175.right", {"start": v(-7.5, 0) * mm, "end": v(-7.5, 7) * mm});
            skSolve(sketch);
        }
        {
            var Q0;
            Q0 = qSketchRegion(id + "F26", true);
            extrude(context, id + "F27", {"entities" : qUnion([Q0]), "operationType" : NewBodyOperationType.REMOVE, "oppositeDirection" : true, "depth" : 77.8 * mm});
        }
        {
            var Q0;
            {var subQ0=sQuery(id+"F0.wireOp",EDGE,"E0.right");var subQ1=sQuery(id+"F0.wireOp",EDGE,"E0.top");var subQ3=sQuery(id+"F0.wireOp",EDGE,"E0.bottom");var subQ5=sQuery(id+"F0.wireOp",EDGE,"E47");var subQ6=sQuery(id+"F0.wireOp",EDGE,"E46");var subQ7=sQuery(id+"F0.wireOp",EDGE,"E45.right");var subQ8=sQuery(id+"F0.wireOp",EDGE,"E45.left");var subQ9=sQuery(id+"F0.wireOp",EDGE,"E44.right");var subQ10=sQuery(id+"F0.wireOp",EDGE,"E44.left");var subQ11=sQuery(id+"F0.wireOp",EDGE,"c973f7c2-3bf7-4545-afce-7af64f458de9.2.0.30");var subQ12=sQuery(id+"F0.wireOp",EDGE,"c973f7c2-3bf7-4545-afce-7af64f458de9.2.0.0");var subQ13=sQuery(id+"F0.wireOp",EDGE,"c973f7c2-3bf7-4545-afce-7af64f458de9.2.0.29");var subQ16=sQuery(id+"F0.wireOp",EDGE,"c973f7c2-3bf7-4545-afce-7af64f458de9.2.0.10");var subQ17=sQuery(id+"F0.wireOp",EDGE,"c973f7c2-3bf7-4545-afce-7af64f458de9.2.0.28");var subQ20=sQuery(id+"F0.wireOp",EDGE,"c973f7c2-3bf7-4545-afce-7af64f458de9.2.0.18");var subQ21=sQuery(id+"F0.wireOp",EDGE,"c973f7c2-3bf7-4545-afce-7af64f458de9.2.0.26");var subQ24=sQuery(id+"F0.wireOp",EDGE,"c973f7c2-3bf7-4545-afce-7af64f458de9.2.0.1");var subQ25=sQuery(id+"F0.wireOp",EDGE,"c973f7c2-3bf7-4545-afce-7af64f458de9.2.0.19");var subQ27=sQuery(id+"F0.wireOp",EDGE,"c973f7c2-3bf7-4545-afce-7af64f458de9.2.0.9");var subQ30=sQuery(id+"F0.wireOp",EDGE,"c973f7c2-3bf7-4545-afce-7af64f458de9.2.0.4");var subQ34=sQuery(id+"F0.wireOp",EDGE,"c973f7c2-3bf7-4545-afce-7af64f458de9.2.0.2");var subQ35=sQuery(id+"F0.wireOp",EDGE,"c973f7c2-3bf7-4545-afce-7af64f458de9.2.0.7");var subQ37=sQuery(id+"F0.wireOp",EDGE,"c973f7c2-3bf7-4545-afce-7af64f458de9.2.0.16");var subQ39=sQuery(id+"F0.wireOp",EDGE,"c973f7c2-3bf7-4545-afce-7af64f458de9.2.0.20");var subQ41=sQuery(id+"F0.wireOp",EDGE,"c973f7c2-3bf7-4545-afce-7af64f458de9.2.0.12");var subQ43=sQuery(id+"F0.wireOp",EDGE,"c973f7c2-3bf7-4545-afce-7af64f458de9.2.0.14");var subQ44=sQuery(id+"F0.wireOp",EDGE,"c973f7c2-3bf7-4545-afce-7af64f458de9.2.0.6");var subQ45=sQuery(id+"F0.wireOp",EDGE,"c973f7c2-3bf7-4545-afce-7af64f458de9.1.0.30");var subQ46=sQuery(id+"F0.wireOp",EDGE,"c973f7c2-3bf7-4545-afce-7af64f458de9.1.0.0");var subQ47=sQuery(id+"F0.wireOp",EDGE,"c973f7c2-3bf7-4545-afce-7af64f458de9.1.0.29");var subQ50=sQuery(id+"F0.wireOp",EDGE,"c973f7c2-3bf7-4545-afce-7af64f458de9.1.0.10");var subQ51=sQuery(id+"F0.wireOp",EDGE,"c973f7c2-3bf7-4545-afce-7af64f458de9.1.0.28");var subQ54=sQuery(id+"F0.wireOp",EDGE,"c973f7c2-3bf7-4545-afce-7af64f458de9.1.0.18");var subQ55=sQuery(id+"F0.wireOp",EDGE,"c973f7c2-3bf7-4545-afce-7af64f458de9.1.0.26");var subQ58=sQuery(id+"F0.wireOp",EDGE,"c973f7c2-3bf7-4545-afce-7af64f458de9.1.0.1");var subQ59=sQuery(id+"F0.wireOp",EDGE,"c973f7c2-3bf7-4545-afce-7af64f458de9.1.0.19");var subQ61=sQuery(id+"F0.wireOp",EDGE,"c973f7c2-3bf7-4545-afce-7af64f458de9.1.0.9");var subQ64=sQuery(id+"F0.wireOp",EDGE,"c973f7c2-3bf7-4545-afce-7af64f458de9.1.0.4");var subQ68=sQuery(id+"F0.wireOp",EDGE,"c973f7c2-3bf7-4545-afce-7af64f458de9.1.0.2");var subQ69=sQuery(id+"F0.wireOp",EDGE,"c973f7c2-3bf7-4545-afce-7af64f458de9.1.0.7");var subQ71=sQuery(id+"F0.wireOp",EDGE,"c973f7c2-3bf7-4545-afce-7af64f458de9.1.0.16");var subQ73=sQuery(id+"F0.wireOp",EDGE,"c973f7c2-3bf7-4545-afce-7af64f458de9.1.0.20");var subQ75=sQuery(id+"F0.wireOp",EDGE,"c973f7c2-3bf7-4545-afce-7af64f458de9.1.0.12");var subQ77=sQuery(id+"F0.wireOp",EDGE,"c973f7c2-3bf7-4545-afce-7af64f458de9.1.0.14");var subQ78=sQuery(id+"F0.wireOp",EDGE,"c973f7c2-3bf7-4545-afce-7af64f458de9.1.0.6");var subQ79=sQuery(id+"F0.wireOp",EDGE,"7093700b-8509-4908-bad7-ce82e1b1d340.2.0.21");var subQ81=sQuery(id+"F0.wireOp",EDGE,"7093700b-8509-4908-bad7-ce82e1b1d340.2.0.20");var subQ82=sQuery(id+"F0.wireOp",EDGE,"7093700b-8509-4908-bad7-ce82e1b1d340.2.0.12");var subQ83=sQuery(id+"F0.wireOp",EDGE,"7093700b-8509-4908-bad7-ce82e1b1d340.2.0.15");var subQ86=sQuery(id+"F0.wireOp",EDGE,"7093700b-8509-4908-bad7-ce82e1b1d340.2.0.13");var subQ87=sQuery(id+"F0.wireOp",EDGE,"7093700b-8509-4908-bad7-ce82e1b1d340.2.0.17");var subQ90=sQuery(id+"F0.wireOp",EDGE,"7093700b-8509-4908-bad7-ce82e1b1d340.2.0.19");var subQ91=sQuery(id+"F0.wireOp",EDGE,"7093700b-8509-4908-bad7-ce82e1b1d340.2.0.18");var subQ93=sQuery(id+"F0.wireOp",EDGE,"7093700b-8509-4908-bad7-ce82e1b1d340.2.0.16");var subQ97=sQuery(id+"F0.wireOp",EDGE,"7093700b-8509-4908-bad7-ce82e1b1d340.2.0.2");var subQ99=sQuery(id+"F0.wireOp",EDGE,"7093700b-8509-4908-bad7-ce82e1b1d340.2.0.3");var subQ102=sQuery(id+"F0.wireOp",EDGE,"7093700b-8509-4908-bad7-ce82e1b1d340.2.0.0");var subQ104=sQuery(id+"F0.wireOp",EDGE,"7093700b-8509-4908-bad7-ce82e1b1d340.2.0.5");var subQ105=sQuery(id+"F0.wireOp",EDGE,"7093700b-8509-4908-bad7-ce82e1b1d340.2.0.14");var subQ108=sQuery(id+"F0.wireOp",EDGE,"7093700b-8509-4908-bad7-ce82e1b1d340.2.0.6");var subQ110=sQuery(id+"F0.wireOp",EDGE,"7093700b-8509-4908-bad7-ce82e1b1d340.2.0.9");var subQ111=sQuery(id+"F0.wireOp",EDGE,"7093700b-8509-4908-bad7-ce82e1b1d340.2.0.8");var subQ112=sQuery(id+"F0.wireOp",EDGE,"7093700b-8509-4908-bad7-ce82e1b1d340.2.0.7");var subQ113=sQuery(id+"F0.wireOp",EDGE,"E33.left");var subQ114=sQuery(id+"F0.wireOp",EDGE,"E32.right");var subQ115=sQuery(id+"F0.wireOp",EDGE,"E32.left");var subQ116=sQuery(id+"F0.wireOp",EDGE,"E31.top");var subQ117=sQuery(id+"F0.wireOp",EDGE,"E31.bottom");var subQ118=sQuery(id+"F0.wireOp",EDGE,"E19.right");var subQ119=sQuery(id+"F0.wireOp",EDGE,"E19.top");var subQ121=sQuery(id+"F0.wireOp",EDGE,"E35.trimOffspring");var subQ124=sQuery(id+"F0.wireOp",EDGE,"E19.bottom");var subQ126=sQuery(id+"F0.wireOp",EDGE,"E37.trimOffspring");var subQ128=sQuery(id+"F0.wireOp",EDGE,"E19.left");var subQ132=sQuery(id+"F0.wireOp",EDGE,"E34.trimOffspring");var subQ135=sQuery(id+"F0.wireOp",EDGE,"E27.trimOffspring");var subQ136=sQuery(id+"F0.wireOp",EDGE,"E40.trimOffspring");var subQ139=sQuery(id+"F0.wireOp",EDGE,"E26.trimOffspring");var subQ142=sQuery(id+"F0.wireOp",EDGE,"E24.trimOffspring");var subQ146=sQuery(id+"F0.wireOp",EDGE,"E23.trimOffspring");var subQ147=sQuery(id+"F0.wireOp",EDGE,"E30.trimOffspring");var subQ148=sQuery(id+"F0.wireOp",EDGE,"E22.right");var subQ149=sQuery(id+"F0.wireOp",EDGE,"E29.trimOffspring");var subQ150=sQuery(id+"F0.wireOp",EDGE,"E22.left");var subQ151=sQuery(id+"F0.wireOp",EDGE,"E28.trimOffspring");var subQ152=sQuery(id+"F0.wireOp",EDGE,"E21.right");var subQ153=sQuery(id+"F0.wireOp",EDGE,"E21.left");var subQ154=sQuery(id+"F0.wireOp",EDGE,"E20.top");var subQ155=sQuery(id+"F0.wireOp",EDGE,"E25.trimOffspring");var subQ156=sQuery(id+"F0.wireOp",EDGE,"E20.bottom");var subQ157=sQuery(id+"F0.wireOp",EDGE,"E18.right");var subQ158=sQuery(id+"F0.wireOp",EDGE,"E18.top");var subQ162=sQuery(id+"F0.wireOp",EDGE,"E18.bottom");var subQ165=sQuery(id+"F0.wireOp",EDGE,"E14.top");var subQ168=sQuery(id+"F0.wireOp",EDGE,"E14.bottom");var subQ171=sQuery(id+"F0.wireOp",EDGE,"E33.right");var subQ174=sQuery(id+"F0.wireOp",EDGE,"7093700b-8509-4908-bad7-ce82e1b1d340.1.0.16");var subQ175=sQuery(id+"F0.wireOp",EDGE,"E14.right");var subQ176=sQuery(id+"F0.wireOp",EDGE,"E14.left");var subQ177=sQuery(id+"F0.wireOp",EDGE,"E18.left");var subQ180=sQuery(id+"F0.wireOp",EDGE,"E36.trimOffspring");var subQ181=sQuery(id+"F0.wireOp",EDGE,"E38.trimOffspring");var subQ185=sQuery(id+"F0.wireOp",EDGE,"7093700b-8509-4908-bad7-ce82e1b1d340.1.0.17");var subQ186=sQuery(id+"F0.wireOp",EDGE,"7093700b-8509-4908-bad7-ce82e1b1d340.1.0.20");var subQ193=sQuery(id+"F0.wireOp",EDGE,"7093700b-8509-4908-bad7-ce82e1b1d340.1.0.19");var subQ200=sQuery(id+"F0.wireOp",EDGE,"E39.trimOffspring");var subQ201=sQuery(id+"F0.wireOp",EDGE,"E41.trimOffspring");var subQ202=sQuery(id+"F0.wireOp",EDGE,"E42.left");var subQ203=sQuery(id+"F0.wireOp",EDGE,"E42.bottom");var subQ206=sQuery(id+"F0.wireOp",EDGE,"E42.right");var subQ208=sQuery(id+"F0.wireOp",EDGE,"E42.top");var subQ212=sQuery(id+"F0.wireOp",EDGE,"E43.left");var subQ213=sQuery(id+"F0.wireOp",EDGE,"E43.bottom");var subQ216=sQuery(id+"F0.wireOp",EDGE,"E43.right");var subQ218=sQuery(id+"F0.wireOp",EDGE,"E43.top");var subQ222=sQuery(id+"F0.wireOp",EDGE,"7093700b-8509-4908-bad7-ce82e1b1d340.1.0.0");var subQ223=sQuery(id+"F0.wireOp",EDGE,"7093700b-8509-4908-bad7-ce82e1b1d340.1.0.2");var subQ226=sQuery(id+"F0.wireOp",EDGE,"7093700b-8509-4908-bad7-ce82e1b1d340.1.0.9");var subQ228=sQuery(id+"F0.wireOp",EDGE,"7093700b-8509-4908-bad7-ce82e1b1d340.1.0.15");var subQ230=sQuery(id+"F0.wireOp",EDGE,"7093700b-8509-4908-bad7-ce82e1b1d340.1.0.8");var subQ232=sQuery(id+"F0.wireOp",EDGE,"7093700b-8509-4908-bad7-ce82e1b1d340.1.0.3");var subQ233=sQuery(id+"F0.wireOp",EDGE,"7093700b-8509-4908-bad7-ce82e1b1d340.1.0.5");var subQ234=sQuery(id+"F0.wireOp",EDGE,"7093700b-8509-4908-bad7-ce82e1b1d340.1.0.6");var subQ235=sQuery(id+"F0.wireOp",EDGE,"7093700b-8509-4908-bad7-ce82e1b1d340.1.0.7");var subQ236=sQuery(id+"F0.wireOp",EDGE,"7093700b-8509-4908-bad7-ce82e1b1d340.1.0.12");var subQ237=sQuery(id+"F0.wireOp",EDGE,"7093700b-8509-4908-bad7-ce82e1b1d340.1.0.13");var subQ238=sQuery(id+"F0.wireOp",EDGE,"7093700b-8509-4908-bad7-ce82e1b1d340.1.0.14");var subQ246=sQuery(id+"F0.wireOp",EDGE,"7093700b-8509-4908-bad7-ce82e1b1d340.1.0.18");var subQ251=sQuery(id+"F0.wireOp",EDGE,"7093700b-8509-4908-bad7-ce82e1b1d340.1.0.21");var subQ255=sQuery(id+"F0.wireOp",EDGE,"E49");var subQ256=sQuery(id+"F0.wireOp",EDGE,"E48");var subQ257=sQuery(id+"F0.wireOp",EDGE,"E0.left");var subQ258=makeQuery(id+"F2.opExtrude","CAP_FACE",FACE,{"disambiguationData":[OSD([subQ3,subQ1,subQ257,subQ0,sQuery(id+"F0.wireOp",EDGE,"6XQCNLW2-68Wz-nC9p-wT4x-b90YEvEmSNLj"),sQuery(id+"F0.wireOp",EDGE,"E3"),sQuery(id+"F0.wireOp",EDGE,"E4"),sQuery(id+"F0.wireOp",EDGE,"E7"),sQuery(id+"F0.wireOp",EDGE,"E8"),sQuery(id+"F0.wireOp",EDGE,"E9"),sQuery(id+"F0.wireOp",EDGE,"E10"),sQuery(id+"F0.wireOp",EDGE,"E11"),sQuery(id+"F0.wireOp",EDGE,"E12"),sQuery(id+"F0.wireOp",EDGE,"E13"),subQ168,subQ165,subQ176,subQ175,sQuery(id+"F0.wireOp",EDGE,"E15"),sQuery(id+"F0.wireOp",EDGE,"E16"),subQ162,subQ158,subQ177,subQ157,subQ156,subQ154,subQ153,subQ152,subQ150,subQ148,subQ146,subQ142,subQ155,subQ139,subQ135,subQ151,subQ149,subQ147,subQ124,subQ119,subQ128,subQ118,subQ117,subQ116,subQ115,subQ114,subQ113,subQ171,subQ132,subQ121,subQ180,subQ126,subQ181,subQ200,subQ136,subQ201,subQ203,subQ208,subQ202,subQ206,subQ213,subQ218,subQ212,subQ216,subQ222,subQ223,subQ232,subQ233,subQ234,subQ235,subQ230,subQ226,subQ236,subQ237,subQ238,subQ228,subQ174,subQ185,subQ246,subQ193,subQ186,subQ251,subQ102,subQ97,subQ99,subQ104,subQ108,subQ112,subQ111,subQ110,subQ82,subQ86,subQ105,subQ83,subQ93,subQ87,subQ91,subQ90,subQ81,subQ79,subQ46,subQ58,subQ68,subQ64,subQ78,subQ69,subQ61,subQ50,subQ75,subQ77,subQ71,subQ54,subQ59,subQ73,subQ55,subQ51,subQ47,subQ45,subQ12,subQ24,subQ34,subQ30,subQ44,subQ35,subQ27,subQ16,subQ41,subQ43,subQ37,subQ20,subQ25,subQ39,subQ21,subQ17,subQ13,subQ11,subQ10,subQ9,subQ8,subQ7,subQ6,subQ5,subQ256,subQ255])],"isStart":true});Q0=makeQuery(id+"FcxvOkpkAmDw7ie_3.boolean.opBoolean","MERGE",FACE,{"derivedFrom":[makeQuery(id+"F22.boolean.opBoolean","SPLIT",FACE,{"disambiguationData":[TD([makeQuery(id+"F2.opExtrude","SWEPT_FACE",FACE,{"disambiguationData":[OSD([subQ257])]})])],"derivedFrom":subQ258}),makeQuery(id+"F22.boolean.opBoolean","SPLIT",FACE,{"disambiguationData":[TD([makeQuery(id+"F2.opExtrude","SWEPT_FACE",FACE,{"disambiguationData":[OSD([subQ0])]})])],"derivedFrom":subQ258}),makeQuery(id+"FcxvOkpkAmDw7ie_3.opExtrude","CAP_FACE",FACE,{"disambiguationData":[OSD([sQuery(id+"FNICA6uDXxchBR6_3.wireOp",EDGE,"OznuT0um-5Ypx-SHlm-bkf4-iYFOqL2Sfz4i.bottom"),sQuery(id+"FNICA6uDXxchBR6_3.wireOp",EDGE,"OznuT0um-5Ypx-SHlm-bkf4-iYFOqL2Sfz4i.top"),sQuery(id+"FNICA6uDXxchBR6_3.wireOp",EDGE,"OznuT0um-5Ypx-SHlm-bkf4-iYFOqL2Sfz4i.left"),sQuery(id+"FNICA6uDXxchBR6_3.wireOp",EDGE,"OznuT0um-5Ypx-SHlm-bkf4-iYFOqL2Sfz4i.right")])],"isStart":false}),makeQuery(id+"FcxvOkpkAmDw7ie_3.opExtrude","CAP_FACE",FACE,{"disambiguationData":[OSD([sQuery(id+"FNICA6uDXxchBR6_3.wireOp",EDGE,"YSd4T3NJ-1L5Y-MwVD-52kg-DvB7oUMf2wlW.bottom"),sQuery(id+"FNICA6uDXxchBR6_3.wireOp",EDGE,"YSd4T3NJ-1L5Y-MwVD-52kg-DvB7oUMf2wlW.top"),sQuery(id+"FNICA6uDXxchBR6_3.wireOp",EDGE,"YSd4T3NJ-1L5Y-MwVD-52kg-DvB7oUMf2wlW.left"),sQuery(id+"FNICA6uDXxchBR6_3.wireOp",EDGE,"YSd4T3NJ-1L5Y-MwVD-52kg-DvB7oUMf2wlW.right")])],"isStart":false}),makeQuery(id+"FcxvOkpkAmDw7ie_3.opExtrude","CAP_FACE",FACE,{"disambiguationData":[OSD([sQuery(id+"FNICA6uDXxchBR6_3.wireOp",EDGE,"awoJ12up-LfxG-riiH-PCTd-TFvWrLSTyvKZ.bottom"),sQuery(id+"FNICA6uDXxchBR6_3.wireOp",EDGE,"awoJ12up-LfxG-riiH-PCTd-TFvWrLSTyvKZ.top"),sQuery(id+"FNICA6uDXxchBR6_3.wireOp",EDGE,"awoJ12up-LfxG-riiH-PCTd-TFvWrLSTyvKZ.left"),sQuery(id+"FNICA6uDXxchBR6_3.wireOp",EDGE,"awoJ12up-LfxG-riiH-PCTd-TFvWrLSTyvKZ.right")])],"isStart":false}),makeQuery(id+"FcxvOkpkAmDw7ie_3.opExtrude","CAP_FACE",FACE,{"disambiguationData":[OSD([sQuery(id+"FNICA6uDXxchBR6_3.wireOp",EDGE,"WfW6qyGR-5Y5B-en90-Dwp4-fLCMDk8WttTC.bottom"),sQuery(id+"FNICA6uDXxchBR6_3.wireOp",EDGE,"WfW6qyGR-5Y5B-en90-Dwp4-fLCMDk8WttTC.top"),sQuery(id+"FNICA6uDXxchBR6_3.wireOp",EDGE,"WfW6qyGR-5Y5B-en90-Dwp4-fLCMDk8WttTC.left"),sQuery(id+"FNICA6uDXxchBR6_3.wireOp",EDGE,"WfW6qyGR-5Y5B-en90-Dwp4-fLCMDk8WttTC.right")])],"isStart":false})]});}
            var sketch = newSketch(context, id + "F28", { "sketchPlane" : qUnion([Q0])});
            skLineSegment(sketch, "E176.bottom", {"start": v(-141.5, -17.96) * mm, "end": v(-7.5, -17.96) * mm});
            skLineSegment(sketch, "E176.top", {"start": v(-141.5, -15.46) * mm, "end": v(-7.5, -15.46) * mm});
            skLineSegment(sketch, "E176.left", {"start": v(-141.5, -17.96) * mm, "end": v(-141.5, -15.46) * mm});
            skLineSegment(sketch, "E176.right", {"start": v(-7.5, -17.96) * mm, "end": v(-7.5, -15.46) * mm});
            skSolve(sketch);
        }
        {
            var Q0;
            Q0 = qSketchRegion(id + "F28", true);
            extrude(context, id + "F29", {"entities" : qUnion([Q0]), "operationType" : NewBodyOperationType.REMOVE, "oppositeDirection" : true, "depth" : 3 * mm});
        }
        {
            var Q0;
            Q0=qCreatedBy(makeId("Top.planeOp"),FACE);
            var sketch = newSketch(context, id + "F30", { "sketchPlane" : qUnion([Q0])});
            skCircle(sketch, "E177", {"center": v(-177.94, 31.78) * mm, "radius": 4.9 * mm});
            skSolve(sketch);
        }
        {
            var Q0;
            Q0=makeQuery(id+"F30.imprint","IMPRINT",FACE,{"disambiguationData":[TD([[makeQuery(id+"F30.imprint","IMPRINT",EDGE,{"derivedFrom":sQuery(id+"F30.wireOp",EDGE,"E177")}),1.0]])]});
            extrude(context, id + "F31", {"entities" : qUnion([Q0]), "depth" : 4 * mm});
        }
        {
            var Q0;
            Q0=makeQuery(id+"F31.opExtrude","CAP_FACE",FACE,{"disambiguationData":[OSD([sQuery(id+"F30.wireOp",EDGE,"E177")])],"isStart":false});
            var sketch = newSketch(context, id + "F32", { "sketchPlane" : qUnion([Q0])});
            skCircle(sketch, "E178", {"center": v(-177.94, 31.78) * mm, "radius": 3.5 * mm});
            skSolve(sketch);
        }
        {
            var Q0;
            Q0=makeQuery(id+"F32.imprint","IMPRINT",FACE,{"disambiguationData":[TD([[makeQuery(id+"F32.imprint","IMPRINT",EDGE,{"derivedFrom":sQuery(id+"F32.wireOp",EDGE,"E178")}),1.0]])]});
            extrude(context, id + "F33", {"entities" : qUnion([Q0]), "operationType" : NewBodyOperationType.ADD, "depth" : 6 * mm});
        }
        {
            var Q0;
            Q0=makeQuery(id+"F31.opExtrude","CAP_FACE",FACE,{"disambiguationData":[OSD([sQuery(id+"F30.wireOp",EDGE,"E177")])],"isStart":true});
            var sketch = newSketch(context, id + "F34", { "sketchPlane" : qUnion([Q0])});
            skCircle(sketch, "E179", {"center": v(-177.94, -31.78) * mm, "radius": 6 * mm});
            skSolve(sketch);
        }
        {
            var Q0;
            Q0=makeQuery(id+"F34.imprint","IMPRINT",FACE,{"disambiguationData":[TD([[makeQuery(id+"F34.imprint","IMPRINT",EDGE,{"derivedFrom":sQuery(id+"F34.wireOp",EDGE,"E179")}),1.0]])]});
            extrude(context, id + "F35", {"entities" : qUnion([Q0]), "operationType" : NewBodyOperationType.ADD, "oppositeDirection" : true, "depth" : 1 * mm});
        }
        {
            var Q0;
            Q0=makeQuery(id+"F31.opExtrude","CAP_FACE",FACE,{"disambiguationData":[OSD([sQuery(id+"F30.wireOp",EDGE,"E177")])],"isStart":true});
            var sketch = newSketch(context, id + "F36", { "sketchPlane" : qUnion([Q0])});
            skLineSegment(sketch, "E180.bottom", {"start": v(-176.94, -33.03) * mm, "end": v(-178.94, -33.03) * mm});
            skLineSegment(sketch, "E180.top", {"start": v(-176.94, -30.53) * mm, "end": v(-178.94, -30.53) * mm});
            skLineSegment(sketch, "E180.left", {"start": v(-176.94, -33.03) * mm, "end": v(-176.94, -30.53) * mm});
            skLineSegment(sketch, "E180.right", {"start": v(-178.94, -33.03) * mm, "end": v(-178.94, -30.53) * mm});
            skPoint(sketch, "E180.middle", {"position": v(-177.94, -31.78) * mm});
            skSolve(sketch);
        }
        {
            var Q0;
            Q0=makeQuery(id+"F36.imprint","IMPRINT",FACE,{"disambiguationData":[TD([[makeQuery(id+"F36.imprint","IMPRINT",EDGE,{"derivedFrom":sQuery(id+"F36.wireOp",EDGE,"E180.bottom")}),-1.0]])]});
            extrude(context, id + "F37", {"entities" : qUnion([Q0]), "operationType" : NewBodyOperationType.REMOVE, "oppositeDirection" : true, "depth" : 2.5 * mm});
        }
        {
            var Q0;
            Q0=makeQuery(id+"F31.opExtrude","CAP_EDGE",EDGE,{"disambiguationData":[OSD([sQuery(id+"F30.wireOp",EDGE,"E177")])],"isStart":false});
            fillet(context, id + "F38", {"entities" : qUnion([Q0]), "radius" : 1 * mm, "tangentPropagation" : true, "allowEdgeOverflow" : false});
        }
        {
            var Q0;
            Q0=makeQuery(id+"F33.opExtrude","CAP_EDGE",EDGE,{"disambiguationData":[OSD([sQuery(id+"F32.wireOp",EDGE,"E178")])],"isStart":false});
            fillet(context, id + "F39", {"entities" : qUnion([Q0]), "radius" : 0.5 * mm, "tangentPropagation" : true, "allowEdgeOverflow" : false});
        }
        {
            var Q0;
            Q0=qCreatedBy(makeId("Top.planeOp"),FACE);
            var sketch = newSketch(context, id + "F40", { "sketchPlane" : qUnion([Q0])});
            skCircle(sketch, "E181", {"center": v(-112.45, -89.06) * mm, "radius": 3.1 * mm});
            skCircle(sketch, "E182", {"center": v(-112.45, -89.06) * mm, "radius": 3.75 * mm});
            skSolve(sketch);
        }
        {
            var Q0;
            Q0=makeQuery(id+"F40.imprint","IMPRINT",FACE,{"disambiguationData":[TD([[makeQuery(id+"F40.imprint","IMPRINT",EDGE,{"derivedFrom":sQuery(id+"F40.wireOp",EDGE,"E181")}),-1.0]])]});
            extrude(context, id + "F41", {"entities" : qUnion([Q0]), "depth" : 12 * mm});
        }
        {
            var Q0;
            Q0=makeQuery(id+"F41.opExtrude","CAP_FACE",FACE,{"disambiguationData":[OSD([sQuery(id+"F40.wireOp",EDGE,"E181"),sQuery(id+"F40.wireOp",EDGE,"E182")])],"isStart":true});
            var sketch = newSketch(context, id + "F42", { "sketchPlane" : qUnion([Q0])});
            skCircle(sketch, "E183", {"center": v(-112.45, 89.06) * mm, "radius": 4.5 * mm});
            skSolve(sketch);
        }
        {
            var Q0;
            Q0=makeQuery(id+"F42.imprint","IMPRINT",FACE,{"disambiguationData":[TD([[makeQuery(id+"F42.imprint","IMPRINT",EDGE,{"derivedFrom":sQuery(id+"F42.wireOp",EDGE,"E183")}),1.0]])]});
            extrude(context, id + "F43", {"entities" : qUnion([Q0]), "operationType" : NewBodyOperationType.ADD, "oppositeDirection" : true, "depth" : 13 * mm});
        }
        {
            var Q0;
            {var subQ0=sQuery(id+"F40.wireOp",EDGE,"E182");Q0=makeQuery(id+"F43.boolean.opBoolean","MERGE",FACE,{"derivedFrom":[makeQuery(id+"F41.opExtrude","CAP_FACE",FACE,{"disambiguationData":[OSD([sQuery(id+"F40.wireOp",EDGE,"E181"),subQ0])],"isStart":true}),makeQuery(id+"F43.opExtrude","CAP_FACE",FACE,{"disambiguationData":[OSD([subQ0,sQuery(id+"F42.wireOp",EDGE,"E183")])],"isStart":true})]});}
            var sketch = newSketch(context, id + "F44", { "sketchPlane" : qUnion([Q0])});
            skLineSegment(sketch, "E184.bottom", {"start": v(-102.45, 84.06) * mm, "end": v(-122.45, 84.06) * mm});
            skLineSegment(sketch, "E184.top", {"start": v(-102.45, 94.06) * mm, "end": v(-122.45, 94.06) * mm});
            skLineSegment(sketch, "E184.left", {"start": v(-102.45, 84.06) * mm, "end": v(-102.45, 94.06) * mm});
            skLineSegment(sketch, "E184.right", {"start": v(-122.45, 84.06) * mm, "end": v(-122.45, 94.06) * mm});
            skPoint(sketch, "E184.middle", {"position": v(-112.45, 89.06) * mm});
            skCircle(sketch, "E185", {"center": v(-119.45, 89.06) * mm, "radius": 1 * mm});
            skPoint(sketch, "E185.centerSnap0", {"position": v(-122.45, 89.06) * mm});
            skCircle(sketch, "E186", {"center": v(-105.45, 89.06) * mm, "radius": 1 * mm});
            skSolve(sketch);
        }
        {
            var Q0;
            Q0=makeQuery(id+"F44.imprint","IMPRINT",FACE,{"disambiguationData":[TD([[makeQuery(id+"F44.imprint","IMPRINT",EDGE,{"derivedFrom":sQuery(id+"F44.wireOp",EDGE,"E184.bottom")}),-1.0]])]});
            extrude(context, id + "F45", {"entities" : qUnion([Q0]), "operationType" : NewBodyOperationType.ADD, "oppositeDirection" : true, "depth" : 2 * mm});
        }
        {
            var Q0;
            Q0=makeQuery(id+"F3.opExtrude","CAP_FACE",FACE,{"disambiguationData":[OSD([sQuery(id+"F0.wireOp",EDGE,"E0.bottom"),sQuery(id+"F0.wireOp",EDGE,"E0.top"),sQuery(id+"F0.wireOp",EDGE,"E0.left"),sQuery(id+"F0.wireOp",EDGE,"E0.right"),sQuery(id+"F0.wireOp",EDGE,"6XQCNLW2-68Wz-nC9p-wT4x-b90YEvEmSNLj"),sQuery(id+"F0.wireOp",EDGE,"E3"),sQuery(id+"F0.wireOp",EDGE,"E4"),sQuery(id+"F0.wireOp",EDGE,"E7"),sQuery(id+"F0.wireOp",EDGE,"E8"),sQuery(id+"F0.wireOp",EDGE,"E9"),sQuery(id+"F0.wireOp",EDGE,"E10"),sQuery(id+"F0.wireOp",EDGE,"E11"),sQuery(id+"F0.wireOp",EDGE,"E12"),sQuery(id+"F0.wireOp",EDGE,"E13"),sQuery(id+"F0.wireOp",EDGE,"E14.bottom"),sQuery(id+"F0.wireOp",EDGE,"E14.top"),sQuery(id+"F0.wireOp",EDGE,"E14.left"),sQuery(id+"F0.wireOp",EDGE,"E14.right"),sQuery(id+"F0.wireOp",EDGE,"E15"),sQuery(id+"F0.wireOp",EDGE,"E16"),sQuery(id+"F0.wireOp",EDGE,"E18.bottom"),sQuery(id+"F0.wireOp",EDGE,"E18.top"),sQuery(id+"F0.wireOp",EDGE,"E18.left"),sQuery(id+"F0.wireOp",EDGE,"E18.right"),sQuery(id+"F0.wireOp",EDGE,"E20.bottom"),sQuery(id+"F0.wireOp",EDGE,"E20.top"),sQuery(id+"F0.wireOp",EDGE,"E21.left"),sQuery(id+"F0.wireOp",EDGE,"E21.right"),sQuery(id+"F0.wireOp",EDGE,"E22.left"),sQuery(id+"F0.wireOp",EDGE,"E22.right"),sQuery(id+"F0.wireOp",EDGE,"E23.trimOffspring"),sQuery(id+"F0.wireOp",EDGE,"E24.trimOffspring"),sQuery(id+"F0.wireOp",EDGE,"E25.trimOffspring"),sQuery(id+"F0.wireOp",EDGE,"E26.trimOffspring"),sQuery(id+"F0.wireOp",EDGE,"E27.trimOffspring"),sQuery(id+"F0.wireOp",EDGE,"E28.trimOffspring"),sQuery(id+"F0.wireOp",EDGE,"E29.trimOffspring"),sQuery(id+"F0.wireOp",EDGE,"E30.trimOffspring"),sQuery(id+"F0.wireOp",EDGE,"E19.bottom"),sQuery(id+"F0.wireOp",EDGE,"E19.top"),sQuery(id+"F0.wireOp",EDGE,"E19.left"),sQuery(id+"F0.wireOp",EDGE,"E19.right"),sQuery(id+"F0.wireOp",EDGE,"E31.bottom"),sQuery(id+"F0.wireOp",EDGE,"E31.top"),sQuery(id+"F0.wireOp",EDGE,"E32.left"),sQuery(id+"F0.wireOp",EDGE,"E32.right"),sQuery(id+"F0.wireOp",EDGE,"E33.left"),sQuery(id+"F0.wireOp",EDGE,"E33.right"),sQuery(id+"F0.wireOp",EDGE,"E34.trimOffspring"),sQuery(id+"F0.wireOp",EDGE,"E35.trimOffspring"),sQuery(id+"F0.wireOp",EDGE,"E36.trimOffspring"),sQuery(id+"F0.wireOp",EDGE,"E37.trimOffspring"),sQuery(id+"F0.wireOp",EDGE,"E38.trimOffspring"),sQuery(id+"F0.wireOp",EDGE,"E39.trimOffspring"),sQuery(id+"F0.wireOp",EDGE,"E40.trimOffspring"),sQuery(id+"F0.wireOp",EDGE,"E41.trimOffspring"),sQuery(id+"F0.wireOp",EDGE,"E44.left"),sQuery(id+"F0.wireOp",EDGE,"E44.right"),sQuery(id+"F0.wireOp",EDGE,"E45.left"),sQuery(id+"F0.wireOp",EDGE,"E45.right"),sQuery(id+"F0.wireOp",EDGE,"E46"),sQuery(id+"F0.wireOp",EDGE,"E47"),sQuery(id+"F0.wireOp",EDGE,"E48"),sQuery(id+"F0.wireOp",EDGE,"E49"),sQuery(id+"F0.wireOp",EDGE,"E50.1.0.8"),sQuery(id+"F0.wireOp",EDGE,"E50.1.0.22"),sQuery(id+"F0.wireOp",EDGE,"E50.1.0.29"),sQuery(id+"F0.wireOp",EDGE,"E50.1.0.40"),sQuery(id+"F0.wireOp",EDGE,"E50.1.0.46"),sQuery(id+"F0.wireOp",EDGE,"E50.1.0.47"),sQuery(id+"F0.wireOp",EDGE,"E50.1.0.48"),sQuery(id+"F0.wireOp",EDGE,"E50.1.0.52"),sQuery(id+"F0.wireOp",EDGE,"E50.1.0.54"),sQuery(id+"F0.wireOp",EDGE,"E50.1.0.55"),sQuery(id+"F0.wireOp",EDGE,"E50.1.0.56"),sQuery(id+"F0.wireOp",EDGE,"E50.1.0.57"),sQuery(id+"F0.wireOp",EDGE,"E50.1.0.58"),sQuery(id+"F0.wireOp",EDGE,"E50.1.0.59"),sQuery(id+"F0.wireOp",EDGE,"E50.1.0.61"),sQuery(id+"F0.wireOp",EDGE,"E50.1.0.64"),sQuery(id+"F0.wireOp",EDGE,"E50.1.0.65"),sQuery(id+"F0.wireOp",EDGE,"E50.1.0.67"),sQuery(id+"F0.wireOp",EDGE,"E50.1.0.68"),sQuery(id+"F0.wireOp",EDGE,"E50.1.0.70"),sQuery(id+"F0.wireOp",EDGE,"E50.2.0.8"),sQuery(id+"F0.wireOp",EDGE,"E50.2.0.22"),sQuery(id+"F0.wireOp",EDGE,"E50.2.0.29"),sQuery(id+"F0.wireOp",EDGE,"E50.2.0.40"),sQuery(id+"F0.wireOp",EDGE,"E50.2.0.46"),sQuery(id+"F0.wireOp",EDGE,"E50.2.0.47"),sQuery(id+"F0.wireOp",EDGE,"E50.2.0.48"),sQuery(id+"F0.wireOp",EDGE,"E50.2.0.52"),sQuery(id+"F0.wireOp",EDGE,"E50.2.0.54"),sQuery(id+"F0.wireOp",EDGE,"E50.2.0.55"),sQuery(id+"F0.wireOp",EDGE,"E50.2.0.56"),sQuery(id+"F0.wireOp",EDGE,"E50.2.0.57"),sQuery(id+"F0.wireOp",EDGE,"E50.2.0.58"),sQuery(id+"F0.wireOp",EDGE,"E50.2.0.59"),sQuery(id+"F0.wireOp",EDGE,"E50.2.0.61"),sQuery(id+"F0.wireOp",EDGE,"E50.2.0.64"),sQuery(id+"F0.wireOp",EDGE,"E50.2.0.65"),sQuery(id+"F0.wireOp",EDGE,"E50.2.0.67"),sQuery(id+"F0.wireOp",EDGE,"E50.2.0.68"),sQuery(id+"F0.wireOp",EDGE,"E50.2.0.70"),sQuery(id+"F0.wireOp",EDGE,"E51"),sQuery(id+"F0.wireOp",EDGE,"E52")])],"isStart":false});
            var sketch = newSketch(context, id + "F46", { "sketchPlane" : qUnion([Q0])});
            skLineSegment(sketch, "E187.left", {"start": v(-114.5, -48.28) * mm, "end": v(-114.5, -39.8) * mm});
            skLineSegment(sketch, "E187.right", {"start": v(-117.5, -48.28) * mm, "end": v(-117.5, -39.8) * mm});
            skPoint(sketch, "E187.middle", {"position": v(-116, -44.04) * mm});
            skLineSegment(sketch, "E188.left", {"start": v(-74.5, -48.28) * mm, "end": v(-74.5, -39.8) * mm});
            skLineSegment(sketch, "E188.right", {"start": v(-77.5, -48.28) * mm, "end": v(-77.5, -39.8) * mm});
            skPoint(sketch, "E188.middle", {"position": v(-76, -44.04) * mm});
            skLineSegment(sketch, "E189.left", {"start": v(-45.5, -48.28) * mm, "end": v(-45.5, -39.8) * mm});
            skLineSegment(sketch, "E189.right", {"start": v(-48.5, -48.28) * mm, "end": v(-48.5, -39.8) * mm});
            skPoint(sketch, "E189.middle", {"position": v(-47, -44.04) * mm});
            skLineSegment(sketch, "E190.left", {"start": v(-32.5, -48.28) * mm, "end": v(-32.5, -39.8) * mm});
            skLineSegment(sketch, "E190.right", {"start": v(-35.5, -48.28) * mm, "end": v(-35.5, -39.8) * mm});
            skPoint(sketch, "E190.middle", {"position": v(-34, -44.04) * mm});
            skSolve(sketch);
        }
        {
            var Q0;
            {var subQ0=sQuery(id+"F46.wireOp",EDGE,"E187.left");Q0=makeQuery(id+"F46.imprint","IMPRINT",FACE,{"disambiguationData":[TD([[makeQuery(id+"F46.imprint","IMPRINT",EDGE,{"derivedFrom":subQ0}),1.0]])]});}
            var Q1;
            {var subQ0=sQuery(id+"F46.wireOp",EDGE,"E188.left");Q1=makeQuery(id+"F46.imprint","IMPRINT",FACE,{"disambiguationData":[TD([[makeQuery(id+"F46.imprint","IMPRINT",EDGE,{"derivedFrom":subQ0}),1.0]])]});}
            var Q2;
            {var subQ0=sQuery(id+"F46.wireOp",EDGE,"E189.left");Q2=makeQuery(id+"F46.imprint","IMPRINT",FACE,{"disambiguationData":[TD([[makeQuery(id+"F46.imprint","IMPRINT",EDGE,{"derivedFrom":subQ0}),1.0]])]});}
            var Q3;
            {var subQ0=sQuery(id+"F46.wireOp",EDGE,"E190.left");Q3=makeQuery(id+"F46.imprint","IMPRINT",FACE,{"disambiguationData":[TD([[makeQuery(id+"F46.imprint","IMPRINT",EDGE,{"derivedFrom":subQ0}),1.0]])]});}
            extrude(context, id + "F47", {"entities" : qUnion([Q0, Q1, Q2, Q3]), "operationType" : NewBodyOperationType.ADD, "oppositeDirection" : true, "depth" : 1 * mm});
        }
        {
            var Q0;
            Q0=makeQuery(id+"F23.opExtrude","CAP_FACE",FACE,{"disambiguationData":[OSD([sQuery(id+"F1.wireOp",EDGE,"E73.bottom"),sQuery(id+"F1.wireOp",EDGE,"E73.top"),sQuery(id+"F1.wireOp",EDGE,"E73.left"),sQuery(id+"F1.wireOp",EDGE,"E73.right"),sQuery(id+"F1.wireOp",EDGE,"E74.bottom"),sQuery(id+"F1.wireOp",EDGE,"E74.top"),sQuery(id+"F1.wireOp",EDGE,"E74.left"),sQuery(id+"F1.wireOp",EDGE,"E74.right"),sQuery(id+"F1.wireOp",EDGE,"E75.bottom"),sQuery(id+"F1.wireOp",EDGE,"E75.top"),sQuery(id+"F1.wireOp",EDGE,"E75.left"),sQuery(id+"F1.wireOp",EDGE,"E75.right"),sQuery(id+"F1.wireOp",EDGE,"E80"),sQuery(id+"F1.wireOp",EDGE,"E81"),sQuery(id+"F1.wireOp",EDGE,"E83"),sQuery(id+"F1.wireOp",EDGE,"E84"),sQuery(id+"F1.wireOp",EDGE,"E87.bottom"),sQuery(id+"F1.wireOp",EDGE,"E87.top"),sQuery(id+"F1.wireOp",EDGE,"E87.left"),sQuery(id+"F1.wireOp",EDGE,"E87.right"),sQuery(id+"F1.wireOp",EDGE,"E89"),sQuery(id+"F1.wireOp",EDGE,"E92"),sQuery(id+"F1.wireOp",EDGE,"E93"),sQuery(id+"F1.wireOp",EDGE,"CoPGjB9w-zRhk-UiIu-dCG4-BhNkDkZw4NkV"),sQuery(id+"F1.wireOp",EDGE,"XJoTFQyA-9xYx-y9zl-Xs7Z-xe6QLGOleBae"),sQuery(id+"F1.wireOp",EDGE,"E94"),sQuery(id+"F1.wireOp",EDGE,"E95"),sQuery(id+"F1.wireOp",EDGE,"E96"),sQuery(id+"F1.wireOp",EDGE,"E97"),sQuery(id+"F1.wireOp",EDGE,"E98"),sQuery(id+"F1.wireOp",EDGE,"E99"),sQuery(id+"F1.wireOp",EDGE,"E100"),sQuery(id+"F1.wireOp",EDGE,"E101"),sQuery(id+"F1.wireOp",EDGE,"E102"),sQuery(id+"F1.wireOp",EDGE,"E105.1.0.0"),sQuery(id+"F1.wireOp",EDGE,"E105.1.0.1"),sQuery(id+"F1.wireOp",EDGE,"E105.1.0.2"),sQuery(id+"F1.wireOp",EDGE,"E105.1.0.3"),sQuery(id+"F1.wireOp",EDGE,"E105.2.0.0"),sQuery(id+"F1.wireOp",EDGE,"E105.2.0.1"),sQuery(id+"F1.wireOp",EDGE,"E105.2.0.2"),sQuery(id+"F1.wireOp",EDGE,"E105.2.0.3"),sQuery(id+"F1.wireOp",EDGE,"E106.1.0.0"),sQuery(id+"F1.wireOp",EDGE,"E106.1.0.1"),sQuery(id+"F1.wireOp",EDGE,"E106.1.0.2"),sQuery(id+"F1.wireOp",EDGE,"E106.1.0.3"),sQuery(id+"F1.wireOp",EDGE,"E106.2.0.0"),sQuery(id+"F1.wireOp",EDGE,"E106.2.0.1"),sQuery(id+"F1.wireOp",EDGE,"E106.2.0.2"),sQuery(id+"F1.wireOp",EDGE,"E106.2.0.3")])],"isStart":true});
            var sketch = newSketch(context, id + "F48", { "sketchPlane" : qUnion([Q0])});
            skLineSegment(sketch, "E191.bottom", {"start": v(60.16, 138.23) * mm, "end": v(48.16, 138.23) * mm});
            skLineSegment(sketch, "E191.top", {"start": v(60.16, 118.23) * mm, "end": v(48.16, 118.23) * mm});
            skLineSegment(sketch, "E191.left", {"start": v(60.16, 138.23) * mm, "end": v(60.16, 118.23) * mm});
            skLineSegment(sketch, "E191.right", {"start": v(48.16, 138.23) * mm, "end": v(48.16, 118.23) * mm});
            skLineSegment(sketch, "E192.0", {"start": v(59.66, 137.73) * mm, "end": v(59.66, 118.73) * mm});
            skLineSegment(sketch, "E192.1", {"start": v(59.66, 137.73) * mm, "end": v(48.66, 137.73) * mm});
            skLineSegment(sketch, "E192.2", {"start": v(48.66, 137.73) * mm, "end": v(48.66, 118.73) * mm});
            skLineSegment(sketch, "E192.3", {"start": v(59.66, 118.73) * mm, "end": v(48.66, 118.73) * mm});
            skSolve(sketch);
        }
        {
            var Q0;
            Q0 = qSketchRegion(id + "F48", true);
            extrude(context, id + "F49", {"entities" : qUnion([Q0]), "operationType" : NewBodyOperationType.ADD, "oppositeDirection" : true, "depth" : 1 * mm});
        }
        {
            var Q0;
            {var subQ0=sQuery(id+"F0.wireOp",EDGE,"E11");var subQ1=sQuery(id+"F0.wireOp",EDGE,"E10");var subQ2=sQuery(id+"F0.wireOp",EDGE,"E8");var subQ3=sQuery(id+"F0.wireOp",EDGE,"E7");Q0=makeQuery(id+"F47.boolean.opBoolean","MERGE",FACE,{"derivedFrom":[makeQuery(id+"F3.opExtrude","CAP_FACE",FACE,{"disambiguationData":[OSD([sQuery(id+"F0.wireOp",EDGE,"E0.bottom"),sQuery(id+"F0.wireOp",EDGE,"E0.top"),sQuery(id+"F0.wireOp",EDGE,"E0.left"),sQuery(id+"F0.wireOp",EDGE,"E0.right"),sQuery(id+"F0.wireOp",EDGE,"6XQCNLW2-68Wz-nC9p-wT4x-b90YEvEmSNLj"),sQuery(id+"F0.wireOp",EDGE,"E3"),sQuery(id+"F0.wireOp",EDGE,"E4"),subQ3,subQ2,sQuery(id+"F0.wireOp",EDGE,"E9"),subQ1,subQ0,sQuery(id+"F0.wireOp",EDGE,"E12"),sQuery(id+"F0.wireOp",EDGE,"E13"),sQuery(id+"F0.wireOp",EDGE,"E14.bottom"),sQuery(id+"F0.wireOp",EDGE,"E14.top"),sQuery(id+"F0.wireOp",EDGE,"E14.left"),sQuery(id+"F0.wireOp",EDGE,"E14.right"),sQuery(id+"F0.wireOp",EDGE,"E15"),sQuery(id+"F0.wireOp",EDGE,"E16"),sQuery(id+"F0.wireOp",EDGE,"E18.bottom"),sQuery(id+"F0.wireOp",EDGE,"E18.top"),sQuery(id+"F0.wireOp",EDGE,"E18.left"),sQuery(id+"F0.wireOp",EDGE,"E18.right"),sQuery(id+"F0.wireOp",EDGE,"E20.bottom"),sQuery(id+"F0.wireOp",EDGE,"E20.top"),sQuery(id+"F0.wireOp",EDGE,"E21.left"),sQuery(id+"F0.wireOp",EDGE,"E21.right"),sQuery(id+"F0.wireOp",EDGE,"E22.left"),sQuery(id+"F0.wireOp",EDGE,"E22.right"),sQuery(id+"F0.wireOp",EDGE,"E23.trimOffspring"),sQuery(id+"F0.wireOp",EDGE,"E24.trimOffspring"),sQuery(id+"F0.wireOp",EDGE,"E25.trimOffspring"),sQuery(id+"F0.wireOp",EDGE,"E26.trimOffspring"),sQuery(id+"F0.wireOp",EDGE,"E27.trimOffspring"),sQuery(id+"F0.wireOp",EDGE,"E28.trimOffspring"),sQuery(id+"F0.wireOp",EDGE,"E29.trimOffspring"),sQuery(id+"F0.wireOp",EDGE,"E30.trimOffspring"),sQuery(id+"F0.wireOp",EDGE,"E19.bottom"),sQuery(id+"F0.wireOp",EDGE,"E19.top"),sQuery(id+"F0.wireOp",EDGE,"E19.left"),sQuery(id+"F0.wireOp",EDGE,"E19.right"),sQuery(id+"F0.wireOp",EDGE,"E31.bottom"),sQuery(id+"F0.wireOp",EDGE,"E31.top"),sQuery(id+"F0.wireOp",EDGE,"E32.left"),sQuery(id+"F0.wireOp",EDGE,"E32.right"),sQuery(id+"F0.wireOp",EDGE,"E33.left"),sQuery(id+"F0.wireOp",EDGE,"E33.right"),sQuery(id+"F0.wireOp",EDGE,"E34.trimOffspring"),sQuery(id+"F0.wireOp",EDGE,"E35.trimOffspring"),sQuery(id+"F0.wireOp",EDGE,"E36.trimOffspring"),sQuery(id+"F0.wireOp",EDGE,"E37.trimOffspring"),sQuery(id+"F0.wireOp",EDGE,"E38.trimOffspring"),sQuery(id+"F0.wireOp",EDGE,"E39.trimOffspring"),sQuery(id+"F0.wireOp",EDGE,"E40.trimOffspring"),sQuery(id+"F0.wireOp",EDGE,"E41.trimOffspring"),sQuery(id+"F0.wireOp",EDGE,"E44.left"),sQuery(id+"F0.wireOp",EDGE,"E44.right"),sQuery(id+"F0.wireOp",EDGE,"E45.left"),sQuery(id+"F0.wireOp",EDGE,"E45.right"),sQuery(id+"F0.wireOp",EDGE,"E46"),sQuery(id+"F0.wireOp",EDGE,"E47"),sQuery(id+"F0.wireOp",EDGE,"E48"),sQuery(id+"F0.wireOp",EDGE,"E49"),sQuery(id+"F0.wireOp",EDGE,"E50.1.0.0"),sQuery(id+"F0.wireOp",EDGE,"E50.1.0.1"),sQuery(id+"F0.wireOp",EDGE,"E50.1.0.2"),sQuery(id+"F0.wireOp",EDGE,"E50.1.0.3"),sQuery(id+"F0.wireOp",EDGE,"E50.1.0.8"),sQuery(id+"F0.wireOp",EDGE,"E50.1.0.9"),sQuery(id+"F0.wireOp",EDGE,"E50.1.0.10"),sQuery(id+"F0.wireOp",EDGE,"E50.1.0.11"),sQuery(id+"F0.wireOp",EDGE,"E50.1.0.12"),sQuery(id+"F0.wireOp",EDGE,"E50.1.0.13"),sQuery(id+"F0.wireOp",EDGE,"E50.1.0.14"),sQuery(id+"F0.wireOp",EDGE,"E50.1.0.15"),sQuery(id+"F0.wireOp",EDGE,"E50.1.0.16"),sQuery(id+"F0.wireOp",EDGE,"E50.1.0.18"),sQuery(id+"F0.wireOp",EDGE,"E50.1.0.19"),sQuery(id+"F0.wireOp",EDGE,"E50.1.0.21"),sQuery(id+"F0.wireOp",EDGE,"E50.1.0.22"),sQuery(id+"F0.wireOp",EDGE,"E50.1.0.25"),sQuery(id+"F0.wireOp",EDGE,"E50.1.0.27"),sQuery(id+"F0.wireOp",EDGE,"E50.1.0.29"),sQuery(id+"F0.wireOp",EDGE,"E50.1.0.31"),sQuery(id+"F0.wireOp",EDGE,"E50.1.0.32"),sQuery(id+"F0.wireOp",EDGE,"E50.1.0.33"),sQuery(id+"F0.wireOp",EDGE,"E50.1.0.34"),sQuery(id+"F0.wireOp",EDGE,"E50.1.0.36"),sQuery(id+"F0.wireOp",EDGE,"E50.1.0.37"),sQuery(id+"F0.wireOp",EDGE,"E50.1.0.38"),sQuery(id+"F0.wireOp",EDGE,"E50.1.0.40"),sQuery(id+"F0.wireOp",EDGE,"E50.1.0.41"),sQuery(id+"F0.wireOp",EDGE,"E50.1.0.44"),sQuery(id+"F0.wireOp",EDGE,"E50.1.0.45"),sQuery(id+"F0.wireOp",EDGE,"E50.1.0.46"),sQuery(id+"F0.wireOp",EDGE,"E50.1.0.47"),sQuery(id+"F0.wireOp",EDGE,"E50.1.0.48"),sQuery(id+"F0.wireOp",EDGE,"E50.1.0.51"),sQuery(id+"F0.wireOp",EDGE,"E50.1.0.52"),sQuery(id+"F0.wireOp",EDGE,"E50.2.0.0"),sQuery(id+"F0.wireOp",EDGE,"E50.2.0.1"),sQuery(id+"F0.wireOp",EDGE,"E50.2.0.2"),sQuery(id+"F0.wireOp",EDGE,"E50.2.0.3"),sQuery(id+"F0.wireOp",EDGE,"E50.2.0.8"),sQuery(id+"F0.wireOp",EDGE,"E50.2.0.9"),sQuery(id+"F0.wireOp",EDGE,"E50.2.0.10"),sQuery(id+"F0.wireOp",EDGE,"E50.2.0.11"),sQuery(id+"F0.wireOp",EDGE,"E50.2.0.12"),sQuery(id+"F0.wireOp",EDGE,"E50.2.0.13"),sQuery(id+"F0.wireOp",EDGE,"E50.2.0.14"),sQuery(id+"F0.wireOp",EDGE,"E50.2.0.15"),sQuery(id+"F0.wireOp",EDGE,"E50.2.0.16"),sQuery(id+"F0.wireOp",EDGE,"E50.2.0.18"),sQuery(id+"F0.wireOp",EDGE,"E50.2.0.19"),sQuery(id+"F0.wireOp",EDGE,"E50.2.0.21"),sQuery(id+"F0.wireOp",EDGE,"E50.2.0.22"),sQuery(id+"F0.wireOp",EDGE,"E50.2.0.25"),sQuery(id+"F0.wireOp",EDGE,"E50.2.0.27"),sQuery(id+"F0.wireOp",EDGE,"E50.2.0.29"),sQuery(id+"F0.wireOp",EDGE,"E50.2.0.31"),sQuery(id+"F0.wireOp",EDGE,"E50.2.0.32"),sQuery(id+"F0.wireOp",EDGE,"E50.2.0.33"),sQuery(id+"F0.wireOp",EDGE,"E50.2.0.34"),sQuery(id+"F0.wireOp",EDGE,"E50.2.0.36"),sQuery(id+"F0.wireOp",EDGE,"E50.2.0.37"),sQuery(id+"F0.wireOp",EDGE,"E50.2.0.38"),sQuery(id+"F0.wireOp",EDGE,"E50.2.0.40"),sQuery(id+"F0.wireOp",EDGE,"E50.2.0.41"),sQuery(id+"F0.wireOp",EDGE,"E50.2.0.44"),sQuery(id+"F0.wireOp",EDGE,"E50.2.0.45"),sQuery(id+"F0.wireOp",EDGE,"E50.2.0.46"),sQuery(id+"F0.wireOp",EDGE,"E50.2.0.47"),sQuery(id+"F0.wireOp",EDGE,"E50.2.0.48"),sQuery(id+"F0.wireOp",EDGE,"E50.2.0.51"),sQuery(id+"F0.wireOp",EDGE,"E50.2.0.52"),sQuery(id+"F0.wireOp",EDGE,"E51"),sQuery(id+"F0.wireOp",EDGE,"E52"),sQuery(id+"F0.wireOp",EDGE,"E53.left"),sQuery(id+"F0.wireOp",EDGE,"E53.right")])],"isStart":false}),makeQuery(id+"F47.opExtrude","CAP_FACE",FACE,{"disambiguationData":[OSD([subQ3,sQuery(id+"F46.wireOp",EDGE,"E187.left"),sQuery(id+"F46.wireOp",EDGE,"E187.right")])],"isStart":true}),makeQuery(id+"F47.opExtrude","CAP_FACE",FACE,{"disambiguationData":[OSD([subQ2,sQuery(id+"F46.wireOp",EDGE,"E188.left"),sQuery(id+"F46.wireOp",EDGE,"E188.right")])],"isStart":true}),makeQuery(id+"F47.opExtrude","CAP_FACE",FACE,{"disambiguationData":[OSD([subQ1,sQuery(id+"F46.wireOp",EDGE,"E189.left"),sQuery(id+"F46.wireOp",EDGE,"E189.right")])],"isStart":true}),makeQuery(id+"F47.opExtrude","CAP_FACE",FACE,{"disambiguationData":[OSD([subQ0,sQuery(id+"F46.wireOp",EDGE,"E190.left"),sQuery(id+"F46.wireOp",EDGE,"E190.right")])],"isStart":true})]});}
            var sketch = newSketch(context, id + "F50", { "sketchPlane" : qUnion([Q0])});
            skLineSegment(sketch, "E193.bottom", {"start": v(-40, -8.04) * mm, "end": v(-28, -8.04) * mm});
            skLineSegment(sketch, "E193.top", {"start": v(-40, 11.96) * mm, "end": v(-28, 11.96) * mm});
            skLineSegment(sketch, "E193.left", {"start": v(-40, -8.04) * mm, "end": v(-40, 11.96) * mm});
            skLineSegment(sketch, "E193.right", {"start": v(-28, -8.04) * mm, "end": v(-28, 11.96) * mm});
            skSolve(sketch);
        }
        {
            var Q0;
            Q0 = qSketchRegion(id + "F50", true);
            extrude(context, id + "F51", {"entities" : qUnion([Q0]), "operationType" : NewBodyOperationType.REMOVE, "oppositeDirection" : true, "depth" : 3 * mm});
        }
        {
            var Q0;
            {var subQ0=sQuery(id+"F0.wireOp",EDGE,"E11");var subQ1=sQuery(id+"F0.wireOp",EDGE,"E10");var subQ2=sQuery(id+"F0.wireOp",EDGE,"E8");var subQ3=sQuery(id+"F0.wireOp",EDGE,"E7");Q0=makeQuery(id+"F47.boolean.opBoolean","MERGE",FACE,{"derivedFrom":[makeQuery(id+"F3.opExtrude","CAP_FACE",FACE,{"disambiguationData":[OSD([sQuery(id+"F0.wireOp",EDGE,"E0.bottom"),sQuery(id+"F0.wireOp",EDGE,"E0.top"),sQuery(id+"F0.wireOp",EDGE,"E0.left"),sQuery(id+"F0.wireOp",EDGE,"E0.right"),sQuery(id+"F0.wireOp",EDGE,"6XQCNLW2-68Wz-nC9p-wT4x-b90YEvEmSNLj"),sQuery(id+"F0.wireOp",EDGE,"E3"),sQuery(id+"F0.wireOp",EDGE,"E4"),subQ3,subQ2,sQuery(id+"F0.wireOp",EDGE,"E9"),subQ1,subQ0,sQuery(id+"F0.wireOp",EDGE,"E12"),sQuery(id+"F0.wireOp",EDGE,"E13"),sQuery(id+"F0.wireOp",EDGE,"E14.bottom"),sQuery(id+"F0.wireOp",EDGE,"E14.top"),sQuery(id+"F0.wireOp",EDGE,"E14.left"),sQuery(id+"F0.wireOp",EDGE,"E14.right"),sQuery(id+"F0.wireOp",EDGE,"E15"),sQuery(id+"F0.wireOp",EDGE,"E18.bottom"),sQuery(id+"F0.wireOp",EDGE,"E18.top"),sQuery(id+"F0.wireOp",EDGE,"E18.left"),sQuery(id+"F0.wireOp",EDGE,"E18.right"),sQuery(id+"F0.wireOp",EDGE,"E20.bottom"),sQuery(id+"F0.wireOp",EDGE,"E20.top"),sQuery(id+"F0.wireOp",EDGE,"E21.left"),sQuery(id+"F0.wireOp",EDGE,"E21.right"),sQuery(id+"F0.wireOp",EDGE,"E22.left"),sQuery(id+"F0.wireOp",EDGE,"E22.right"),sQuery(id+"F0.wireOp",EDGE,"E23.trimOffspring"),sQuery(id+"F0.wireOp",EDGE,"E24.trimOffspring"),sQuery(id+"F0.wireOp",EDGE,"E25.trimOffspring"),sQuery(id+"F0.wireOp",EDGE,"E26.trimOffspring"),sQuery(id+"F0.wireOp",EDGE,"E27.trimOffspring"),sQuery(id+"F0.wireOp",EDGE,"E28.trimOffspring"),sQuery(id+"F0.wireOp",EDGE,"E29.trimOffspring"),sQuery(id+"F0.wireOp",EDGE,"E30.trimOffspring"),sQuery(id+"F0.wireOp",EDGE,"E19.bottom"),sQuery(id+"F0.wireOp",EDGE,"E19.top"),sQuery(id+"F0.wireOp",EDGE,"E19.left"),sQuery(id+"F0.wireOp",EDGE,"E19.right"),sQuery(id+"F0.wireOp",EDGE,"E31.bottom"),sQuery(id+"F0.wireOp",EDGE,"E31.top"),sQuery(id+"F0.wireOp",EDGE,"E32.left"),sQuery(id+"F0.wireOp",EDGE,"E32.right"),sQuery(id+"F0.wireOp",EDGE,"E33.left"),sQuery(id+"F0.wireOp",EDGE,"E33.right"),sQuery(id+"F0.wireOp",EDGE,"E34.trimOffspring"),sQuery(id+"F0.wireOp",EDGE,"E35.trimOffspring"),sQuery(id+"F0.wireOp",EDGE,"E36.trimOffspring"),sQuery(id+"F0.wireOp",EDGE,"E37.trimOffspring"),sQuery(id+"F0.wireOp",EDGE,"E38.trimOffspring"),sQuery(id+"F0.wireOp",EDGE,"E39.trimOffspring"),sQuery(id+"F0.wireOp",EDGE,"E40.trimOffspring"),sQuery(id+"F0.wireOp",EDGE,"E41.trimOffspring"),sQuery(id+"F0.wireOp",EDGE,"E44.left"),sQuery(id+"F0.wireOp",EDGE,"E44.right"),sQuery(id+"F0.wireOp",EDGE,"E45.left"),sQuery(id+"F0.wireOp",EDGE,"E45.right"),sQuery(id+"F0.wireOp",EDGE,"E46"),sQuery(id+"F0.wireOp",EDGE,"E47"),sQuery(id+"F0.wireOp",EDGE,"E48"),sQuery(id+"F0.wireOp",EDGE,"E49"),sQuery(id+"F0.wireOp",EDGE,"E50.1.0.0"),sQuery(id+"F0.wireOp",EDGE,"E50.1.0.1"),sQuery(id+"F0.wireOp",EDGE,"E50.1.0.2"),sQuery(id+"F0.wireOp",EDGE,"E50.1.0.3"),sQuery(id+"F0.wireOp",EDGE,"E50.1.0.8"),sQuery(id+"F0.wireOp",EDGE,"E50.1.0.9"),sQuery(id+"F0.wireOp",EDGE,"E50.1.0.10"),sQuery(id+"F0.wireOp",EDGE,"E50.1.0.11"),sQuery(id+"F0.wireOp",EDGE,"E50.1.0.12"),sQuery(id+"F0.wireOp",EDGE,"E50.1.0.13"),sQuery(id+"F0.wireOp",EDGE,"E50.1.0.14"),sQuery(id+"F0.wireOp",EDGE,"E50.1.0.15"),sQuery(id+"F0.wireOp",EDGE,"E50.1.0.16"),sQuery(id+"F0.wireOp",EDGE,"E50.1.0.18"),sQuery(id+"F0.wireOp",EDGE,"E50.1.0.19"),sQuery(id+"F0.wireOp",EDGE,"E50.1.0.21"),sQuery(id+"F0.wireOp",EDGE,"E50.1.0.22"),sQuery(id+"F0.wireOp",EDGE,"E50.1.0.25"),sQuery(id+"F0.wireOp",EDGE,"E50.1.0.27"),sQuery(id+"F0.wireOp",EDGE,"E50.1.0.29"),sQuery(id+"F0.wireOp",EDGE,"E50.1.0.31"),sQuery(id+"F0.wireOp",EDGE,"E50.1.0.32"),sQuery(id+"F0.wireOp",EDGE,"E50.1.0.33"),sQuery(id+"F0.wireOp",EDGE,"E50.1.0.34"),sQuery(id+"F0.wireOp",EDGE,"E50.1.0.36"),sQuery(id+"F0.wireOp",EDGE,"E50.1.0.37"),sQuery(id+"F0.wireOp",EDGE,"E50.1.0.38"),sQuery(id+"F0.wireOp",EDGE,"E50.1.0.40"),sQuery(id+"F0.wireOp",EDGE,"E50.1.0.41"),sQuery(id+"F0.wireOp",EDGE,"E50.1.0.44"),sQuery(id+"F0.wireOp",EDGE,"E50.1.0.45"),sQuery(id+"F0.wireOp",EDGE,"E50.1.0.46"),sQuery(id+"F0.wireOp",EDGE,"E50.1.0.47"),sQuery(id+"F0.wireOp",EDGE,"E50.1.0.48"),sQuery(id+"F0.wireOp",EDGE,"E50.1.0.51"),sQuery(id+"F0.wireOp",EDGE,"E50.1.0.52"),sQuery(id+"F0.wireOp",EDGE,"E50.2.0.0"),sQuery(id+"F0.wireOp",EDGE,"E50.2.0.1"),sQuery(id+"F0.wireOp",EDGE,"E50.2.0.2"),sQuery(id+"F0.wireOp",EDGE,"E50.2.0.3"),sQuery(id+"F0.wireOp",EDGE,"E50.2.0.8"),sQuery(id+"F0.wireOp",EDGE,"E50.2.0.9"),sQuery(id+"F0.wireOp",EDGE,"E50.2.0.10"),sQuery(id+"F0.wireOp",EDGE,"E50.2.0.11"),sQuery(id+"F0.wireOp",EDGE,"E50.2.0.12"),sQuery(id+"F0.wireOp",EDGE,"E50.2.0.13"),sQuery(id+"F0.wireOp",EDGE,"E50.2.0.14"),sQuery(id+"F0.wireOp",EDGE,"E50.2.0.15"),sQuery(id+"F0.wireOp",EDGE,"E50.2.0.16"),sQuery(id+"F0.wireOp",EDGE,"E50.2.0.18"),sQuery(id+"F0.wireOp",EDGE,"E50.2.0.19"),sQuery(id+"F0.wireOp",EDGE,"E50.2.0.21"),sQuery(id+"F0.wireOp",EDGE,"E50.2.0.22"),sQuery(id+"F0.wireOp",EDGE,"E50.2.0.25"),sQuery(id+"F0.wireOp",EDGE,"E50.2.0.27"),sQuery(id+"F0.wireOp",EDGE,"E50.2.0.29"),sQuery(id+"F0.wireOp",EDGE,"E50.2.0.31"),sQuery(id+"F0.wireOp",EDGE,"E50.2.0.32"),sQuery(id+"F0.wireOp",EDGE,"E50.2.0.33"),sQuery(id+"F0.wireOp",EDGE,"E50.2.0.34"),sQuery(id+"F0.wireOp",EDGE,"E50.2.0.36"),sQuery(id+"F0.wireOp",EDGE,"E50.2.0.37"),sQuery(id+"F0.wireOp",EDGE,"E50.2.0.38"),sQuery(id+"F0.wireOp",EDGE,"E50.2.0.40"),sQuery(id+"F0.wireOp",EDGE,"E50.2.0.41"),sQuery(id+"F0.wireOp",EDGE,"E50.2.0.44"),sQuery(id+"F0.wireOp",EDGE,"E50.2.0.45"),sQuery(id+"F0.wireOp",EDGE,"E50.2.0.46"),sQuery(id+"F0.wireOp",EDGE,"E50.2.0.47"),sQuery(id+"F0.wireOp",EDGE,"E50.2.0.48"),sQuery(id+"F0.wireOp",EDGE,"E50.2.0.51"),sQuery(id+"F0.wireOp",EDGE,"E50.2.0.52"),sQuery(id+"F0.wireOp",EDGE,"E51"),sQuery(id+"F0.wireOp",EDGE,"E52"),sQuery(id+"F0.wireOp",EDGE,"E53.left"),sQuery(id+"F0.wireOp",EDGE,"E53.right"),sQuery(id+"F0.wireOp",EDGE,"E54.bottom"),sQuery(id+"F0.wireOp",EDGE,"E54.top"),sQuery(id+"F0.wireOp",EDGE,"E54.left"),sQuery(id+"F0.wireOp",EDGE,"E54.right"),sQuery(id+"F0.wireOp",EDGE,"E55.bottom"),sQuery(id+"F0.wireOp",EDGE,"E55.top")])],"isStart":false}),makeQuery(id+"F47.opExtrude","CAP_FACE",FACE,{"disambiguationData":[OSD([subQ3,sQuery(id+"F46.wireOp",EDGE,"E187.left"),sQuery(id+"F46.wireOp",EDGE,"E187.right")])],"isStart":true}),makeQuery(id+"F47.opExtrude","CAP_FACE",FACE,{"disambiguationData":[OSD([subQ2,sQuery(id+"F46.wireOp",EDGE,"E188.left"),sQuery(id+"F46.wireOp",EDGE,"E188.right")])],"isStart":true}),makeQuery(id+"F47.opExtrude","CAP_FACE",FACE,{"disambiguationData":[OSD([subQ1,sQuery(id+"F46.wireOp",EDGE,"E189.left"),sQuery(id+"F46.wireOp",EDGE,"E189.right")])],"isStart":true}),makeQuery(id+"F47.opExtrude","CAP_FACE",FACE,{"disambiguationData":[OSD([subQ0,sQuery(id+"F46.wireOp",EDGE,"E190.left"),sQuery(id+"F46.wireOp",EDGE,"E190.right")])],"isStart":true})]});}
            var sketch = newSketch(context, id + "F52", { "sketchPlane" : qUnion([Q0])});
            skLineSegment(sketch, "E194.bottom", {"start": v(-24.5, -13.04) * mm, "end": v(-10.5, -13.04) * mm});
            skLineSegment(sketch, "E194.top", {"start": v(-24.5, -29.04) * mm, "end": v(-10.5, -29.04) * mm});
            skLineSegment(sketch, "E194.left", {"start": v(-24.5, -13.04) * mm, "end": v(-24.5, -29.04) * mm});
            skLineSegment(sketch, "E194.right", {"start": v(-10.5, -13.04) * mm, "end": v(-10.5, -29.04) * mm});
            skSolve(sketch);
        }
        {
            var Q0;
            Q0 = qSketchRegion(id + "F52", true);
            extrude(context, id + "F53", {"entities" : qUnion([Q0]), "operationType" : NewBodyOperationType.REMOVE, "oppositeDirection" : true, "depth" : 5 * mm});
        }
        {
            var Q0;
            Q0=qCreatedBy(makeId("Top.planeOp"),FACE);
            var sketch = newSketch(context, id + "F54", { "sketchPlane" : qUnion([Q0])});
            skLineSegment(sketch, "E195.bottom", {"start": v(-122.3, 89.38) * mm, "end": v(-140.3, 89.38) * mm});
            skLineSegment(sketch, "E195.top", {"start": v(-122.3, 107.38) * mm, "end": v(-140.3, 107.38) * mm});
            skLineSegment(sketch, "E195.left", {"start": v(-122.3, 89.38) * mm, "end": v(-122.3, 107.38) * mm});
            skLineSegment(sketch, "E195.right", {"start": v(-140.3, 89.38) * mm, "end": v(-140.3, 107.38) * mm});
            skPoint(sketch, "E195.middle", {"position": v(-131.3, 98.38) * mm});
            skLineSegment(sketch, "E196.bottom", {"start": v(57.55, -103.78) * mm, "end": v(45.75, -103.78) * mm});
            skLineSegment(sketch, "E196.top", {"start": v(57.55, -83.98) * mm, "end": v(45.75, -83.98) * mm});
            skLineSegment(sketch, "E196.left", {"start": v(57.55, -103.78) * mm, "end": v(57.55, -83.98) * mm});
            skLineSegment(sketch, "E196.right", {"start": v(45.75, -103.78) * mm, "end": v(45.75, -83.98) * mm});
            skPoint(sketch, "E196.middle", {"position": v(51.65, -93.88) * mm});
            skSolve(sketch);
        }
        {
            var Q0;
            Q0=makeQuery(id+"F54.imprint","IMPRINT",FACE,{"disambiguationData":[TD([[makeQuery(id+"F54.imprint","IMPRINT",EDGE,{"derivedFrom":sQuery(id+"F54.wireOp",EDGE,"E196.bottom")}),-1.0]])]});
            var Q1;
            Q1=makeQuery(id+"F54.imprint","IMPRINT",FACE,{"disambiguationData":[TD([[makeQuery(id+"F54.imprint","IMPRINT",EDGE,{"derivedFrom":sQuery(id+"F54.wireOp",EDGE,"E195.bottom")}),-1.0]])]});
            extrude(context, id + "F55", {"entities" : qUnion([Q0, Q1]), "depth" : 1 * mm});
        }
        {
            var Q0;
            Q0=makeQuery(id+"F23.opExtrude","SWEPT_EDGE",EDGE,{"disambiguationData":[OSD([sQuery(id+"F1.wireOp",EDGE,"E87.top"),sQuery(id+"F1.wireOp",EDGE,"E87.right")])]});
            var Q1;
            Q1=makeQuery(id+"F49.opExtrude","SWEPT_EDGE",EDGE,{"disambiguationData":[OSD([sQuery(id+"F48.wireOp",EDGE,"E192.2"),sQuery(id+"F48.wireOp",EDGE,"E192.3")])]});
            var Q2;
            Q2=makeQuery(id+"F49.opExtrude","SWEPT_EDGE",EDGE,{"disambiguationData":[OSD([sQuery(id+"F48.wireOp",EDGE,"E192.0"),sQuery(id+"F48.wireOp",EDGE,"E192.3")])]});
            var Q3;
            Q3=makeQuery(id+"F23.opExtrude","SWEPT_EDGE",EDGE,{"disambiguationData":[OSD([sQuery(id+"F1.wireOp",EDGE,"E87.top"),sQuery(id+"F1.wireOp",EDGE,"E87.left")])]});
            var Q4;
            Q4=makeQuery(id+"F49.opExtrude","SWEPT_EDGE",EDGE,{"disambiguationData":[OSD([sQuery(id+"F48.wireOp",EDGE,"E192.0"),sQuery(id+"F48.wireOp",EDGE,"E192.1")])]});
            var Q5;
            Q5=makeQuery(id+"F23.opExtrude","SWEPT_EDGE",EDGE,{"disambiguationData":[OSD([sQuery(id+"F1.wireOp",EDGE,"E87.bottom"),sQuery(id+"F1.wireOp",EDGE,"E87.left")])]});
            var Q6;
            Q6=makeQuery(id+"F49.opExtrude","SWEPT_EDGE",EDGE,{"disambiguationData":[OSD([sQuery(id+"F48.wireOp",EDGE,"E192.1"),sQuery(id+"F48.wireOp",EDGE,"E192.2")])]});
            var Q7;
            Q7=makeQuery(id+"F23.opExtrude","SWEPT_EDGE",EDGE,{"disambiguationData":[OSD([sQuery(id+"F1.wireOp",EDGE,"E87.bottom"),sQuery(id+"F1.wireOp",EDGE,"E87.right")])]});
            var Q8;
            Q8=makeQuery(id+"F55.opExtrude","SWEPT_EDGE",EDGE,{"disambiguationData":[OSD([sQuery(id+"F54.wireOp",EDGE,"E196.bottom"),sQuery(id+"F54.wireOp",EDGE,"E196.right")])]});
            var Q9;
            Q9=makeQuery(id+"F55.opExtrude","SWEPT_EDGE",EDGE,{"disambiguationData":[OSD([sQuery(id+"F54.wireOp",EDGE,"E196.bottom"),sQuery(id+"F54.wireOp",EDGE,"E196.left")])]});
            var Q10;
            Q10=makeQuery(id+"F55.opExtrude","SWEPT_EDGE",EDGE,{"disambiguationData":[OSD([sQuery(id+"F54.wireOp",EDGE,"E196.top"),sQuery(id+"F54.wireOp",EDGE,"E196.right")])]});
            var Q11;
            Q11=makeQuery(id+"F55.opExtrude","SWEPT_EDGE",EDGE,{"disambiguationData":[OSD([sQuery(id+"F54.wireOp",EDGE,"E196.top"),sQuery(id+"F54.wireOp",EDGE,"E196.left")])]});
            fillet(context, id + "F56", {"entities" : qUnion([Q0, Q1, Q2, Q3, Q4, Q5, Q6, Q7, Q8, Q9, Q10, Q11]), "radius" : 1 * mm, "tangentPropagation" : true, "allowEdgeOverflow" : false});
        }
        {
            var Q0;
            Q0=makeQuery(id+"F23.opExtrude","CAP_FACE",FACE,{"disambiguationData":[OSD([sQuery(id+"F1.wireOp",EDGE,"E73.bottom"),sQuery(id+"F1.wireOp",EDGE,"E73.top"),sQuery(id+"F1.wireOp",EDGE,"E73.left"),sQuery(id+"F1.wireOp",EDGE,"E73.right"),sQuery(id+"F1.wireOp",EDGE,"E74.bottom"),sQuery(id+"F1.wireOp",EDGE,"E74.top"),sQuery(id+"F1.wireOp",EDGE,"E74.left"),sQuery(id+"F1.wireOp",EDGE,"E74.right"),sQuery(id+"F1.wireOp",EDGE,"E75.bottom"),sQuery(id+"F1.wireOp",EDGE,"E75.top"),sQuery(id+"F1.wireOp",EDGE,"E75.left"),sQuery(id+"F1.wireOp",EDGE,"E75.right"),sQuery(id+"F1.wireOp",EDGE,"E80"),sQuery(id+"F1.wireOp",EDGE,"E81"),sQuery(id+"F1.wireOp",EDGE,"E83"),sQuery(id+"F1.wireOp",EDGE,"E84"),sQuery(id+"F1.wireOp",EDGE,"E87.bottom"),sQuery(id+"F1.wireOp",EDGE,"E87.top"),sQuery(id+"F1.wireOp",EDGE,"E87.left"),sQuery(id+"F1.wireOp",EDGE,"E87.right"),sQuery(id+"F1.wireOp",EDGE,"E89"),sQuery(id+"F1.wireOp",EDGE,"E92"),sQuery(id+"F1.wireOp",EDGE,"E93"),sQuery(id+"F1.wireOp",EDGE,"CoPGjB9w-zRhk-UiIu-dCG4-BhNkDkZw4NkV"),sQuery(id+"F1.wireOp",EDGE,"XJoTFQyA-9xYx-y9zl-Xs7Z-xe6QLGOleBae"),sQuery(id+"F1.wireOp",EDGE,"E94"),sQuery(id+"F1.wireOp",EDGE,"E95"),sQuery(id+"F1.wireOp",EDGE,"E96"),sQuery(id+"F1.wireOp",EDGE,"E97"),sQuery(id+"F1.wireOp",EDGE,"E98"),sQuery(id+"F1.wireOp",EDGE,"E99"),sQuery(id+"F1.wireOp",EDGE,"E100"),sQuery(id+"F1.wireOp",EDGE,"E101"),sQuery(id+"F1.wireOp",EDGE,"E102"),sQuery(id+"F1.wireOp",EDGE,"E105.1.0.0"),sQuery(id+"F1.wireOp",EDGE,"E105.1.0.1"),sQuery(id+"F1.wireOp",EDGE,"E105.1.0.2"),sQuery(id+"F1.wireOp",EDGE,"E105.1.0.3"),sQuery(id+"F1.wireOp",EDGE,"E105.2.0.0"),sQuery(id+"F1.wireOp",EDGE,"E105.2.0.1"),sQuery(id+"F1.wireOp",EDGE,"E105.2.0.2"),sQuery(id+"F1.wireOp",EDGE,"E105.2.0.3"),sQuery(id+"F1.wireOp",EDGE,"E106.1.0.0"),sQuery(id+"F1.wireOp",EDGE,"E106.1.0.1"),sQuery(id+"F1.wireOp",EDGE,"E106.1.0.2"),sQuery(id+"F1.wireOp",EDGE,"E106.1.0.3"),sQuery(id+"F1.wireOp",EDGE,"E106.2.0.0"),sQuery(id+"F1.wireOp",EDGE,"E106.2.0.1"),sQuery(id+"F1.wireOp",EDGE,"E106.2.0.2"),sQuery(id+"F1.wireOp",EDGE,"E106.2.0.3")])],"isStart":false});
            var sketch = newSketch(context, id + "F57", { "sketchPlane" : qUnion([Q0])});
            skCircle(sketch, "E197", {"center": v(-56.34, -124.73) * mm, "radius": 5 * mm});
            skCircle(sketch, "E198", {"center": v(-56.34, -174.73) * mm, "radius": 5 * mm});
            skCircle(sketch, "E199", {"center": v(83.66, -124.73) * mm, "radius": 5 * mm});
            skCircle(sketch, "E200", {"center": v(83.66, -174.73) * mm, "radius": 5 * mm});
            skLineSegment(sketch, "E201.bottom", {"start": v(-66.34, -129.73) * mm, "end": v(-56.34, -129.73) * mm});
            skLineSegment(sketch, "E201.top", {"start": v(-66.34, -119.73) * mm, "end": v(-56.34, -119.73) * mm});
            skLineSegment(sketch, "E201.left", {"start": v(-66.34, -129.73) * mm, "end": v(-66.34, -119.73) * mm});
            skLineSegment(sketch, "E202.bottom", {"start": v(-56.34, -179.73) * mm, "end": v(-66.34, -179.73) * mm});
            skLineSegment(sketch, "E202.top", {"start": v(-56.34, -169.73) * mm, "end": v(-66.34, -169.73) * mm});
            skLineSegment(sketch, "E202.right", {"start": v(-66.34, -179.73) * mm, "end": v(-66.34, -169.73) * mm});
            skLineSegment(sketch, "E203.bottom", {"start": v(98.24, -129.73) * mm, "end": v(83.66, -129.73) * mm});
            skLineSegment(sketch, "E203.top", {"start": v(98.24, -119.73) * mm, "end": v(83.66, -119.73) * mm});
            skLineSegment(sketch, "E203.left", {"start": v(98.24, -129.73) * mm, "end": v(98.24, -119.73) * mm});
            skLineSegment(sketch, "E204.bottom", {"start": v(93.66, -179.73) * mm, "end": v(83.66, -179.73) * mm});
            skLineSegment(sketch, "E204.top", {"start": v(93.66, -169.73) * mm, "end": v(83.66, -169.73) * mm});
            skLineSegment(sketch, "E204.left", {"start": v(93.66, -179.73) * mm, "end": v(93.66, -169.73) * mm});
            skSolve(sketch);
        }
        {
            var Q0;
            Q0 = qSketchRegion(id + "F57", true);
            extrude(context, id + "F58", {"entities" : qUnion([Q0]), "operationType" : NewBodyOperationType.REMOVE, "oppositeDirection" : true, "depth" : 1 * mm});
        }
        {
            var Q0;
            Q0=makeQuery(id+"F10.opExtrude","CAP_EDGE",EDGE,{"disambiguationData":[OSD([sQuery(id+"F9.wireOp",EDGE,"E141.0")])],"isStart":false});
            var Q1;
            Q1=makeQuery(id+"F10.opExtrude","CAP_EDGE",EDGE,{"disambiguationData":[OSD([sQuery(id+"F9.wireOp",EDGE,"E141.3")])],"isStart":false});
            var Q2;
            Q2=makeQuery(id+"F10.opExtrude","CAP_EDGE",EDGE,{"disambiguationData":[OSD([sQuery(id+"F9.wireOp",EDGE,"E141.2")])],"isStart":false});
            var Q3;
            Q3=makeQuery(id+"F10.opExtrude","CAP_EDGE",EDGE,{"disambiguationData":[OSD([sQuery(id+"F9.wireOp",EDGE,"E141.1")])],"isStart":false});
            var Q4;
            {var subQ0=sQuery(id+"F1.wireOp",EDGE,"E73.right");var subQ1=sQuery(id+"F1.wireOp",EDGE,"E73.top");Q4=makeQuery(id+"F58.boolean.opBoolean","SPLIT",EDGE,{"disambiguationData":[TD([makeQuery(id+"F23.opExtrude","SWEPT_FACE",FACE,{"disambiguationData":[OSD([subQ1])]})])],"derivedFrom":makeQuery(id+"F23.opExtrude","CAP_EDGE",EDGE,{"disambiguationData":[OSD([subQ0])],"isStart":false})});}
            var Q5;
            Q5=makeQuery(id+"F23.opExtrude","CAP_EDGE",EDGE,{"disambiguationData":[OSD([sQuery(id+"F1.wireOp",EDGE,"E73.top")])],"isStart":false});
            var Q6;
            Q6=makeQuery(id+"F58.boolean.opBoolean","COPY",EDGE,{"derivedFrom":makeQuery(id+"F58.opExtrude","CAP_EDGE",EDGE,{"disambiguationData":[OSD([sQuery(id+"F57.wireOp",EDGE,"E201.top")])],"isStart":true})});
            var Q7;
            {var subQ0=sQuery(id+"F1.wireOp",EDGE,"E73.right");Q7=makeQuery(id+"F58.boolean.opBoolean","SPLIT",EDGE,{"disambiguationData":[TD([makeQuery(id+"F58.opExtrude","SWEPT_FACE",FACE,{"disambiguationData":[OSD([sQuery(id+"F57.wireOp",EDGE,"E201.bottom")])]})])],"derivedFrom":makeQuery(id+"F23.opExtrude","CAP_EDGE",EDGE,{"disambiguationData":[OSD([subQ0])],"isStart":false})});}
            var Q8;
            Q8=makeQuery(id+"F58.boolean.opBoolean","COPY",EDGE,{"derivedFrom":makeQuery(id+"F58.opExtrude","CAP_EDGE",EDGE,{"disambiguationData":[OSD([sQuery(id+"F57.wireOp",EDGE,"E202.top")])],"isStart":true})});
            var Q9;
            {var subQ0=sQuery(id+"F1.wireOp",EDGE,"E73.bottom");var subQ1=sQuery(id+"F1.wireOp",EDGE,"E73.right");Q9=makeQuery(id+"F58.boolean.opBoolean","SPLIT",EDGE,{"disambiguationData":[TD([makeQuery(id+"F23.opExtrude","SWEPT_FACE",FACE,{"disambiguationData":[OSD([subQ0])]})])],"derivedFrom":makeQuery(id+"F23.opExtrude","CAP_EDGE",EDGE,{"disambiguationData":[OSD([subQ1])],"isStart":false})});}
            var Q10;
            Q10=makeQuery(id+"F23.opExtrude","CAP_EDGE",EDGE,{"disambiguationData":[OSD([sQuery(id+"F1.wireOp",EDGE,"E73.bottom")])],"isStart":false});
            var Q11;
            {var subQ0=sQuery(id+"F1.wireOp",EDGE,"E73.bottom");var subQ1=sQuery(id+"F1.wireOp",EDGE,"E73.left");Q11=makeQuery(id+"F58.boolean.opBoolean","SPLIT",EDGE,{"disambiguationData":[TD([makeQuery(id+"F23.opExtrude","SWEPT_FACE",FACE,{"disambiguationData":[OSD([subQ0])]})])],"derivedFrom":makeQuery(id+"F23.opExtrude","CAP_EDGE",EDGE,{"disambiguationData":[OSD([subQ1])],"isStart":false})});}
            var Q12;
            Q12=makeQuery(id+"F58.boolean.opBoolean","COPY",EDGE,{"derivedFrom":makeQuery(id+"F58.opExtrude","CAP_EDGE",EDGE,{"disambiguationData":[OSD([sQuery(id+"F57.wireOp",EDGE,"E204.bottom")])],"isStart":true})});
            var Q13;
            {var subQ0=sQuery(id+"F1.wireOp",EDGE,"E73.left");Q13=makeQuery(id+"F58.boolean.opBoolean","SPLIT",EDGE,{"disambiguationData":[TD([makeQuery(id+"F58.opExtrude","SWEPT_FACE",FACE,{"disambiguationData":[OSD([sQuery(id+"F57.wireOp",EDGE,"E203.bottom")])]})])],"derivedFrom":makeQuery(id+"F23.opExtrude","CAP_EDGE",EDGE,{"disambiguationData":[OSD([subQ0])],"isStart":false})});}
            var Q14;
            Q14=makeQuery(id+"F58.boolean.opBoolean","COPY",EDGE,{"derivedFrom":makeQuery(id+"F58.opExtrude","CAP_EDGE",EDGE,{"disambiguationData":[OSD([sQuery(id+"F57.wireOp",EDGE,"E203.bottom")])],"isStart":true})});
            var Q15;
            {var subQ0=sQuery(id+"F1.wireOp",EDGE,"E73.left");var subQ1=sQuery(id+"F1.wireOp",EDGE,"E73.top");Q15=makeQuery(id+"F58.boolean.opBoolean","SPLIT",EDGE,{"disambiguationData":[TD([makeQuery(id+"F23.opExtrude","SWEPT_FACE",FACE,{"disambiguationData":[OSD([subQ1])]})])],"derivedFrom":makeQuery(id+"F23.opExtrude","CAP_EDGE",EDGE,{"disambiguationData":[OSD([subQ0])],"isStart":false})});}
            fillet(context, id + "F59", {"entities" : qUnion([Q0, Q1, Q2, Q3, Q4, Q5, Q6, Q7, Q8, Q9, Q10, Q11, Q12, Q13, Q14, Q15]), "radius" : 0.5 * mm, "tangentPropagation" : true, "allowEdgeOverflow" : false});
        }
    });
